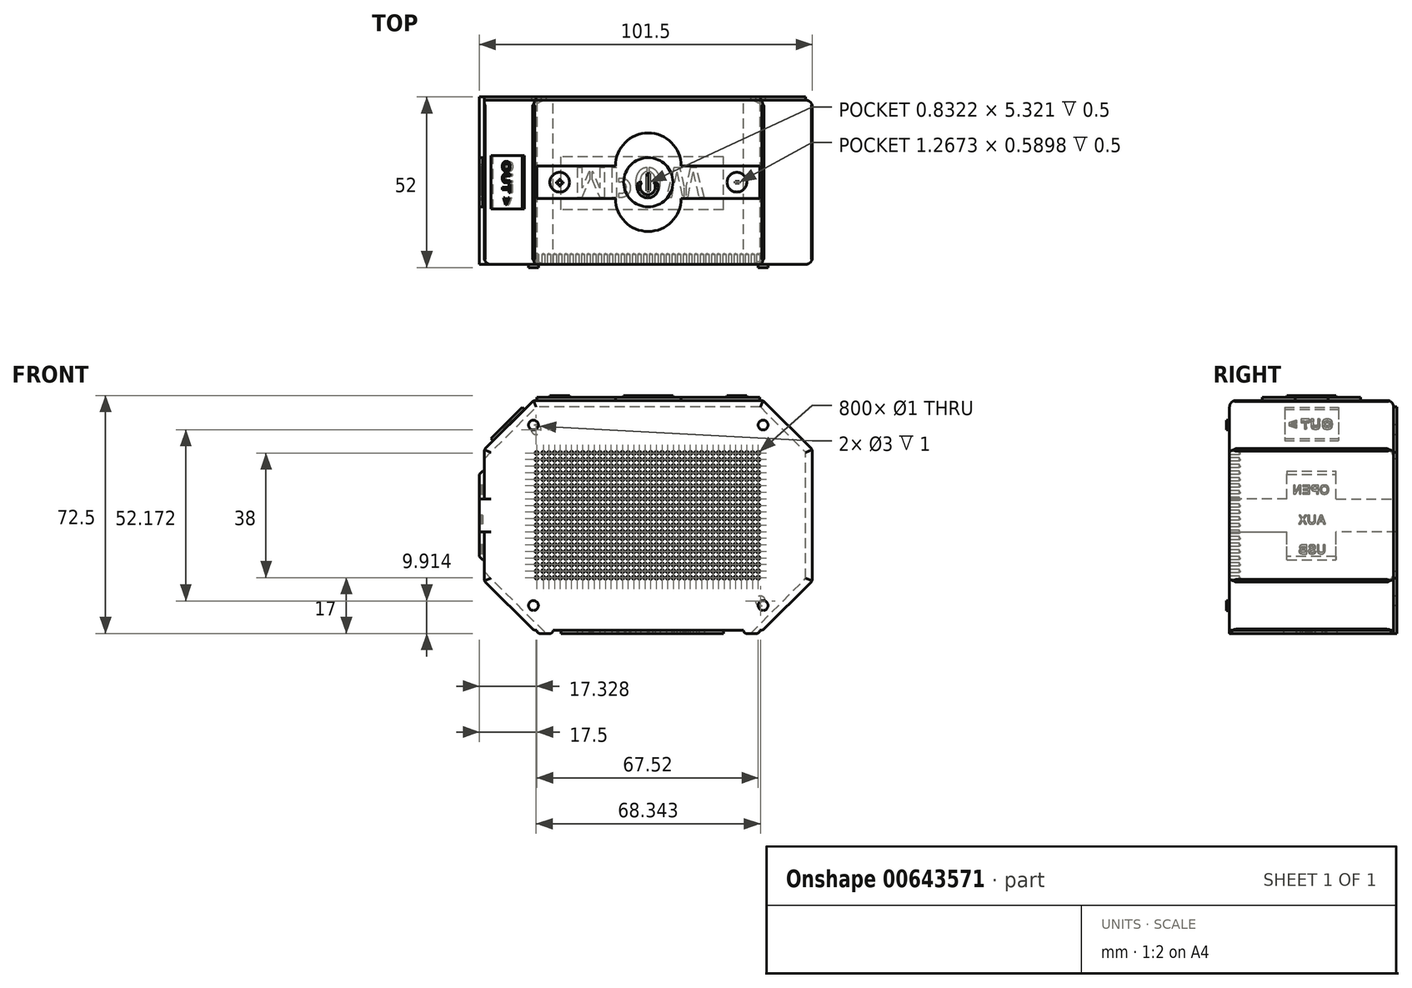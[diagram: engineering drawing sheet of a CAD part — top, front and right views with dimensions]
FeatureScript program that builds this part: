
annotation { "Feature Type Name" : "Feature", "Feature Type Description" : "" }
export const myFeature = defineFeature(function(context is Context, id is Id, definition is map)
    precondition{}
    {
        {
            var Q0;
            Q0=qCreatedBy(makeId("Front.planeOp"),FACE);
            var sketch = newSketch(context, id + "F0", { "sketchPlane" : qUnion([Q0])});
            skLineSegment(sketch, "E0.bottom", {"start": v(35, -35) * mm, "end": v(-35, -35) * mm});
            skLineSegment(sketch, "E0.top", {"start": v(35, 35) * mm, "end": v(-35, 35) * mm});
            skLineSegment(sketch, "E0.left", {"start": v(50, -20) * mm, "end": v(50, 20) * mm});
            skLineSegment(sketch, "E0.right", {"start": v(-50, -20) * mm, "end": v(-50, 20) * mm});
            skPoint(sketch, "E0.middle", {"position": v(0, 0) * mm});
            skLineSegment(sketch, "E1", {"start": v(-50, 20) * mm, "end": v(-35, 35) * mm});
            skLineSegment(sketch, "E2", {"start": v(-50, -20) * mm, "end": v(-35, -35) * mm});
            skLineSegment(sketch, "E3", {"start": v(35, -35) * mm, "end": v(50, -20) * mm});
            skLineSegment(sketch, "E4", {"start": v(35, 35) * mm, "end": v(50, 20) * mm});
            skPoint(sketch, "E5.orphan", {"position": v(-50, 35) * mm});
            skPoint(sketch, "E6.orphan", {"position": v(50, 35) * mm});
            skPoint(sketch, "E7.orphan", {"position": v(-50, -35) * mm});
            skPoint(sketch, "E8.orphan", {"position": v(50, -35) * mm});
            skSolve(sketch);
        }
        {
            var Q0;
            Q0 = qSketchRegion(id + "F0", true);
            extrude(context, id + "F1", {"entities" : qUnion([Q0]), "oppositeDirection" : true, "depth" : 50 * mm, "offsetDistance" : 25 * mm});
        }
        {
            var Q0;
            Q0=makeQuery(id+"F1.opExtrude","SWEPT_EDGE",EDGE,{"disambiguationData":[OSD([sQuery(id+"F0.wireOp",EDGE,"E0.top"),sQuery(id+"F0.wireOp",EDGE,"E4")])]});
            var Q1;
            Q1=makeQuery(id+"F1.opExtrude","SWEPT_EDGE",EDGE,{"disambiguationData":[OSD([sQuery(id+"F0.wireOp",EDGE,"E0.left"),sQuery(id+"F0.wireOp",EDGE,"E4")])]});
            var Q2;
            Q2=makeQuery(id+"F1.opExtrude","SWEPT_EDGE",EDGE,{"disambiguationData":[OSD([sQuery(id+"F0.wireOp",EDGE,"E0.left"),sQuery(id+"F0.wireOp",EDGE,"E3")])]});
            var Q3;
            Q3=makeQuery(id+"F1.opExtrude","SWEPT_EDGE",EDGE,{"disambiguationData":[OSD([sQuery(id+"F0.wireOp",EDGE,"E0.bottom"),sQuery(id+"F0.wireOp",EDGE,"E3")])]});
            var Q4;
            Q4=makeQuery(id+"F1.opExtrude","SWEPT_EDGE",EDGE,{"disambiguationData":[OSD([sQuery(id+"F0.wireOp",EDGE,"E0.bottom"),sQuery(id+"F0.wireOp",EDGE,"E2")])]});
            var Q5;
            Q5=makeQuery(id+"F1.opExtrude","SWEPT_EDGE",EDGE,{"disambiguationData":[OSD([sQuery(id+"F0.wireOp",EDGE,"E0.right"),sQuery(id+"F0.wireOp",EDGE,"E2")])]});
            var Q6;
            Q6=makeQuery(id+"F1.opExtrude","SWEPT_EDGE",EDGE,{"disambiguationData":[OSD([sQuery(id+"F0.wireOp",EDGE,"E0.right"),sQuery(id+"F0.wireOp",EDGE,"E1")])]});
            var Q7;
            Q7=makeQuery(id+"F1.opExtrude","SWEPT_EDGE",EDGE,{"disambiguationData":[OSD([sQuery(id+"F0.wireOp",EDGE,"E0.top"),sQuery(id+"F0.wireOp",EDGE,"E1")])]});
            chamfer(context, id + "F2", {"entities" : qUnion([Q0, Q1, Q2, Q3, Q4, Q5, Q6, Q7]), "width" : 1 * mm, "tangentPropagation" : true});
        }
        {
            var Q0;
            Q0=makeQuery(id+"F0.imprint","IMPRINT",FACE,{"disambiguationData":[TD([[makeQuery(id+"F0.imprint","IMPRINT",EDGE,{"derivedFrom":sQuery(id+"F0.wireOp",EDGE,"E0.bottom")}),-1.0]])]});
            var sketch = newSketch(context, id + "F3", { "sketchPlane" : qUnion([Q0])});
            skLineSegment(sketch, "E9.bottom", {"start": v(35, -20) * mm, "end": v(-35, -20) * mm});
            skLineSegment(sketch, "E9.top", {"start": v(35, 20) * mm, "end": v(-35, 20) * mm});
            skLineSegment(sketch, "E9.left", {"start": v(35, -20) * mm, "end": v(35, 20) * mm});
            skLineSegment(sketch, "E9.right", {"start": v(-35, -20) * mm, "end": v(-35, 20) * mm});
            skLineSegment(sketch, "E10", {"start": v(0, 20) * mm, "end": v(0, 0) * mm, "construction": true});
            skLineSegment(sketch, "E11", {"start": v(0, 0) * mm, "end": v(0, -20) * mm, "construction": true});
            skPoint(sketch, "E12", {"position": v(-35, 20) * mm});
            skPoint(sketch, "E13.1.0.0", {"position": v(-32, 19) * mm});
            skPoint(sketch, "E13.2.0.0", {"position": v(-30.28, 19) * mm});
            skLineSegment(sketch, "E13.direction1", {"start": v(-34, 19) * mm, "end": v(-32, 19) * mm});
            skPoint(sketch, "E14.0.3.0", {"position": v(-28.55, 19) * mm});
            skPoint(sketch, "E14.0.4.0", {"position": v(-26.83, 19) * mm});
            skPoint(sketch, "E15.0.5.0", {"position": v(-25.1, 19) * mm});
            skPoint(sketch, "E15.0.6.0", {"position": v(-23.38, 19) * mm});
            skPoint(sketch, "E15.0.7.0", {"position": v(-21.65, 19) * mm});
            skPoint(sketch, "E15.0.8.0", {"position": v(-19.93, 19) * mm});
            skPoint(sketch, "E15.0.9.0", {"position": v(-18.2, 19) * mm});
            skPoint(sketch, "E16.0.10.0", {"position": v(-16.48, 19) * mm});
            skPoint(sketch, "E16.0.11.0", {"position": v(-14.76, 19) * mm});
            skPoint(sketch, "E16.0.12.0", {"position": v(-13.03, 19) * mm});
            skPoint(sketch, "E16.0.13.0", {"position": v(-11.3, 19) * mm});
            skPoint(sketch, "E16.0.14.0", {"position": v(-9.59, 19) * mm});
            skPoint(sketch, "E16.0.15.0", {"position": v(-7.86, 19) * mm});
            skPoint(sketch, "E16.0.16.0", {"position": v(-6.14, 19) * mm});
            skPoint(sketch, "E16.0.17.0", {"position": v(-4.41, 19) * mm});
            skPoint(sketch, "E16.0.18.0", {"position": v(-2.69, 19) * mm});
            skPoint(sketch, "E16.0.19.0", {"position": v(-0.96, 19) * mm});
            skPoint(sketch, "E17.0.20.0", {"position": v(0.76, 19) * mm});
            skPoint(sketch, "E17.0.21.0", {"position": v(2.48, 19) * mm});
            skPoint(sketch, "E17.0.22.0", {"position": v(4.2, 19) * mm});
            skPoint(sketch, "E17.0.23.0", {"position": v(5.93, 19) * mm});
            skPoint(sketch, "E17.0.24.0", {"position": v(7.66, 19) * mm});
            skPoint(sketch, "E17.0.25.0", {"position": v(9.38, 19) * mm});
            skPoint(sketch, "E17.0.26.0", {"position": v(11.1, 19) * mm});
            skPoint(sketch, "E17.0.27.0", {"position": v(12.83, 19) * mm});
            skPoint(sketch, "E17.0.28.0", {"position": v(14.55, 19) * mm});
            skPoint(sketch, "E17.0.29.0", {"position": v(16.28, 19) * mm});
            skPoint(sketch, "E17.0.30.0", {"position": v(18, 19) * mm});
            skPoint(sketch, "E17.0.31.0", {"position": v(19.73, 19) * mm});
            skPoint(sketch, "E17.0.32.0", {"position": v(21.45, 19) * mm});
            skPoint(sketch, "E17.0.33.0", {"position": v(23.17, 19) * mm});
            skPoint(sketch, "E17.0.34.0", {"position": v(24.9, 19) * mm});
            skPoint(sketch, "E17.0.35.0", {"position": v(26.62, 19) * mm});
            skPoint(sketch, "E17.0.36.0", {"position": v(28.35, 19) * mm});
            skPoint(sketch, "E17.0.37.0", {"position": v(30.07, 19) * mm});
            skPoint(sketch, "E17.0.38.0", {"position": v(31.8, 19) * mm});
            skPoint(sketch, "E17.0.39.0", {"position": v(33.52, 19) * mm});
            skPoint(sketch, "E18.1.0.0", {"position": v(18, 17) * mm});
            skPoint(sketch, "E18.1.0.1", {"position": v(30.07, 17) * mm});
            skPoint(sketch, "E18.1.0.2", {"position": v(9.38, 17) * mm});
            skPoint(sketch, "E18.1.0.3", {"position": v(12.83, 17) * mm});
            skPoint(sketch, "E18.1.0.4", {"position": v(33.52, 17) * mm});
            skPoint(sketch, "E18.1.0.5", {"position": v(-25.1, 17) * mm});
            skPoint(sketch, "E18.1.0.6", {"position": v(28.35, 17) * mm});
            skPoint(sketch, "E18.1.0.7", {"position": v(-21.65, 17) * mm});
            skPoint(sketch, "E18.1.0.8", {"position": v(-23.38, 17) * mm});
            skPoint(sketch, "E18.1.0.9", {"position": v(23.17, 17) * mm});
            skPoint(sketch, "E18.1.0.10", {"position": v(-7.86, 17) * mm});
            skPoint(sketch, "E18.1.0.11", {"position": v(-32, 17) * mm});
            skPoint(sketch, "E18.1.0.12", {"position": v(-35, 18) * mm});
            skPoint(sketch, "E18.1.0.13", {"position": v(-28.55, 17) * mm});
            skPoint(sketch, "E18.1.0.14", {"position": v(-11.3, 17) * mm});
            skPoint(sketch, "E18.1.0.15", {"position": v(-0.96, 17) * mm});
            skPoint(sketch, "E18.1.0.16", {"position": v(19.73, 17) * mm});
            skPoint(sketch, "E18.1.0.17", {"position": v(7.66, 17) * mm});
            skPoint(sketch, "E18.1.0.18", {"position": v(-14.76, 17) * mm});
            skPoint(sketch, "E18.1.0.19", {"position": v(16.28, 17) * mm});
            skPoint(sketch, "E18.1.0.20", {"position": v(5.93, 17) * mm});
            skPoint(sketch, "E18.1.0.21", {"position": v(-2.69, 17) * mm});
            skPoint(sketch, "E18.1.0.22", {"position": v(0.76, 17) * mm});
            skPoint(sketch, "E18.1.0.23", {"position": v(14.55, 17) * mm});
            skPoint(sketch, "E18.1.0.24", {"position": v(-30.28, 17) * mm});
            skPoint(sketch, "E18.1.0.25", {"position": v(24.9, 17) * mm});
            skPoint(sketch, "E18.1.0.26", {"position": v(11.1, 17) * mm});
            skPoint(sketch, "E18.1.0.27", {"position": v(-6.14, 17) * mm});
            skPoint(sketch, "E18.1.0.28", {"position": v(-18.2, 17) * mm});
            skPoint(sketch, "E18.1.0.29", {"position": v(-13.03, 17) * mm});
            skPoint(sketch, "E18.1.0.30", {"position": v(21.45, 17) * mm});
            skPoint(sketch, "E18.1.0.31", {"position": v(26.62, 17) * mm});
            skPoint(sketch, "E18.1.0.32", {"position": v(-26.83, 17) * mm});
            skPoint(sketch, "E18.1.0.33", {"position": v(-4.41, 17) * mm});
            skPoint(sketch, "E18.1.0.34", {"position": v(-19.93, 17) * mm});
            skPoint(sketch, "E18.1.0.35", {"position": v(31.8, 17) * mm});
            skPoint(sketch, "E18.1.0.36", {"position": v(-16.48, 17) * mm});
            skPoint(sketch, "E18.1.0.37", {"position": v(4.2, 17) * mm});
            skPoint(sketch, "E18.1.0.38", {"position": v(-9.59, 17) * mm});
            skPoint(sketch, "E18.1.0.39", {"position": v(2.48, 17) * mm});
            skLineSegment(sketch, "E18.1.0.40", {"start": v(-34, 17) * mm, "end": v(-32, 17) * mm});
            skPoint(sketch, "E18.2.0.0", {"position": v(18, 15) * mm});
            skPoint(sketch, "E18.2.0.1", {"position": v(30.07, 15) * mm});
            skPoint(sketch, "E18.2.0.2", {"position": v(9.38, 15) * mm});
            skPoint(sketch, "E18.2.0.3", {"position": v(12.83, 15) * mm});
            skPoint(sketch, "E18.2.0.4", {"position": v(33.52, 15) * mm});
            skPoint(sketch, "E18.2.0.5", {"position": v(-25.1, 15) * mm});
            skPoint(sketch, "E18.2.0.6", {"position": v(28.35, 15) * mm});
            skPoint(sketch, "E18.2.0.7", {"position": v(-21.65, 15) * mm});
            skPoint(sketch, "E18.2.0.8", {"position": v(-23.38, 15) * mm});
            skPoint(sketch, "E18.2.0.9", {"position": v(23.17, 15) * mm});
            skPoint(sketch, "E18.2.0.10", {"position": v(-7.86, 15) * mm});
            skPoint(sketch, "E18.2.0.11", {"position": v(-32, 15) * mm});
            skPoint(sketch, "E18.2.0.12", {"position": v(-35, 16) * mm});
            skPoint(sketch, "E18.2.0.13", {"position": v(-28.55, 15) * mm});
            skPoint(sketch, "E18.2.0.14", {"position": v(-11.3, 15) * mm});
            skPoint(sketch, "E18.2.0.15", {"position": v(-0.96, 15) * mm});
            skPoint(sketch, "E18.2.0.16", {"position": v(19.73, 15) * mm});
            skPoint(sketch, "E18.2.0.17", {"position": v(7.66, 15) * mm});
            skPoint(sketch, "E18.2.0.18", {"position": v(-14.76, 15) * mm});
            skPoint(sketch, "E18.2.0.19", {"position": v(16.28, 15) * mm});
            skPoint(sketch, "E18.2.0.20", {"position": v(5.93, 15) * mm});
            skPoint(sketch, "E18.2.0.21", {"position": v(-2.69, 15) * mm});
            skPoint(sketch, "E18.2.0.22", {"position": v(0.76, 15) * mm});
            skPoint(sketch, "E18.2.0.23", {"position": v(14.55, 15) * mm});
            skPoint(sketch, "E18.2.0.24", {"position": v(-30.28, 15) * mm});
            skPoint(sketch, "E18.2.0.25", {"position": v(24.9, 15) * mm});
            skPoint(sketch, "E18.2.0.26", {"position": v(11.1, 15) * mm});
            skPoint(sketch, "E18.2.0.27", {"position": v(-6.14, 15) * mm});
            skPoint(sketch, "E18.2.0.28", {"position": v(-18.2, 15) * mm});
            skPoint(sketch, "E18.2.0.29", {"position": v(-13.03, 15) * mm});
            skPoint(sketch, "E18.2.0.30", {"position": v(21.45, 15) * mm});
            skPoint(sketch, "E18.2.0.31", {"position": v(26.62, 15) * mm});
            skPoint(sketch, "E18.2.0.32", {"position": v(-26.83, 15) * mm});
            skPoint(sketch, "E18.2.0.33", {"position": v(-4.41, 15) * mm});
            skPoint(sketch, "E18.2.0.34", {"position": v(-19.93, 15) * mm});
            skPoint(sketch, "E18.2.0.35", {"position": v(31.8, 15) * mm});
            skPoint(sketch, "E18.2.0.36", {"position": v(-16.48, 15) * mm});
            skPoint(sketch, "E18.2.0.37", {"position": v(4.2, 15) * mm});
            skPoint(sketch, "E18.2.0.38", {"position": v(-9.59, 15) * mm});
            skPoint(sketch, "E18.2.0.39", {"position": v(2.48, 15) * mm});
            skLineSegment(sketch, "E18.2.0.40", {"start": v(-34, 15) * mm, "end": v(-32, 15) * mm});
            skPoint(sketch, "E18.3.0.0", {"position": v(18, 13) * mm});
            skPoint(sketch, "E18.3.0.1", {"position": v(30.07, 13) * mm});
            skPoint(sketch, "E18.3.0.2", {"position": v(9.38, 13) * mm});
            skPoint(sketch, "E18.3.0.3", {"position": v(12.83, 13) * mm});
            skPoint(sketch, "E18.3.0.4", {"position": v(33.52, 13) * mm});
            skPoint(sketch, "E18.3.0.5", {"position": v(-25.1, 13) * mm});
            skPoint(sketch, "E18.3.0.6", {"position": v(28.35, 13) * mm});
            skPoint(sketch, "E18.3.0.7", {"position": v(-21.65, 13) * mm});
            skPoint(sketch, "E18.3.0.8", {"position": v(-23.38, 13) * mm});
            skPoint(sketch, "E18.3.0.9", {"position": v(23.17, 13) * mm});
            skPoint(sketch, "E18.3.0.10", {"position": v(-7.86, 13) * mm});
            skPoint(sketch, "E18.3.0.11", {"position": v(-32, 13) * mm});
            skPoint(sketch, "E18.3.0.12", {"position": v(-35, 14) * mm});
            skPoint(sketch, "E18.3.0.13", {"position": v(-28.55, 13) * mm});
            skPoint(sketch, "E18.3.0.14", {"position": v(-11.3, 13) * mm});
            skPoint(sketch, "E18.3.0.15", {"position": v(-0.96, 13) * mm});
            skPoint(sketch, "E18.3.0.16", {"position": v(19.73, 13) * mm});
            skPoint(sketch, "E18.3.0.17", {"position": v(7.66, 13) * mm});
            skPoint(sketch, "E18.3.0.18", {"position": v(-14.76, 13) * mm});
            skPoint(sketch, "E18.3.0.19", {"position": v(16.28, 13) * mm});
            skPoint(sketch, "E18.3.0.20", {"position": v(5.93, 13) * mm});
            skPoint(sketch, "E18.3.0.21", {"position": v(-2.69, 13) * mm});
            skPoint(sketch, "E18.3.0.22", {"position": v(0.76, 13) * mm});
            skPoint(sketch, "E18.3.0.23", {"position": v(14.55, 13) * mm});
            skPoint(sketch, "E18.3.0.24", {"position": v(-30.28, 13) * mm});
            skPoint(sketch, "E18.3.0.25", {"position": v(24.9, 13) * mm});
            skPoint(sketch, "E18.3.0.26", {"position": v(11.1, 13) * mm});
            skPoint(sketch, "E18.3.0.27", {"position": v(-6.14, 13) * mm});
            skPoint(sketch, "E18.3.0.28", {"position": v(-18.2, 13) * mm});
            skPoint(sketch, "E18.3.0.29", {"position": v(-13.03, 13) * mm});
            skPoint(sketch, "E18.3.0.30", {"position": v(21.45, 13) * mm});
            skPoint(sketch, "E18.3.0.31", {"position": v(26.62, 13) * mm});
            skPoint(sketch, "E18.3.0.32", {"position": v(-26.83, 13) * mm});
            skPoint(sketch, "E18.3.0.33", {"position": v(-4.41, 13) * mm});
            skPoint(sketch, "E18.3.0.34", {"position": v(-19.93, 13) * mm});
            skPoint(sketch, "E18.3.0.35", {"position": v(31.8, 13) * mm});
            skPoint(sketch, "E18.3.0.36", {"position": v(-16.48, 13) * mm});
            skPoint(sketch, "E18.3.0.37", {"position": v(4.2, 13) * mm});
            skPoint(sketch, "E18.3.0.38", {"position": v(-9.59, 13) * mm});
            skPoint(sketch, "E18.3.0.39", {"position": v(2.48, 13) * mm});
            skLineSegment(sketch, "E18.3.0.40", {"start": v(-34, 13) * mm, "end": v(-32, 13) * mm});
            skPoint(sketch, "E18.4.0.0", {"position": v(18, 11) * mm});
            skPoint(sketch, "E18.4.0.1", {"position": v(30.07, 11) * mm});
            skPoint(sketch, "E18.4.0.2", {"position": v(9.38, 11) * mm});
            skPoint(sketch, "E18.4.0.3", {"position": v(12.83, 11) * mm});
            skPoint(sketch, "E18.4.0.4", {"position": v(33.52, 11) * mm});
            skPoint(sketch, "E18.4.0.5", {"position": v(-25.1, 11) * mm});
            skPoint(sketch, "E18.4.0.6", {"position": v(28.35, 11) * mm});
            skPoint(sketch, "E18.4.0.7", {"position": v(-21.65, 11) * mm});
            skPoint(sketch, "E18.4.0.8", {"position": v(-23.38, 11) * mm});
            skPoint(sketch, "E18.4.0.9", {"position": v(23.17, 11) * mm});
            skPoint(sketch, "E18.4.0.10", {"position": v(-7.86, 11) * mm});
            skPoint(sketch, "E18.4.0.11", {"position": v(-32, 11) * mm});
            skPoint(sketch, "E18.4.0.12", {"position": v(-35, 12) * mm});
            skPoint(sketch, "E18.4.0.13", {"position": v(-28.55, 11) * mm});
            skPoint(sketch, "E18.4.0.14", {"position": v(-11.3, 11) * mm});
            skPoint(sketch, "E18.4.0.15", {"position": v(-0.96, 11) * mm});
            skPoint(sketch, "E18.4.0.16", {"position": v(19.73, 11) * mm});
            skPoint(sketch, "E18.4.0.17", {"position": v(7.66, 11) * mm});
            skPoint(sketch, "E18.4.0.18", {"position": v(-14.76, 11) * mm});
            skPoint(sketch, "E18.4.0.19", {"position": v(16.28, 11) * mm});
            skPoint(sketch, "E18.4.0.20", {"position": v(5.93, 11) * mm});
            skPoint(sketch, "E18.4.0.21", {"position": v(-2.69, 11) * mm});
            skPoint(sketch, "E18.4.0.22", {"position": v(0.76, 11) * mm});
            skPoint(sketch, "E18.4.0.23", {"position": v(14.55, 11) * mm});
            skPoint(sketch, "E18.4.0.24", {"position": v(-30.28, 11) * mm});
            skPoint(sketch, "E18.4.0.25", {"position": v(24.9, 11) * mm});
            skPoint(sketch, "E18.4.0.26", {"position": v(11.1, 11) * mm});
            skPoint(sketch, "E18.4.0.27", {"position": v(-6.14, 11) * mm});
            skPoint(sketch, "E18.4.0.28", {"position": v(-18.2, 11) * mm});
            skPoint(sketch, "E18.4.0.29", {"position": v(-13.03, 11) * mm});
            skPoint(sketch, "E18.4.0.30", {"position": v(21.45, 11) * mm});
            skPoint(sketch, "E18.4.0.31", {"position": v(26.62, 11) * mm});
            skPoint(sketch, "E18.4.0.32", {"position": v(-26.83, 11) * mm});
            skPoint(sketch, "E18.4.0.33", {"position": v(-4.41, 11) * mm});
            skPoint(sketch, "E18.4.0.34", {"position": v(-19.93, 11) * mm});
            skPoint(sketch, "E18.4.0.35", {"position": v(31.8, 11) * mm});
            skPoint(sketch, "E18.4.0.36", {"position": v(-16.48, 11) * mm});
            skPoint(sketch, "E18.4.0.37", {"position": v(4.2, 11) * mm});
            skPoint(sketch, "E18.4.0.38", {"position": v(-9.59, 11) * mm});
            skPoint(sketch, "E18.4.0.39", {"position": v(2.48, 11) * mm});
            skLineSegment(sketch, "E18.4.0.40", {"start": v(-34, 11) * mm, "end": v(-32, 11) * mm});
            skPoint(sketch, "E18.5.0.0", {"position": v(18, 9) * mm});
            skPoint(sketch, "E18.5.0.1", {"position": v(30.07, 9) * mm});
            skPoint(sketch, "E18.5.0.2", {"position": v(9.38, 9) * mm});
            skPoint(sketch, "E18.5.0.3", {"position": v(12.83, 9) * mm});
            skPoint(sketch, "E18.5.0.4", {"position": v(33.52, 9) * mm});
            skPoint(sketch, "E18.5.0.5", {"position": v(-25.1, 9) * mm});
            skPoint(sketch, "E18.5.0.6", {"position": v(28.35, 9) * mm});
            skPoint(sketch, "E18.5.0.7", {"position": v(-21.65, 9) * mm});
            skPoint(sketch, "E18.5.0.8", {"position": v(-23.38, 9) * mm});
            skPoint(sketch, "E18.5.0.9", {"position": v(23.17, 9) * mm});
            skPoint(sketch, "E18.5.0.10", {"position": v(-7.86, 9) * mm});
            skPoint(sketch, "E18.5.0.11", {"position": v(-32, 9) * mm});
            skPoint(sketch, "E18.5.0.12", {"position": v(-35, 10) * mm});
            skPoint(sketch, "E18.5.0.13", {"position": v(-28.55, 9) * mm});
            skPoint(sketch, "E18.5.0.14", {"position": v(-11.3, 9) * mm});
            skPoint(sketch, "E18.5.0.15", {"position": v(-0.96, 9) * mm});
            skPoint(sketch, "E18.5.0.16", {"position": v(19.73, 9) * mm});
            skPoint(sketch, "E18.5.0.17", {"position": v(7.66, 9) * mm});
            skPoint(sketch, "E18.5.0.18", {"position": v(-14.76, 9) * mm});
            skPoint(sketch, "E18.5.0.19", {"position": v(16.28, 9) * mm});
            skPoint(sketch, "E18.5.0.20", {"position": v(5.93, 9) * mm});
            skPoint(sketch, "E18.5.0.21", {"position": v(-2.69, 9) * mm});
            skPoint(sketch, "E18.5.0.22", {"position": v(0.76, 9) * mm});
            skPoint(sketch, "E18.5.0.23", {"position": v(14.55, 9) * mm});
            skPoint(sketch, "E18.5.0.24", {"position": v(-30.28, 9) * mm});
            skPoint(sketch, "E18.5.0.25", {"position": v(24.9, 9) * mm});
            skPoint(sketch, "E18.5.0.26", {"position": v(11.1, 9) * mm});
            skPoint(sketch, "E18.5.0.27", {"position": v(-6.14, 9) * mm});
            skPoint(sketch, "E18.5.0.28", {"position": v(-18.2, 9) * mm});
            skPoint(sketch, "E18.5.0.29", {"position": v(-13.03, 9) * mm});
            skPoint(sketch, "E18.5.0.30", {"position": v(21.45, 9) * mm});
            skPoint(sketch, "E18.5.0.31", {"position": v(26.62, 9) * mm});
            skPoint(sketch, "E18.5.0.32", {"position": v(-26.83, 9) * mm});
            skPoint(sketch, "E18.5.0.33", {"position": v(-4.41, 9) * mm});
            skPoint(sketch, "E18.5.0.34", {"position": v(-19.93, 9) * mm});
            skPoint(sketch, "E18.5.0.35", {"position": v(31.8, 9) * mm});
            skPoint(sketch, "E18.5.0.36", {"position": v(-16.48, 9) * mm});
            skPoint(sketch, "E18.5.0.37", {"position": v(4.2, 9) * mm});
            skPoint(sketch, "E18.5.0.38", {"position": v(-9.59, 9) * mm});
            skPoint(sketch, "E18.5.0.39", {"position": v(2.48, 9) * mm});
            skLineSegment(sketch, "E18.5.0.40", {"start": v(-34, 9) * mm, "end": v(-32, 9) * mm});
            skPoint(sketch, "E18.6.0.0", {"position": v(18, 7) * mm});
            skPoint(sketch, "E18.6.0.1", {"position": v(30.07, 7) * mm});
            skPoint(sketch, "E18.6.0.2", {"position": v(9.38, 7) * mm});
            skPoint(sketch, "E18.6.0.3", {"position": v(12.83, 7) * mm});
            skPoint(sketch, "E18.6.0.4", {"position": v(33.52, 7) * mm});
            skPoint(sketch, "E18.6.0.5", {"position": v(-25.1, 7) * mm});
            skPoint(sketch, "E18.6.0.6", {"position": v(28.35, 7) * mm});
            skPoint(sketch, "E18.6.0.7", {"position": v(-21.65, 7) * mm});
            skPoint(sketch, "E18.6.0.8", {"position": v(-23.38, 7) * mm});
            skPoint(sketch, "E18.6.0.9", {"position": v(23.17, 7) * mm});
            skPoint(sketch, "E18.6.0.10", {"position": v(-7.86, 7) * mm});
            skPoint(sketch, "E18.6.0.11", {"position": v(-32, 7) * mm});
            skPoint(sketch, "E18.6.0.12", {"position": v(-35, 8) * mm});
            skPoint(sketch, "E18.6.0.13", {"position": v(-28.55, 7) * mm});
            skPoint(sketch, "E18.6.0.14", {"position": v(-11.3, 7) * mm});
            skPoint(sketch, "E18.6.0.15", {"position": v(-0.96, 7) * mm});
            skPoint(sketch, "E18.6.0.16", {"position": v(19.73, 7) * mm});
            skPoint(sketch, "E18.6.0.17", {"position": v(7.66, 7) * mm});
            skPoint(sketch, "E18.6.0.18", {"position": v(-14.76, 7) * mm});
            skPoint(sketch, "E18.6.0.19", {"position": v(16.28, 7) * mm});
            skPoint(sketch, "E18.6.0.20", {"position": v(5.93, 7) * mm});
            skPoint(sketch, "E18.6.0.21", {"position": v(-2.69, 7) * mm});
            skPoint(sketch, "E18.6.0.22", {"position": v(0.76, 7) * mm});
            skPoint(sketch, "E18.6.0.23", {"position": v(14.55, 7) * mm});
            skPoint(sketch, "E18.6.0.24", {"position": v(-30.28, 7) * mm});
            skPoint(sketch, "E18.6.0.25", {"position": v(24.9, 7) * mm});
            skPoint(sketch, "E18.6.0.26", {"position": v(11.1, 7) * mm});
            skPoint(sketch, "E18.6.0.27", {"position": v(-6.14, 7) * mm});
            skPoint(sketch, "E18.6.0.28", {"position": v(-18.2, 7) * mm});
            skPoint(sketch, "E18.6.0.29", {"position": v(-13.03, 7) * mm});
            skPoint(sketch, "E18.6.0.30", {"position": v(21.45, 7) * mm});
            skPoint(sketch, "E18.6.0.31", {"position": v(26.62, 7) * mm});
            skPoint(sketch, "E18.6.0.32", {"position": v(-26.83, 7) * mm});
            skPoint(sketch, "E18.6.0.33", {"position": v(-4.41, 7) * mm});
            skPoint(sketch, "E18.6.0.34", {"position": v(-19.93, 7) * mm});
            skPoint(sketch, "E18.6.0.35", {"position": v(31.8, 7) * mm});
            skPoint(sketch, "E18.6.0.36", {"position": v(-16.48, 7) * mm});
            skPoint(sketch, "E18.6.0.37", {"position": v(4.2, 7) * mm});
            skPoint(sketch, "E18.6.0.38", {"position": v(-9.59, 7) * mm});
            skPoint(sketch, "E18.6.0.39", {"position": v(2.48, 7) * mm});
            skLineSegment(sketch, "E18.6.0.40", {"start": v(-34, 7) * mm, "end": v(-32, 7) * mm});
            skPoint(sketch, "E18.7.0.0", {"position": v(18, 5) * mm});
            skPoint(sketch, "E18.7.0.1", {"position": v(30.07, 5) * mm});
            skPoint(sketch, "E18.7.0.2", {"position": v(9.38, 5) * mm});
            skPoint(sketch, "E18.7.0.3", {"position": v(12.83, 5) * mm});
            skPoint(sketch, "E18.7.0.4", {"position": v(33.52, 5) * mm});
            skPoint(sketch, "E18.7.0.5", {"position": v(-25.1, 5) * mm});
            skPoint(sketch, "E18.7.0.6", {"position": v(28.35, 5) * mm});
            skPoint(sketch, "E18.7.0.7", {"position": v(-21.65, 5) * mm});
            skPoint(sketch, "E18.7.0.8", {"position": v(-23.38, 5) * mm});
            skPoint(sketch, "E18.7.0.9", {"position": v(23.17, 5) * mm});
            skPoint(sketch, "E18.7.0.10", {"position": v(-7.86, 5) * mm});
            skPoint(sketch, "E18.7.0.11", {"position": v(-32, 5) * mm});
            skPoint(sketch, "E18.7.0.12", {"position": v(-35, 6) * mm});
            skPoint(sketch, "E18.7.0.13", {"position": v(-28.55, 5) * mm});
            skPoint(sketch, "E18.7.0.14", {"position": v(-11.3, 5) * mm});
            skPoint(sketch, "E18.7.0.15", {"position": v(-0.96, 5) * mm});
            skPoint(sketch, "E18.7.0.16", {"position": v(19.73, 5) * mm});
            skPoint(sketch, "E18.7.0.17", {"position": v(7.66, 5) * mm});
            skPoint(sketch, "E18.7.0.18", {"position": v(-14.76, 5) * mm});
            skPoint(sketch, "E18.7.0.19", {"position": v(16.28, 5) * mm});
            skPoint(sketch, "E18.7.0.20", {"position": v(5.93, 5) * mm});
            skPoint(sketch, "E18.7.0.21", {"position": v(-2.69, 5) * mm});
            skPoint(sketch, "E18.7.0.22", {"position": v(0.76, 5) * mm});
            skPoint(sketch, "E18.7.0.23", {"position": v(14.55, 5) * mm});
            skPoint(sketch, "E18.7.0.24", {"position": v(-30.28, 5) * mm});
            skPoint(sketch, "E18.7.0.25", {"position": v(24.9, 5) * mm});
            skPoint(sketch, "E18.7.0.26", {"position": v(11.1, 5) * mm});
            skPoint(sketch, "E18.7.0.27", {"position": v(-6.14, 5) * mm});
            skPoint(sketch, "E18.7.0.28", {"position": v(-18.2, 5) * mm});
            skPoint(sketch, "E18.7.0.29", {"position": v(-13.03, 5) * mm});
            skPoint(sketch, "E18.7.0.30", {"position": v(21.45, 5) * mm});
            skPoint(sketch, "E18.7.0.31", {"position": v(26.62, 5) * mm});
            skPoint(sketch, "E18.7.0.32", {"position": v(-26.83, 5) * mm});
            skPoint(sketch, "E18.7.0.33", {"position": v(-4.41, 5) * mm});
            skPoint(sketch, "E18.7.0.34", {"position": v(-19.93, 5) * mm});
            skPoint(sketch, "E18.7.0.35", {"position": v(31.8, 5) * mm});
            skPoint(sketch, "E18.7.0.36", {"position": v(-16.48, 5) * mm});
            skPoint(sketch, "E18.7.0.37", {"position": v(4.2, 5) * mm});
            skPoint(sketch, "E18.7.0.38", {"position": v(-9.59, 5) * mm});
            skPoint(sketch, "E18.7.0.39", {"position": v(2.48, 5) * mm});
            skLineSegment(sketch, "E18.7.0.40", {"start": v(-34, 5) * mm, "end": v(-32, 5) * mm});
            skPoint(sketch, "E18.8.0.0", {"position": v(18, 3) * mm});
            skPoint(sketch, "E18.8.0.1", {"position": v(30.07, 3) * mm});
            skPoint(sketch, "E18.8.0.2", {"position": v(9.38, 3) * mm});
            skPoint(sketch, "E18.8.0.3", {"position": v(12.83, 3) * mm});
            skPoint(sketch, "E18.8.0.4", {"position": v(33.52, 3) * mm});
            skPoint(sketch, "E18.8.0.5", {"position": v(-25.1, 3) * mm});
            skPoint(sketch, "E18.8.0.6", {"position": v(28.35, 3) * mm});
            skPoint(sketch, "E18.8.0.7", {"position": v(-21.65, 3) * mm});
            skPoint(sketch, "E18.8.0.8", {"position": v(-23.38, 3) * mm});
            skPoint(sketch, "E18.8.0.9", {"position": v(23.17, 3) * mm});
            skPoint(sketch, "E18.8.0.10", {"position": v(-7.86, 3) * mm});
            skPoint(sketch, "E18.8.0.11", {"position": v(-32, 3) * mm});
            skPoint(sketch, "E18.8.0.12", {"position": v(-35, 4) * mm});
            skPoint(sketch, "E18.8.0.13", {"position": v(-28.55, 3) * mm});
            skPoint(sketch, "E18.8.0.14", {"position": v(-11.3, 3) * mm});
            skPoint(sketch, "E18.8.0.15", {"position": v(-0.96, 3) * mm});
            skPoint(sketch, "E18.8.0.16", {"position": v(19.73, 3) * mm});
            skPoint(sketch, "E18.8.0.17", {"position": v(7.66, 3) * mm});
            skPoint(sketch, "E18.8.0.18", {"position": v(-14.76, 3) * mm});
            skPoint(sketch, "E18.8.0.19", {"position": v(16.28, 3) * mm});
            skPoint(sketch, "E18.8.0.20", {"position": v(5.93, 3) * mm});
            skPoint(sketch, "E18.8.0.21", {"position": v(-2.69, 3) * mm});
            skPoint(sketch, "E18.8.0.22", {"position": v(0.76, 3) * mm});
            skPoint(sketch, "E18.8.0.23", {"position": v(14.55, 3) * mm});
            skPoint(sketch, "E18.8.0.24", {"position": v(-30.28, 3) * mm});
            skPoint(sketch, "E18.8.0.25", {"position": v(24.9, 3) * mm});
            skPoint(sketch, "E18.8.0.26", {"position": v(11.1, 3) * mm});
            skPoint(sketch, "E18.8.0.27", {"position": v(-6.14, 3) * mm});
            skPoint(sketch, "E18.8.0.28", {"position": v(-18.2, 3) * mm});
            skPoint(sketch, "E18.8.0.29", {"position": v(-13.03, 3) * mm});
            skPoint(sketch, "E18.8.0.30", {"position": v(21.45, 3) * mm});
            skPoint(sketch, "E18.8.0.31", {"position": v(26.62, 3) * mm});
            skPoint(sketch, "E18.8.0.32", {"position": v(-26.83, 3) * mm});
            skPoint(sketch, "E18.8.0.33", {"position": v(-4.41, 3) * mm});
            skPoint(sketch, "E18.8.0.34", {"position": v(-19.93, 3) * mm});
            skPoint(sketch, "E18.8.0.35", {"position": v(31.8, 3) * mm});
            skPoint(sketch, "E18.8.0.36", {"position": v(-16.48, 3) * mm});
            skPoint(sketch, "E18.8.0.37", {"position": v(4.2, 3) * mm});
            skPoint(sketch, "E18.8.0.38", {"position": v(-9.59, 3) * mm});
            skPoint(sketch, "E18.8.0.39", {"position": v(2.48, 3) * mm});
            skLineSegment(sketch, "E18.8.0.40", {"start": v(-34, 3) * mm, "end": v(-32, 3) * mm});
            skPoint(sketch, "E18.9.0.0", {"position": v(18, 1) * mm});
            skPoint(sketch, "E18.9.0.1", {"position": v(30.07, 1) * mm});
            skPoint(sketch, "E18.9.0.2", {"position": v(9.38, 1) * mm});
            skPoint(sketch, "E18.9.0.3", {"position": v(12.83, 1) * mm});
            skPoint(sketch, "E18.9.0.4", {"position": v(33.52, 1) * mm});
            skPoint(sketch, "E18.9.0.5", {"position": v(-25.1, 1) * mm});
            skPoint(sketch, "E18.9.0.6", {"position": v(28.35, 1) * mm});
            skPoint(sketch, "E18.9.0.7", {"position": v(-21.65, 1) * mm});
            skPoint(sketch, "E18.9.0.8", {"position": v(-23.38, 1) * mm});
            skPoint(sketch, "E18.9.0.9", {"position": v(23.17, 1) * mm});
            skPoint(sketch, "E18.9.0.10", {"position": v(-7.86, 1) * mm});
            skPoint(sketch, "E18.9.0.11", {"position": v(-32, 1) * mm});
            skPoint(sketch, "E18.9.0.12", {"position": v(-35, 2) * mm});
            skPoint(sketch, "E18.9.0.13", {"position": v(-28.55, 1) * mm});
            skPoint(sketch, "E18.9.0.14", {"position": v(-11.3, 1) * mm});
            skPoint(sketch, "E18.9.0.15", {"position": v(-0.96, 1) * mm});
            skPoint(sketch, "E18.9.0.16", {"position": v(19.73, 1) * mm});
            skPoint(sketch, "E18.9.0.17", {"position": v(7.66, 1) * mm});
            skPoint(sketch, "E18.9.0.18", {"position": v(-14.76, 1) * mm});
            skPoint(sketch, "E18.9.0.19", {"position": v(16.28, 1) * mm});
            skPoint(sketch, "E18.9.0.20", {"position": v(5.93, 1) * mm});
            skPoint(sketch, "E18.9.0.21", {"position": v(-2.69, 1) * mm});
            skPoint(sketch, "E18.9.0.22", {"position": v(0.76, 1) * mm});
            skPoint(sketch, "E18.9.0.23", {"position": v(14.55, 1) * mm});
            skPoint(sketch, "E18.9.0.24", {"position": v(-30.28, 1) * mm});
            skPoint(sketch, "E18.9.0.25", {"position": v(24.9, 1) * mm});
            skPoint(sketch, "E18.9.0.26", {"position": v(11.1, 1) * mm});
            skPoint(sketch, "E18.9.0.27", {"position": v(-6.14, 1) * mm});
            skPoint(sketch, "E18.9.0.28", {"position": v(-18.2, 1) * mm});
            skPoint(sketch, "E18.9.0.29", {"position": v(-13.03, 1) * mm});
            skPoint(sketch, "E18.9.0.30", {"position": v(21.45, 1) * mm});
            skPoint(sketch, "E18.9.0.31", {"position": v(26.62, 1) * mm});
            skPoint(sketch, "E18.9.0.32", {"position": v(-26.83, 1) * mm});
            skPoint(sketch, "E18.9.0.33", {"position": v(-4.41, 1) * mm});
            skPoint(sketch, "E18.9.0.34", {"position": v(-19.93, 1) * mm});
            skPoint(sketch, "E18.9.0.35", {"position": v(31.8, 1) * mm});
            skPoint(sketch, "E18.9.0.36", {"position": v(-16.48, 1) * mm});
            skPoint(sketch, "E18.9.0.37", {"position": v(4.2, 1) * mm});
            skPoint(sketch, "E18.9.0.38", {"position": v(-9.59, 1) * mm});
            skPoint(sketch, "E18.9.0.39", {"position": v(2.48, 1) * mm});
            skLineSegment(sketch, "E18.9.0.40", {"start": v(-34, 1) * mm, "end": v(-32, 1) * mm});
            skPoint(sketch, "E18.10.0.0", {"position": v(18, -1) * mm});
            skPoint(sketch, "E18.10.0.1", {"position": v(30.07, -1) * mm});
            skPoint(sketch, "E18.10.0.2", {"position": v(9.38, -1) * mm});
            skPoint(sketch, "E18.10.0.3", {"position": v(12.83, -1) * mm});
            skPoint(sketch, "E18.10.0.4", {"position": v(33.52, -1) * mm});
            skPoint(sketch, "E18.10.0.5", {"position": v(-25.1, -1) * mm});
            skPoint(sketch, "E18.10.0.6", {"position": v(28.35, -1) * mm});
            skPoint(sketch, "E18.10.0.7", {"position": v(-21.65, -1) * mm});
            skPoint(sketch, "E18.10.0.8", {"position": v(-23.38, -1) * mm});
            skPoint(sketch, "E18.10.0.9", {"position": v(23.17, -1) * mm});
            skPoint(sketch, "E18.10.0.10", {"position": v(-7.86, -1) * mm});
            skPoint(sketch, "E18.10.0.11", {"position": v(-32, -1) * mm});
            skPoint(sketch, "E18.10.0.12", {"position": v(-35, 0) * mm});
            skPoint(sketch, "E18.10.0.13", {"position": v(-28.55, -1) * mm});
            skPoint(sketch, "E18.10.0.14", {"position": v(-11.3, -1) * mm});
            skPoint(sketch, "E18.10.0.15", {"position": v(-0.96, -1) * mm});
            skPoint(sketch, "E18.10.0.16", {"position": v(19.73, -1) * mm});
            skPoint(sketch, "E18.10.0.17", {"position": v(7.66, -1) * mm});
            skPoint(sketch, "E18.10.0.18", {"position": v(-14.76, -1) * mm});
            skPoint(sketch, "E18.10.0.19", {"position": v(16.28, -1) * mm});
            skPoint(sketch, "E18.10.0.20", {"position": v(5.93, -1) * mm});
            skPoint(sketch, "E18.10.0.21", {"position": v(-2.69, -1) * mm});
            skPoint(sketch, "E18.10.0.22", {"position": v(0.76, -1) * mm});
            skPoint(sketch, "E18.10.0.23", {"position": v(14.55, -1) * mm});
            skPoint(sketch, "E18.10.0.24", {"position": v(-30.28, -1) * mm});
            skPoint(sketch, "E18.10.0.25", {"position": v(24.9, -1) * mm});
            skPoint(sketch, "E18.10.0.26", {"position": v(11.1, -1) * mm});
            skPoint(sketch, "E18.10.0.27", {"position": v(-6.14, -1) * mm});
            skPoint(sketch, "E18.10.0.28", {"position": v(-18.2, -1) * mm});
            skPoint(sketch, "E18.10.0.29", {"position": v(-13.03, -1) * mm});
            skPoint(sketch, "E18.10.0.30", {"position": v(21.45, -1) * mm});
            skPoint(sketch, "E18.10.0.31", {"position": v(26.62, -1) * mm});
            skPoint(sketch, "E18.10.0.32", {"position": v(-26.83, -1) * mm});
            skPoint(sketch, "E18.10.0.33", {"position": v(-4.41, -1) * mm});
            skPoint(sketch, "E18.10.0.34", {"position": v(-19.93, -1) * mm});
            skPoint(sketch, "E18.10.0.35", {"position": v(31.8, -1) * mm});
            skPoint(sketch, "E18.10.0.36", {"position": v(-16.48, -1) * mm});
            skPoint(sketch, "E18.10.0.37", {"position": v(4.2, -1) * mm});
            skPoint(sketch, "E18.10.0.38", {"position": v(-9.59, -1) * mm});
            skPoint(sketch, "E18.10.0.39", {"position": v(2.48, -1) * mm});
            skLineSegment(sketch, "E18.10.0.40", {"start": v(-34, -1) * mm, "end": v(-32, -1) * mm});
            skPoint(sketch, "E18.11.0.0", {"position": v(18, -3) * mm});
            skPoint(sketch, "E18.11.0.1", {"position": v(30.07, -3) * mm});
            skPoint(sketch, "E18.11.0.2", {"position": v(9.38, -3) * mm});
            skPoint(sketch, "E18.11.0.3", {"position": v(12.83, -3) * mm});
            skPoint(sketch, "E18.11.0.4", {"position": v(33.52, -3) * mm});
            skPoint(sketch, "E18.11.0.5", {"position": v(-25.1, -3) * mm});
            skPoint(sketch, "E18.11.0.6", {"position": v(28.35, -3) * mm});
            skPoint(sketch, "E18.11.0.7", {"position": v(-21.65, -3) * mm});
            skPoint(sketch, "E18.11.0.8", {"position": v(-23.38, -3) * mm});
            skPoint(sketch, "E18.11.0.9", {"position": v(23.17, -3) * mm});
            skPoint(sketch, "E18.11.0.10", {"position": v(-7.86, -3) * mm});
            skPoint(sketch, "E18.11.0.11", {"position": v(-32, -3) * mm});
            skPoint(sketch, "E18.11.0.12", {"position": v(-35, -2) * mm});
            skPoint(sketch, "E18.11.0.13", {"position": v(-28.55, -3) * mm});
            skPoint(sketch, "E18.11.0.14", {"position": v(-11.3, -3) * mm});
            skPoint(sketch, "E18.11.0.15", {"position": v(-0.96, -3) * mm});
            skPoint(sketch, "E18.11.0.16", {"position": v(19.73, -3) * mm});
            skPoint(sketch, "E18.11.0.17", {"position": v(7.66, -3) * mm});
            skPoint(sketch, "E18.11.0.18", {"position": v(-14.76, -3) * mm});
            skPoint(sketch, "E18.11.0.19", {"position": v(16.28, -3) * mm});
            skPoint(sketch, "E18.11.0.20", {"position": v(5.93, -3) * mm});
            skPoint(sketch, "E18.11.0.21", {"position": v(-2.69, -3) * mm});
            skPoint(sketch, "E18.11.0.22", {"position": v(0.76, -3) * mm});
            skPoint(sketch, "E18.11.0.23", {"position": v(14.55, -3) * mm});
            skPoint(sketch, "E18.11.0.24", {"position": v(-30.28, -3) * mm});
            skPoint(sketch, "E18.11.0.25", {"position": v(24.9, -3) * mm});
            skPoint(sketch, "E18.11.0.26", {"position": v(11.1, -3) * mm});
            skPoint(sketch, "E18.11.0.27", {"position": v(-6.14, -3) * mm});
            skPoint(sketch, "E18.11.0.28", {"position": v(-18.2, -3) * mm});
            skPoint(sketch, "E18.11.0.29", {"position": v(-13.03, -3) * mm});
            skPoint(sketch, "E18.11.0.30", {"position": v(21.45, -3) * mm});
            skPoint(sketch, "E18.11.0.31", {"position": v(26.62, -3) * mm});
            skPoint(sketch, "E18.11.0.32", {"position": v(-26.83, -3) * mm});
            skPoint(sketch, "E18.11.0.33", {"position": v(-4.41, -3) * mm});
            skPoint(sketch, "E18.11.0.34", {"position": v(-19.93, -3) * mm});
            skPoint(sketch, "E18.11.0.35", {"position": v(31.8, -3) * mm});
            skPoint(sketch, "E18.11.0.36", {"position": v(-16.48, -3) * mm});
            skPoint(sketch, "E18.11.0.37", {"position": v(4.2, -3) * mm});
            skPoint(sketch, "E18.11.0.38", {"position": v(-9.59, -3) * mm});
            skPoint(sketch, "E18.11.0.39", {"position": v(2.48, -3) * mm});
            skLineSegment(sketch, "E18.11.0.40", {"start": v(-34, -3) * mm, "end": v(-32, -3) * mm});
            skPoint(sketch, "E18.12.0.0", {"position": v(18, -5) * mm});
            skPoint(sketch, "E18.12.0.1", {"position": v(30.07, -5) * mm});
            skPoint(sketch, "E18.12.0.2", {"position": v(9.38, -5) * mm});
            skPoint(sketch, "E18.12.0.3", {"position": v(12.83, -5) * mm});
            skPoint(sketch, "E18.12.0.4", {"position": v(33.52, -5) * mm});
            skPoint(sketch, "E18.12.0.5", {"position": v(-25.1, -5) * mm});
            skPoint(sketch, "E18.12.0.6", {"position": v(28.35, -5) * mm});
            skPoint(sketch, "E18.12.0.7", {"position": v(-21.65, -5) * mm});
            skPoint(sketch, "E18.12.0.8", {"position": v(-23.38, -5) * mm});
            skPoint(sketch, "E18.12.0.9", {"position": v(23.17, -5) * mm});
            skPoint(sketch, "E18.12.0.10", {"position": v(-7.86, -5) * mm});
            skPoint(sketch, "E18.12.0.11", {"position": v(-32, -5) * mm});
            skPoint(sketch, "E18.12.0.12", {"position": v(-35, -4) * mm});
            skPoint(sketch, "E18.12.0.13", {"position": v(-28.55, -5) * mm});
            skPoint(sketch, "E18.12.0.14", {"position": v(-11.3, -5) * mm});
            skPoint(sketch, "E18.12.0.15", {"position": v(-0.96, -5) * mm});
            skPoint(sketch, "E18.12.0.16", {"position": v(19.73, -5) * mm});
            skPoint(sketch, "E18.12.0.17", {"position": v(7.66, -5) * mm});
            skPoint(sketch, "E18.12.0.18", {"position": v(-14.76, -5) * mm});
            skPoint(sketch, "E18.12.0.19", {"position": v(16.28, -5) * mm});
            skPoint(sketch, "E18.12.0.20", {"position": v(5.93, -5) * mm});
            skPoint(sketch, "E18.12.0.21", {"position": v(-2.69, -5) * mm});
            skPoint(sketch, "E18.12.0.22", {"position": v(0.76, -5) * mm});
            skPoint(sketch, "E18.12.0.23", {"position": v(14.55, -5) * mm});
            skPoint(sketch, "E18.12.0.24", {"position": v(-30.28, -5) * mm});
            skPoint(sketch, "E18.12.0.25", {"position": v(24.9, -5) * mm});
            skPoint(sketch, "E18.12.0.26", {"position": v(11.1, -5) * mm});
            skPoint(sketch, "E18.12.0.27", {"position": v(-6.14, -5) * mm});
            skPoint(sketch, "E18.12.0.28", {"position": v(-18.2, -5) * mm});
            skPoint(sketch, "E18.12.0.29", {"position": v(-13.03, -5) * mm});
            skPoint(sketch, "E18.12.0.30", {"position": v(21.45, -5) * mm});
            skPoint(sketch, "E18.12.0.31", {"position": v(26.62, -5) * mm});
            skPoint(sketch, "E18.12.0.32", {"position": v(-26.83, -5) * mm});
            skPoint(sketch, "E18.12.0.33", {"position": v(-4.41, -5) * mm});
            skPoint(sketch, "E18.12.0.34", {"position": v(-19.93, -5) * mm});
            skPoint(sketch, "E18.12.0.35", {"position": v(31.8, -5) * mm});
            skPoint(sketch, "E18.12.0.36", {"position": v(-16.48, -5) * mm});
            skPoint(sketch, "E18.12.0.37", {"position": v(4.2, -5) * mm});
            skPoint(sketch, "E18.12.0.38", {"position": v(-9.59, -5) * mm});
            skPoint(sketch, "E18.12.0.39", {"position": v(2.48, -5) * mm});
            skLineSegment(sketch, "E18.12.0.40", {"start": v(-34, -5) * mm, "end": v(-32, -5) * mm});
            skPoint(sketch, "E18.13.0.0", {"position": v(18, -7) * mm});
            skPoint(sketch, "E18.13.0.1", {"position": v(30.07, -7) * mm});
            skPoint(sketch, "E18.13.0.2", {"position": v(9.38, -7) * mm});
            skPoint(sketch, "E18.13.0.3", {"position": v(12.83, -7) * mm});
            skPoint(sketch, "E18.13.0.4", {"position": v(33.52, -7) * mm});
            skPoint(sketch, "E18.13.0.5", {"position": v(-25.1, -7) * mm});
            skPoint(sketch, "E18.13.0.6", {"position": v(28.35, -7) * mm});
            skPoint(sketch, "E18.13.0.7", {"position": v(-21.65, -7) * mm});
            skPoint(sketch, "E18.13.0.8", {"position": v(-23.38, -7) * mm});
            skPoint(sketch, "E18.13.0.9", {"position": v(23.17, -7) * mm});
            skPoint(sketch, "E18.13.0.10", {"position": v(-7.86, -7) * mm});
            skPoint(sketch, "E18.13.0.11", {"position": v(-32, -7) * mm});
            skPoint(sketch, "E18.13.0.12", {"position": v(-35, -6) * mm});
            skPoint(sketch, "E18.13.0.13", {"position": v(-28.55, -7) * mm});
            skPoint(sketch, "E18.13.0.14", {"position": v(-11.3, -7) * mm});
            skPoint(sketch, "E18.13.0.15", {"position": v(-0.96, -7) * mm});
            skPoint(sketch, "E18.13.0.16", {"position": v(19.73, -7) * mm});
            skPoint(sketch, "E18.13.0.17", {"position": v(7.66, -7) * mm});
            skPoint(sketch, "E18.13.0.18", {"position": v(-14.76, -7) * mm});
            skPoint(sketch, "E18.13.0.19", {"position": v(16.28, -7) * mm});
            skPoint(sketch, "E18.13.0.20", {"position": v(5.93, -7) * mm});
            skPoint(sketch, "E18.13.0.21", {"position": v(-2.69, -7) * mm});
            skPoint(sketch, "E18.13.0.22", {"position": v(0.76, -7) * mm});
            skPoint(sketch, "E18.13.0.23", {"position": v(14.55, -7) * mm});
            skPoint(sketch, "E18.13.0.24", {"position": v(-30.28, -7) * mm});
            skPoint(sketch, "E18.13.0.25", {"position": v(24.9, -7) * mm});
            skPoint(sketch, "E18.13.0.26", {"position": v(11.1, -7) * mm});
            skPoint(sketch, "E18.13.0.27", {"position": v(-6.14, -7) * mm});
            skPoint(sketch, "E18.13.0.28", {"position": v(-18.2, -7) * mm});
            skPoint(sketch, "E18.13.0.29", {"position": v(-13.03, -7) * mm});
            skPoint(sketch, "E18.13.0.30", {"position": v(21.45, -7) * mm});
            skPoint(sketch, "E18.13.0.31", {"position": v(26.62, -7) * mm});
            skPoint(sketch, "E18.13.0.32", {"position": v(-26.83, -7) * mm});
            skPoint(sketch, "E18.13.0.33", {"position": v(-4.41, -7) * mm});
            skPoint(sketch, "E18.13.0.34", {"position": v(-19.93, -7) * mm});
            skPoint(sketch, "E18.13.0.35", {"position": v(31.8, -7) * mm});
            skPoint(sketch, "E18.13.0.36", {"position": v(-16.48, -7) * mm});
            skPoint(sketch, "E18.13.0.37", {"position": v(4.2, -7) * mm});
            skPoint(sketch, "E18.13.0.38", {"position": v(-9.59, -7) * mm});
            skPoint(sketch, "E18.13.0.39", {"position": v(2.48, -7) * mm});
            skLineSegment(sketch, "E18.13.0.40", {"start": v(-34, -7) * mm, "end": v(-32, -7) * mm});
            skPoint(sketch, "E18.14.0.0", {"position": v(18, -9) * mm});
            skPoint(sketch, "E18.14.0.1", {"position": v(30.07, -9) * mm});
            skPoint(sketch, "E18.14.0.2", {"position": v(9.38, -9) * mm});
            skPoint(sketch, "E18.14.0.3", {"position": v(12.83, -9) * mm});
            skPoint(sketch, "E18.14.0.4", {"position": v(33.52, -9) * mm});
            skPoint(sketch, "E18.14.0.5", {"position": v(-25.1, -9) * mm});
            skPoint(sketch, "E18.14.0.6", {"position": v(28.35, -9) * mm});
            skPoint(sketch, "E18.14.0.7", {"position": v(-21.65, -9) * mm});
            skPoint(sketch, "E18.14.0.8", {"position": v(-23.38, -9) * mm});
            skPoint(sketch, "E18.14.0.9", {"position": v(23.17, -9) * mm});
            skPoint(sketch, "E18.14.0.10", {"position": v(-7.86, -9) * mm});
            skPoint(sketch, "E18.14.0.11", {"position": v(-32, -9) * mm});
            skPoint(sketch, "E18.14.0.12", {"position": v(-35, -8) * mm});
            skPoint(sketch, "E18.14.0.13", {"position": v(-28.55, -9) * mm});
            skPoint(sketch, "E18.14.0.14", {"position": v(-11.3, -9) * mm});
            skPoint(sketch, "E18.14.0.15", {"position": v(-0.96, -9) * mm});
            skPoint(sketch, "E18.14.0.16", {"position": v(19.73, -9) * mm});
            skPoint(sketch, "E18.14.0.17", {"position": v(7.66, -9) * mm});
            skPoint(sketch, "E18.14.0.18", {"position": v(-14.76, -9) * mm});
            skPoint(sketch, "E18.14.0.19", {"position": v(16.28, -9) * mm});
            skPoint(sketch, "E18.14.0.20", {"position": v(5.93, -9) * mm});
            skPoint(sketch, "E18.14.0.21", {"position": v(-2.69, -9) * mm});
            skPoint(sketch, "E18.14.0.22", {"position": v(0.76, -9) * mm});
            skPoint(sketch, "E18.14.0.23", {"position": v(14.55, -9) * mm});
            skPoint(sketch, "E18.14.0.24", {"position": v(-30.28, -9) * mm});
            skPoint(sketch, "E18.14.0.25", {"position": v(24.9, -9) * mm});
            skPoint(sketch, "E18.14.0.26", {"position": v(11.1, -9) * mm});
            skPoint(sketch, "E18.14.0.27", {"position": v(-6.14, -9) * mm});
            skPoint(sketch, "E18.14.0.28", {"position": v(-18.2, -9) * mm});
            skPoint(sketch, "E18.14.0.29", {"position": v(-13.03, -9) * mm});
            skPoint(sketch, "E18.14.0.30", {"position": v(21.45, -9) * mm});
            skPoint(sketch, "E18.14.0.31", {"position": v(26.62, -9) * mm});
            skPoint(sketch, "E18.14.0.32", {"position": v(-26.83, -9) * mm});
            skPoint(sketch, "E18.14.0.33", {"position": v(-4.41, -9) * mm});
            skPoint(sketch, "E18.14.0.34", {"position": v(-19.93, -9) * mm});
            skPoint(sketch, "E18.14.0.35", {"position": v(31.8, -9) * mm});
            skPoint(sketch, "E18.14.0.36", {"position": v(-16.48, -9) * mm});
            skPoint(sketch, "E18.14.0.37", {"position": v(4.2, -9) * mm});
            skPoint(sketch, "E18.14.0.38", {"position": v(-9.59, -9) * mm});
            skPoint(sketch, "E18.14.0.39", {"position": v(2.48, -9) * mm});
            skLineSegment(sketch, "E18.14.0.40", {"start": v(-34, -9) * mm, "end": v(-32, -9) * mm});
            skPoint(sketch, "E18.15.0.0", {"position": v(18, -11) * mm});
            skPoint(sketch, "E18.15.0.1", {"position": v(30.07, -11) * mm});
            skPoint(sketch, "E18.15.0.2", {"position": v(9.38, -11) * mm});
            skPoint(sketch, "E18.15.0.3", {"position": v(12.83, -11) * mm});
            skPoint(sketch, "E18.15.0.4", {"position": v(33.52, -11) * mm});
            skPoint(sketch, "E18.15.0.5", {"position": v(-25.1, -11) * mm});
            skPoint(sketch, "E18.15.0.6", {"position": v(28.35, -11) * mm});
            skPoint(sketch, "E18.15.0.7", {"position": v(-21.65, -11) * mm});
            skPoint(sketch, "E18.15.0.8", {"position": v(-23.38, -11) * mm});
            skPoint(sketch, "E18.15.0.9", {"position": v(23.17, -11) * mm});
            skPoint(sketch, "E18.15.0.10", {"position": v(-7.86, -11) * mm});
            skPoint(sketch, "E18.15.0.11", {"position": v(-32, -11) * mm});
            skPoint(sketch, "E18.15.0.12", {"position": v(-35, -10) * mm});
            skPoint(sketch, "E18.15.0.13", {"position": v(-28.55, -11) * mm});
            skPoint(sketch, "E18.15.0.14", {"position": v(-11.3, -11) * mm});
            skPoint(sketch, "E18.15.0.15", {"position": v(-0.96, -11) * mm});
            skPoint(sketch, "E18.15.0.16", {"position": v(19.73, -11) * mm});
            skPoint(sketch, "E18.15.0.17", {"position": v(7.66, -11) * mm});
            skPoint(sketch, "E18.15.0.18", {"position": v(-14.76, -11) * mm});
            skPoint(sketch, "E18.15.0.19", {"position": v(16.28, -11) * mm});
            skPoint(sketch, "E18.15.0.20", {"position": v(5.93, -11) * mm});
            skPoint(sketch, "E18.15.0.21", {"position": v(-2.69, -11) * mm});
            skPoint(sketch, "E18.15.0.22", {"position": v(0.76, -11) * mm});
            skPoint(sketch, "E18.15.0.23", {"position": v(14.55, -11) * mm});
            skPoint(sketch, "E18.15.0.24", {"position": v(-30.28, -11) * mm});
            skPoint(sketch, "E18.15.0.25", {"position": v(24.9, -11) * mm});
            skPoint(sketch, "E18.15.0.26", {"position": v(11.1, -11) * mm});
            skPoint(sketch, "E18.15.0.27", {"position": v(-6.14, -11) * mm});
            skPoint(sketch, "E18.15.0.28", {"position": v(-18.2, -11) * mm});
            skPoint(sketch, "E18.15.0.29", {"position": v(-13.03, -11) * mm});
            skPoint(sketch, "E18.15.0.30", {"position": v(21.45, -11) * mm});
            skPoint(sketch, "E18.15.0.31", {"position": v(26.62, -11) * mm});
            skPoint(sketch, "E18.15.0.32", {"position": v(-26.83, -11) * mm});
            skPoint(sketch, "E18.15.0.33", {"position": v(-4.41, -11) * mm});
            skPoint(sketch, "E18.15.0.34", {"position": v(-19.93, -11) * mm});
            skPoint(sketch, "E18.15.0.35", {"position": v(31.8, -11) * mm});
            skPoint(sketch, "E18.15.0.36", {"position": v(-16.48, -11) * mm});
            skPoint(sketch, "E18.15.0.37", {"position": v(4.2, -11) * mm});
            skPoint(sketch, "E18.15.0.38", {"position": v(-9.59, -11) * mm});
            skPoint(sketch, "E18.15.0.39", {"position": v(2.48, -11) * mm});
            skLineSegment(sketch, "E18.15.0.40", {"start": v(-34, -11) * mm, "end": v(-32, -11) * mm});
            skPoint(sketch, "E18.16.0.0", {"position": v(18, -13) * mm});
            skPoint(sketch, "E18.16.0.1", {"position": v(30.07, -13) * mm});
            skPoint(sketch, "E18.16.0.2", {"position": v(9.38, -13) * mm});
            skPoint(sketch, "E18.16.0.3", {"position": v(12.83, -13) * mm});
            skPoint(sketch, "E18.16.0.4", {"position": v(33.52, -13) * mm});
            skPoint(sketch, "E18.16.0.5", {"position": v(-25.1, -13) * mm});
            skPoint(sketch, "E18.16.0.6", {"position": v(28.35, -13) * mm});
            skPoint(sketch, "E18.16.0.7", {"position": v(-21.65, -13) * mm});
            skPoint(sketch, "E18.16.0.8", {"position": v(-23.38, -13) * mm});
            skPoint(sketch, "E18.16.0.9", {"position": v(23.17, -13) * mm});
            skPoint(sketch, "E18.16.0.10", {"position": v(-7.86, -13) * mm});
            skPoint(sketch, "E18.16.0.11", {"position": v(-32, -13) * mm});
            skPoint(sketch, "E18.16.0.12", {"position": v(-35, -12) * mm});
            skPoint(sketch, "E18.16.0.13", {"position": v(-28.55, -13) * mm});
            skPoint(sketch, "E18.16.0.14", {"position": v(-11.3, -13) * mm});
            skPoint(sketch, "E18.16.0.15", {"position": v(-0.96, -13) * mm});
            skPoint(sketch, "E18.16.0.16", {"position": v(19.73, -13) * mm});
            skPoint(sketch, "E18.16.0.17", {"position": v(7.66, -13) * mm});
            skPoint(sketch, "E18.16.0.18", {"position": v(-14.76, -13) * mm});
            skPoint(sketch, "E18.16.0.19", {"position": v(16.28, -13) * mm});
            skPoint(sketch, "E18.16.0.20", {"position": v(5.93, -13) * mm});
            skPoint(sketch, "E18.16.0.21", {"position": v(-2.69, -13) * mm});
            skPoint(sketch, "E18.16.0.22", {"position": v(0.76, -13) * mm});
            skPoint(sketch, "E18.16.0.23", {"position": v(14.55, -13) * mm});
            skPoint(sketch, "E18.16.0.24", {"position": v(-30.28, -13) * mm});
            skPoint(sketch, "E18.16.0.25", {"position": v(24.9, -13) * mm});
            skPoint(sketch, "E18.16.0.26", {"position": v(11.1, -13) * mm});
            skPoint(sketch, "E18.16.0.27", {"position": v(-6.14, -13) * mm});
            skPoint(sketch, "E18.16.0.28", {"position": v(-18.2, -13) * mm});
            skPoint(sketch, "E18.16.0.29", {"position": v(-13.03, -13) * mm});
            skPoint(sketch, "E18.16.0.30", {"position": v(21.45, -13) * mm});
            skPoint(sketch, "E18.16.0.31", {"position": v(26.62, -13) * mm});
            skPoint(sketch, "E18.16.0.32", {"position": v(-26.83, -13) * mm});
            skPoint(sketch, "E18.16.0.33", {"position": v(-4.41, -13) * mm});
            skPoint(sketch, "E18.16.0.34", {"position": v(-19.93, -13) * mm});
            skPoint(sketch, "E18.16.0.35", {"position": v(31.8, -13) * mm});
            skPoint(sketch, "E18.16.0.36", {"position": v(-16.48, -13) * mm});
            skPoint(sketch, "E18.16.0.37", {"position": v(4.2, -13) * mm});
            skPoint(sketch, "E18.16.0.38", {"position": v(-9.59, -13) * mm});
            skPoint(sketch, "E18.16.0.39", {"position": v(2.48, -13) * mm});
            skLineSegment(sketch, "E18.16.0.40", {"start": v(-34, -13) * mm, "end": v(-32, -13) * mm});
            skPoint(sketch, "E18.17.0.0", {"position": v(18, -15) * mm});
            skPoint(sketch, "E18.17.0.1", {"position": v(30.07, -15) * mm});
            skPoint(sketch, "E18.17.0.2", {"position": v(9.38, -15) * mm});
            skPoint(sketch, "E18.17.0.3", {"position": v(12.83, -15) * mm});
            skPoint(sketch, "E18.17.0.4", {"position": v(33.52, -15) * mm});
            skPoint(sketch, "E18.17.0.5", {"position": v(-25.1, -15) * mm});
            skPoint(sketch, "E18.17.0.6", {"position": v(28.35, -15) * mm});
            skPoint(sketch, "E18.17.0.7", {"position": v(-21.65, -15) * mm});
            skPoint(sketch, "E18.17.0.8", {"position": v(-23.38, -15) * mm});
            skPoint(sketch, "E18.17.0.9", {"position": v(23.17, -15) * mm});
            skPoint(sketch, "E18.17.0.10", {"position": v(-7.86, -15) * mm});
            skPoint(sketch, "E18.17.0.11", {"position": v(-32, -15) * mm});
            skPoint(sketch, "E18.17.0.12", {"position": v(-35, -14) * mm});
            skPoint(sketch, "E18.17.0.13", {"position": v(-28.55, -15) * mm});
            skPoint(sketch, "E18.17.0.14", {"position": v(-11.3, -15) * mm});
            skPoint(sketch, "E18.17.0.15", {"position": v(-0.96, -15) * mm});
            skPoint(sketch, "E18.17.0.16", {"position": v(19.73, -15) * mm});
            skPoint(sketch, "E18.17.0.17", {"position": v(7.66, -15) * mm});
            skPoint(sketch, "E18.17.0.18", {"position": v(-14.76, -15) * mm});
            skPoint(sketch, "E18.17.0.19", {"position": v(16.28, -15) * mm});
            skPoint(sketch, "E18.17.0.20", {"position": v(5.93, -15) * mm});
            skPoint(sketch, "E18.17.0.21", {"position": v(-2.69, -15) * mm});
            skPoint(sketch, "E18.17.0.22", {"position": v(0.76, -15) * mm});
            skPoint(sketch, "E18.17.0.23", {"position": v(14.55, -15) * mm});
            skPoint(sketch, "E18.17.0.24", {"position": v(-30.28, -15) * mm});
            skPoint(sketch, "E18.17.0.25", {"position": v(24.9, -15) * mm});
            skPoint(sketch, "E18.17.0.26", {"position": v(11.1, -15) * mm});
            skPoint(sketch, "E18.17.0.27", {"position": v(-6.14, -15) * mm});
            skPoint(sketch, "E18.17.0.28", {"position": v(-18.2, -15) * mm});
            skPoint(sketch, "E18.17.0.29", {"position": v(-13.03, -15) * mm});
            skPoint(sketch, "E18.17.0.30", {"position": v(21.45, -15) * mm});
            skPoint(sketch, "E18.17.0.31", {"position": v(26.62, -15) * mm});
            skPoint(sketch, "E18.17.0.32", {"position": v(-26.83, -15) * mm});
            skPoint(sketch, "E18.17.0.33", {"position": v(-4.41, -15) * mm});
            skPoint(sketch, "E18.17.0.34", {"position": v(-19.93, -15) * mm});
            skPoint(sketch, "E18.17.0.35", {"position": v(31.8, -15) * mm});
            skPoint(sketch, "E18.17.0.36", {"position": v(-16.48, -15) * mm});
            skPoint(sketch, "E18.17.0.37", {"position": v(4.2, -15) * mm});
            skPoint(sketch, "E18.17.0.38", {"position": v(-9.59, -15) * mm});
            skPoint(sketch, "E18.17.0.39", {"position": v(2.48, -15) * mm});
            skLineSegment(sketch, "E18.17.0.40", {"start": v(-34, -15) * mm, "end": v(-32, -15) * mm});
            skPoint(sketch, "E18.18.0.0", {"position": v(18, -17) * mm});
            skPoint(sketch, "E18.18.0.1", {"position": v(30.07, -17) * mm});
            skPoint(sketch, "E18.18.0.2", {"position": v(9.38, -17) * mm});
            skPoint(sketch, "E18.18.0.3", {"position": v(12.83, -17) * mm});
            skPoint(sketch, "E18.18.0.4", {"position": v(33.52, -17) * mm});
            skPoint(sketch, "E18.18.0.5", {"position": v(-25.1, -17) * mm});
            skPoint(sketch, "E18.18.0.6", {"position": v(28.35, -17) * mm});
            skPoint(sketch, "E18.18.0.7", {"position": v(-21.65, -17) * mm});
            skPoint(sketch, "E18.18.0.8", {"position": v(-23.38, -17) * mm});
            skPoint(sketch, "E18.18.0.9", {"position": v(23.17, -17) * mm});
            skPoint(sketch, "E18.18.0.10", {"position": v(-7.86, -17) * mm});
            skPoint(sketch, "E18.18.0.11", {"position": v(-32, -17) * mm});
            skPoint(sketch, "E18.18.0.12", {"position": v(-35, -16) * mm});
            skPoint(sketch, "E18.18.0.13", {"position": v(-28.55, -17) * mm});
            skPoint(sketch, "E18.18.0.14", {"position": v(-11.3, -17) * mm});
            skPoint(sketch, "E18.18.0.15", {"position": v(-0.96, -17) * mm});
            skPoint(sketch, "E18.18.0.16", {"position": v(19.73, -17) * mm});
            skPoint(sketch, "E18.18.0.17", {"position": v(7.66, -17) * mm});
            skPoint(sketch, "E18.18.0.18", {"position": v(-14.76, -17) * mm});
            skPoint(sketch, "E18.18.0.19", {"position": v(16.28, -17) * mm});
            skPoint(sketch, "E18.18.0.20", {"position": v(5.93, -17) * mm});
            skPoint(sketch, "E18.18.0.21", {"position": v(-2.69, -17) * mm});
            skPoint(sketch, "E18.18.0.22", {"position": v(0.76, -17) * mm});
            skPoint(sketch, "E18.18.0.23", {"position": v(14.55, -17) * mm});
            skPoint(sketch, "E18.18.0.24", {"position": v(-30.28, -17) * mm});
            skPoint(sketch, "E18.18.0.25", {"position": v(24.9, -17) * mm});
            skPoint(sketch, "E18.18.0.26", {"position": v(11.1, -17) * mm});
            skPoint(sketch, "E18.18.0.27", {"position": v(-6.14, -17) * mm});
            skPoint(sketch, "E18.18.0.28", {"position": v(-18.2, -17) * mm});
            skPoint(sketch, "E18.18.0.29", {"position": v(-13.03, -17) * mm});
            skPoint(sketch, "E18.18.0.30", {"position": v(21.45, -17) * mm});
            skPoint(sketch, "E18.18.0.31", {"position": v(26.62, -17) * mm});
            skPoint(sketch, "E18.18.0.32", {"position": v(-26.83, -17) * mm});
            skPoint(sketch, "E18.18.0.33", {"position": v(-4.41, -17) * mm});
            skPoint(sketch, "E18.18.0.34", {"position": v(-19.93, -17) * mm});
            skPoint(sketch, "E18.18.0.35", {"position": v(31.8, -17) * mm});
            skPoint(sketch, "E18.18.0.36", {"position": v(-16.48, -17) * mm});
            skPoint(sketch, "E18.18.0.37", {"position": v(4.2, -17) * mm});
            skPoint(sketch, "E18.18.0.38", {"position": v(-9.59, -17) * mm});
            skPoint(sketch, "E18.18.0.39", {"position": v(2.48, -17) * mm});
            skLineSegment(sketch, "E18.18.0.40", {"start": v(-34, -17) * mm, "end": v(-32, -17) * mm});
            skPoint(sketch, "E18.19.0.0", {"position": v(18, -19) * mm});
            skPoint(sketch, "E18.19.0.1", {"position": v(30.07, -19) * mm});
            skPoint(sketch, "E18.19.0.2", {"position": v(9.38, -19) * mm});
            skPoint(sketch, "E18.19.0.3", {"position": v(12.83, -19) * mm});
            skPoint(sketch, "E18.19.0.4", {"position": v(33.52, -19) * mm});
            skPoint(sketch, "E18.19.0.5", {"position": v(-25.1, -19) * mm});
            skPoint(sketch, "E18.19.0.6", {"position": v(28.35, -19) * mm});
            skPoint(sketch, "E18.19.0.7", {"position": v(-21.65, -19) * mm});
            skPoint(sketch, "E18.19.0.8", {"position": v(-23.38, -19) * mm});
            skPoint(sketch, "E18.19.0.9", {"position": v(23.17, -19) * mm});
            skPoint(sketch, "E18.19.0.10", {"position": v(-7.86, -19) * mm});
            skPoint(sketch, "E18.19.0.11", {"position": v(-32, -19) * mm});
            skPoint(sketch, "E18.19.0.12", {"position": v(-35, -18) * mm});
            skPoint(sketch, "E18.19.0.13", {"position": v(-28.55, -19) * mm});
            skPoint(sketch, "E18.19.0.14", {"position": v(-11.3, -19) * mm});
            skPoint(sketch, "E18.19.0.15", {"position": v(-0.96, -19) * mm});
            skPoint(sketch, "E18.19.0.16", {"position": v(19.73, -19) * mm});
            skPoint(sketch, "E18.19.0.17", {"position": v(7.66, -19) * mm});
            skPoint(sketch, "E18.19.0.18", {"position": v(-14.76, -19) * mm});
            skPoint(sketch, "E18.19.0.19", {"position": v(16.28, -19) * mm});
            skPoint(sketch, "E18.19.0.20", {"position": v(5.93, -19) * mm});
            skPoint(sketch, "E18.19.0.21", {"position": v(-2.69, -19) * mm});
            skPoint(sketch, "E18.19.0.22", {"position": v(0.76, -19) * mm});
            skPoint(sketch, "E18.19.0.23", {"position": v(14.55, -19) * mm});
            skPoint(sketch, "E18.19.0.24", {"position": v(-30.28, -19) * mm});
            skPoint(sketch, "E18.19.0.25", {"position": v(24.9, -19) * mm});
            skPoint(sketch, "E18.19.0.26", {"position": v(11.1, -19) * mm});
            skPoint(sketch, "E18.19.0.27", {"position": v(-6.14, -19) * mm});
            skPoint(sketch, "E18.19.0.28", {"position": v(-18.2, -19) * mm});
            skPoint(sketch, "E18.19.0.29", {"position": v(-13.03, -19) * mm});
            skPoint(sketch, "E18.19.0.30", {"position": v(21.45, -19) * mm});
            skPoint(sketch, "E18.19.0.31", {"position": v(26.62, -19) * mm});
            skPoint(sketch, "E18.19.0.32", {"position": v(-26.83, -19) * mm});
            skPoint(sketch, "E18.19.0.33", {"position": v(-4.41, -19) * mm});
            skPoint(sketch, "E18.19.0.34", {"position": v(-19.93, -19) * mm});
            skPoint(sketch, "E18.19.0.35", {"position": v(31.8, -19) * mm});
            skPoint(sketch, "E18.19.0.36", {"position": v(-16.48, -19) * mm});
            skPoint(sketch, "E18.19.0.37", {"position": v(4.2, -19) * mm});
            skPoint(sketch, "E18.19.0.38", {"position": v(-9.59, -19) * mm});
            skPoint(sketch, "E18.19.0.39", {"position": v(2.48, -19) * mm});
            skLineSegment(sketch, "E18.19.0.40", {"start": v(-34, -19) * mm, "end": v(-32, -19) * mm});
            skLineSegment(sketch, "E18.direction1", {"start": v(-32, 19) * mm, "end": v(-32, 17) * mm, "construction": true});
            skSolve(sketch);
        }
        {
            var Q0;
            Q0=sQuery(id+"F3.wireOp",VERTEX,"E18.2.0.38");
            var Q1;
            Q1=sQuery(id+"F3.wireOp",VERTEX,"E18.4.0.24");
            var Q2;
            Q2=sQuery(id+"F3.wireOp",VERTEX,"E18.4.0.32");
            var Q3;
            Q3=sQuery(id+"F3.wireOp",VERTEX,"E18.2.0.32");
            var Q4;
            Q4=sQuery(id+"F3.wireOp",VERTEX,"E18.3.0.8");
            var Q5;
            Q5=sQuery(id+"F3.wireOp",VERTEX,"E18.2.0.7");
            var Q6;
            Q6=sQuery(id+"F3.wireOp",VERTEX,"E15.0.6.0");
            var Q7;
            Q7=sQuery(id+"F3.wireOp",VERTEX,"E18.3.0.40.start");
            var Q8;
            Q8=sQuery(id+"F3.wireOp",VERTEX,"E18.1.0.14");
            var Q9;
            Q9=sQuery(id+"F3.wireOp",VERTEX,"E16.0.10.0");
            var Q10;
            Q10=sQuery(id+"F3.wireOp",VERTEX,"E18.1.0.34");
            var Q11;
            Q11=sQuery(id+"F3.wireOp",VERTEX,"E18.1.0.21");
            var Q12;
            Q12=sQuery(id+"F3.wireOp",VERTEX,"E18.3.0.21");
            var Q13;
            Q13=sQuery(id+"F3.wireOp",VERTEX,"E18.3.0.5");
            var Q14;
            Q14=sQuery(id+"F3.wireOp",VERTEX,"E16.0.13.0");
            var Q15;
            Q15=sQuery(id+"F3.wireOp",VERTEX,"E18.2.0.10");
            var Q16;
            Q16=sQuery(id+"F3.wireOp",VERTEX,"E15.0.9.0");
            var Q17;
            Q17=sQuery(id+"F3.wireOp",VERTEX,"E18.3.0.14");
            var Q18;
            Q18=sQuery(id+"F3.wireOp",VERTEX,"E18.3.0.28");
            var Q19;
            Q19=sQuery(id+"F3.wireOp",VERTEX,"E18.3.0.10");
            var Q20;
            Q20=sQuery(id+"F3.wireOp",VERTEX,"E18.2.0.18");
            var Q21;
            Q21=sQuery(id+"F3.wireOp",VERTEX,"E18.3.0.24");
            var Q22;
            Q22=sQuery(id+"F3.wireOp",VERTEX,"E18.1.0.5");
            var Q23;
            Q23=sQuery(id+"F3.wireOp",VERTEX,"E18.1.0.18");
            var Q24;
            Q24=sQuery(id+"F3.wireOp",VERTEX,"E15.0.7.0");
            var Q25;
            Q25=sQuery(id+"F3.wireOp",VERTEX,"E18.1.0.15");
            var Q26;
            Q26=sQuery(id+"F3.wireOp",VERTEX,"E16.0.18.0");
            var Q27;
            Q27=sQuery(id+"F3.wireOp",VERTEX,"E18.2.0.24");
            var Q28;
            Q28=sQuery(id+"F3.wireOp",VERTEX,"E18.4.0.34");
            var Q29;
            Q29=sQuery(id+"F3.wireOp",VERTEX,"E18.1.0.11");
            var Q30;
            Q30=sQuery(id+"F3.wireOp",VERTEX,"E18.2.0.13");
            var Q31;
            Q31=sQuery(id+"F3.wireOp",VERTEX,"E18.4.0.5");
            var Q32;
            Q32=sQuery(id+"F3.wireOp",VERTEX,"E18.4.0.15");
            var Q33;
            Q33=sQuery(id+"F3.wireOp",VERTEX,"E15.0.8.0");
            var Q34;
            Q34=sQuery(id+"F3.wireOp",VERTEX,"E16.0.15.0");
            var Q35;
            Q35=sQuery(id+"F3.wireOp",VERTEX,"E18.4.0.11");
            var Q36;
            Q36=sQuery(id+"F3.wireOp",VERTEX,"E18.2.0.5");
            var Q37;
            Q37=sQuery(id+"F3.wireOp",VERTEX,"E16.0.16.0");
            var Q38;
            Q38=sQuery(id+"F3.wireOp",VERTEX,"E18.3.0.34");
            var Q39;
            Q39=sQuery(id+"F3.wireOp",VERTEX,"E18.4.0.38");
            var Q40;
            Q40=sQuery(id+"F3.wireOp",VERTEX,"E18.4.0.14");
            var Q41;
            Q41=sQuery(id+"F3.wireOp",VERTEX,"E16.0.19.0");
            var Q42;
            Q42=sQuery(id+"F3.wireOp",VERTEX,"E18.1.0.36");
            var Q43;
            Q43=sQuery(id+"F3.wireOp",VERTEX,"E16.0.12.0");
            var Q44;
            Q44=sQuery(id+"F3.wireOp",VERTEX,"E18.3.0.32");
            var Q45;
            Q45=sQuery(id+"F3.wireOp",VERTEX,"E13.2.0.0");
            var Q46;
            Q46=sQuery(id+"F3.wireOp",VERTEX,"E13.direction1.start");
            var Q47;
            Q47=sQuery(id+"F3.wireOp",VERTEX,"E18.1.0.32");
            var Q48;
            Q48=sQuery(id+"F3.wireOp",VERTEX,"E18.2.0.8");
            var Q49;
            Q49=sQuery(id+"F3.wireOp",VERTEX,"E18.2.0.40.start");
            var Q50;
            Q50=sQuery(id+"F3.wireOp",VERTEX,"E18.2.0.21");
            var Q51;
            Q51=sQuery(id+"F3.wireOp",VERTEX,"E18.3.0.29");
            var Q52;
            Q52=sQuery(id+"F3.wireOp",VERTEX,"E18.4.0.29");
            var Q53;
            Q53=sQuery(id+"F3.wireOp",VERTEX,"E18.3.0.11");
            var Q54;
            Q54=sQuery(id+"F3.wireOp",VERTEX,"E18.1.0.27");
            var Q55;
            Q55=sQuery(id+"F3.wireOp",VERTEX,"E18.3.0.33");
            var Q56;
            Q56=sQuery(id+"F3.wireOp",VERTEX,"E18.4.0.28");
            var Q57;
            Q57=sQuery(id+"F3.wireOp",VERTEX,"E18.3.0.7");
            var Q58;
            Q58=sQuery(id+"F3.wireOp",VERTEX,"E18.1.0.7");
            var Q59;
            Q59=sQuery(id+"F3.wireOp",VERTEX,"E18.2.0.34");
            var Q60;
            Q60=sQuery(id+"F3.wireOp",VERTEX,"E18.4.0.18");
            var Q61;
            Q61=sQuery(id+"F3.wireOp",VERTEX,"E18.1.0.10");
            var Q62;
            Q62=sQuery(id+"F3.wireOp",VERTEX,"E18.1.0.13");
            var Q63;
            Q63=sQuery(id+"F3.wireOp",VERTEX,"E15.0.5.0");
            var Q64;
            Q64=sQuery(id+"F3.wireOp",VERTEX,"E18.4.0.21");
            var Q65;
            Q65=sQuery(id+"F3.wireOp",VERTEX,"E18.4.0.27");
            var Q66;
            Q66=sQuery(id+"F3.wireOp",VERTEX,"E18.2.0.27");
            var Q67;
            Q67=sQuery(id+"F3.wireOp",VERTEX,"E18.4.0.10");
            var Q68;
            Q68=sQuery(id+"F3.wireOp",VERTEX,"E18.4.0.7");
            var Q69;
            Q69=sQuery(id+"F3.wireOp",VERTEX,"E16.0.17.0");
            var Q70;
            Q70=sQuery(id+"F3.wireOp",VERTEX,"E16.0.14.0");
            var Q71;
            Q71=sQuery(id+"F3.wireOp",VERTEX,"E18.3.0.38");
            var Q72;
            Q72=sQuery(id+"F3.wireOp",VERTEX,"E18.2.0.28");
            var Q73;
            Q73=sQuery(id+"F3.wireOp",VERTEX,"E18.3.0.36");
            var Q74;
            Q74=sQuery(id+"F3.wireOp",VERTEX,"E18.3.0.18");
            var Q75;
            Q75=sQuery(id+"F3.wireOp",VERTEX,"E18.1.0.33");
            var Q76;
            Q76=sQuery(id+"F3.wireOp",VERTEX,"E18.4.0.8");
            var Q77;
            Q77=sQuery(id+"F3.wireOp",VERTEX,"E18.3.0.15");
            var Q78;
            Q78=sQuery(id+"F3.wireOp",VERTEX,"E18.3.0.13");
            var Q79;
            Q79=sQuery(id+"F3.wireOp",VERTEX,"E18.1.0.29");
            var Q80;
            Q80=sQuery(id+"F3.wireOp",VERTEX,"E18.2.0.11");
            var Q81;
            Q81=sQuery(id+"F3.wireOp",VERTEX,"E16.0.11.0");
            var Q82;
            Q82=sQuery(id+"F3.wireOp",VERTEX,"E18.4.0.36");
            var Q83;
            Q83=sQuery(id+"F3.wireOp",VERTEX,"E18.2.0.36");
            var Q84;
            Q84=sQuery(id+"F3.wireOp",VERTEX,"E18.1.0.28");
            var Q85;
            Q85=sQuery(id+"F3.wireOp",VERTEX,"E14.0.4.0");
            var Q86;
            Q86=sQuery(id+"F3.wireOp",VERTEX,"E14.0.3.0");
            var Q87;
            Q87=sQuery(id+"F3.wireOp",VERTEX,"E18.3.0.27");
            var Q88;
            Q88=sQuery(id+"F3.wireOp",VERTEX,"E18.4.0.33");
            var Q89;
            Q89=sQuery(id+"F3.wireOp",VERTEX,"E18.2.0.33");
            var Q90;
            Q90=sQuery(id+"F3.wireOp",VERTEX,"E18.1.0.8");
            var Q91;
            Q91=sQuery(id+"F3.wireOp",VERTEX,"E18.1.0.24");
            var Q92;
            Q92=sQuery(id+"F3.wireOp",VERTEX,"E18.2.0.15");
            var Q93;
            Q93=sQuery(id+"F3.wireOp",VERTEX,"E18.1.0.38");
            var Q94;
            Q94=sQuery(id+"F3.wireOp",VERTEX,"E18.2.0.14");
            var Q95;
            Q95=sQuery(id+"F3.wireOp",VERTEX,"E18.4.0.40.start");
            var Q96;
            Q96=sQuery(id+"F3.wireOp",VERTEX,"E18.4.0.13");
            var Q97;
            Q97=sQuery(id+"F3.wireOp",VERTEX,"E18.2.0.29");
            var Q98;
            Q98=sQuery(id+"F3.wireOp",VERTEX,"E18.1.0.40.start");
            var Q99;
            Q99=sQuery(id+"F3.wireOp",VERTEX,"E13.1.0.0");
            var Q100;
            Q100=sQuery(id+"F3.wireOp",VERTEX,"E13.2.0.0");
            var Q101;
            Q101=sQuery(id+"F3.wireOp",VERTEX,"E13.1.0.0");
            var Q102;
            Q102=makeQuery(id+"F1.opExtrude","SWEPT_BODY",BODY,{"disambiguationData":[OSD([sQuery(id+"F0.wireOp",EDGE,"E0.bottom"),sQuery(id+"F0.wireOp",EDGE,"E0.top"),sQuery(id+"F0.wireOp",EDGE,"E0.left"),sQuery(id+"F0.wireOp",EDGE,"E0.right"),sQuery(id+"F0.wireOp",EDGE,"E1"),sQuery(id+"F0.wireOp",EDGE,"E2"),sQuery(id+"F0.wireOp",EDGE,"E3"),sQuery(id+"F0.wireOp",EDGE,"E4")])]});
            hole(context, id + "F4", {"style" : HoleStyle.SIMPLE, "endStyle" : HoleEndStyle.BLIND, "holeDiameter" : 1 * mm, "majorDiameter" : 5 * mm, "holeDepth" : 3 * mm, "isTappedThrough" : true, "tappedDepth" : 12 * mm, "tapClearance" : 3, "locations" : qUnion([Q0, Q1, Q2, Q3, Q4, Q5, Q6, Q7, Q8, Q9, Q10, Q11, Q12, Q13, Q14, Q15, Q16, Q17, Q18, Q19, Q20, Q21, Q22, Q23, Q24, Q25, Q26, Q27, Q28, Q29, Q30, Q31, Q32, Q33, Q34, Q35, Q36, Q37, Q38, Q39, Q40, Q41, Q42, Q43, Q44, Q45, Q46, Q47, Q48, Q49, Q50, Q51, Q52, Q53, Q54, Q55, Q56, Q57, Q58, Q59, Q60, Q61, Q62, Q63, Q64, Q65, Q66, Q67, Q68, Q69, Q70, Q71, Q72, Q73, Q74, Q75, Q76, Q77, Q78, Q79, Q80, Q81, Q82, Q83, Q84, Q85, Q86, Q87, Q88, Q89, Q90, Q91, Q92, Q93, Q94, Q95, Q96, Q97, Q98, Q99, Q100, Q101]), "scope" : qUnion([Q102])});
        }
        {
            var Q0;
            Q0=sQuery(id+"F3.wireOp",VERTEX,"E18.5.0.29");
            var Q1;
            Q1=sQuery(id+"F3.wireOp",VERTEX,"E18.7.0.21");
            var Q2;
            Q2=sQuery(id+"F3.wireOp",VERTEX,"E18.6.0.27");
            var Q3;
            Q3=sQuery(id+"F3.wireOp",VERTEX,"E18.6.0.11");
            var Q4;
            Q4=sQuery(id+"F3.wireOp",VERTEX,"E18.5.0.13");
            var Q5;
            Q5=sQuery(id+"F3.wireOp",VERTEX,"E18.7.0.33");
            var Q6;
            Q6=sQuery(id+"F3.wireOp",VERTEX,"E18.7.0.29");
            var Q7;
            Q7=sQuery(id+"F3.wireOp",VERTEX,"E18.5.0.27");
            var Q8;
            Q8=sQuery(id+"F3.wireOp",VERTEX,"E18.5.0.40.start");
            var Q9;
            Q9=sQuery(id+"F3.wireOp",VERTEX,"E18.7.0.15");
            var Q10;
            Q10=sQuery(id+"F3.wireOp",VERTEX,"E18.5.0.24");
            var Q11;
            Q11=sQuery(id+"F3.wireOp",VERTEX,"E18.6.0.33");
            var Q12;
            Q12=sQuery(id+"F3.wireOp",VERTEX,"E18.6.0.5");
            var Q13;
            Q13=sQuery(id+"F3.wireOp",VERTEX,"E18.7.0.38");
            var Q14;
            Q14=sQuery(id+"F3.wireOp",VERTEX,"E18.7.0.36");
            var Q15;
            Q15=sQuery(id+"F3.wireOp",VERTEX,"E18.6.0.18");
            var Q16;
            Q16=sQuery(id+"F3.wireOp",VERTEX,"E18.5.0.11");
            var Q17;
            Q17=sQuery(id+"F3.wireOp",VERTEX,"E18.7.0.34");
            var Q18;
            Q18=sQuery(id+"F3.wireOp",VERTEX,"E18.5.0.8");
            var Q19;
            Q19=sQuery(id+"F3.wireOp",VERTEX,"E18.6.0.21");
            var Q20;
            Q20=sQuery(id+"F3.wireOp",VERTEX,"E18.5.0.32");
            var Q21;
            Q21=sQuery(id+"F3.wireOp",VERTEX,"E18.6.0.40.start");
            var Q22;
            Q22=sQuery(id+"F3.wireOp",VERTEX,"E18.7.0.32");
            var Q23;
            Q23=sQuery(id+"F3.wireOp",VERTEX,"E18.5.0.21");
            var Q24;
            Q24=sQuery(id+"F3.wireOp",VERTEX,"E18.7.0.5");
            var Q25;
            Q25=sQuery(id+"F3.wireOp",VERTEX,"E18.6.0.29");
            var Q26;
            Q26=sQuery(id+"F3.wireOp",VERTEX,"E18.5.0.28");
            var Q27;
            Q27=sQuery(id+"F3.wireOp",VERTEX,"E18.6.0.13");
            var Q28;
            Q28=sQuery(id+"F3.wireOp",VERTEX,"E18.6.0.7");
            var Q29;
            Q29=sQuery(id+"F3.wireOp",VERTEX,"E18.5.0.33");
            var Q30;
            Q30=sQuery(id+"F3.wireOp",VERTEX,"E18.5.0.18");
            var Q31;
            Q31=sQuery(id+"F3.wireOp",VERTEX,"E18.5.0.34");
            var Q32;
            Q32=sQuery(id+"F3.wireOp",VERTEX,"E18.6.0.28");
            var Q33;
            Q33=sQuery(id+"F3.wireOp",VERTEX,"E18.7.0.13");
            var Q34;
            Q34=sQuery(id+"F3.wireOp",VERTEX,"E18.6.0.10");
            var Q35;
            Q35=sQuery(id+"F3.wireOp",VERTEX,"E18.5.0.15");
            var Q36;
            Q36=sQuery(id+"F3.wireOp",VERTEX,"E18.7.0.28");
            var Q37;
            Q37=sQuery(id+"F3.wireOp",VERTEX,"E18.6.0.8");
            var Q38;
            Q38=sQuery(id+"F3.wireOp",VERTEX,"E18.6.0.24");
            var Q39;
            Q39=sQuery(id+"F3.wireOp",VERTEX,"E18.7.0.40.start");
            var Q40;
            Q40=sQuery(id+"F3.wireOp",VERTEX,"E18.6.0.36");
            var Q41;
            Q41=sQuery(id+"F3.wireOp",VERTEX,"E18.7.0.11");
            var Q42;
            Q42=sQuery(id+"F3.wireOp",VERTEX,"E18.7.0.27");
            var Q43;
            Q43=sQuery(id+"F3.wireOp",VERTEX,"E18.7.0.24");
            var Q44;
            Q44=sQuery(id+"F3.wireOp",VERTEX,"E18.6.0.32");
            var Q45;
            Q45=sQuery(id+"F3.wireOp",VERTEX,"E18.7.0.8");
            var Q46;
            Q46=sQuery(id+"F3.wireOp",VERTEX,"E18.6.0.15");
            var Q47;
            Q47=sQuery(id+"F3.wireOp",VERTEX,"E18.7.0.7");
            var Q48;
            Q48=sQuery(id+"F3.wireOp",VERTEX,"E18.5.0.7");
            var Q49;
            Q49=sQuery(id+"F3.wireOp",VERTEX,"E18.5.0.38");
            var Q50;
            Q50=sQuery(id+"F3.wireOp",VERTEX,"E18.6.0.14");
            var Q51;
            Q51=sQuery(id+"F3.wireOp",VERTEX,"E18.5.0.5");
            var Q52;
            Q52=sQuery(id+"F3.wireOp",VERTEX,"E18.6.0.34");
            var Q53;
            Q53=sQuery(id+"F3.wireOp",VERTEX,"E18.7.0.10");
            var Q54;
            Q54=sQuery(id+"F3.wireOp",VERTEX,"E18.5.0.10");
            var Q55;
            Q55=sQuery(id+"F3.wireOp",VERTEX,"E18.6.0.38");
            var Q56;
            Q56=sQuery(id+"F3.wireOp",VERTEX,"E18.7.0.14");
            var Q57;
            Q57=sQuery(id+"F3.wireOp",VERTEX,"E18.5.0.14");
            var Q58;
            Q58=sQuery(id+"F3.wireOp",VERTEX,"E18.5.0.36");
            var Q59;
            Q59=sQuery(id+"F3.wireOp",VERTEX,"E18.7.0.18");
            var Q60;
            Q60=makeQuery(id+"F1.opExtrude","SWEPT_BODY",BODY,{"disambiguationData":[OSD([sQuery(id+"F0.wireOp",EDGE,"E0.bottom"),sQuery(id+"F0.wireOp",EDGE,"E0.top"),sQuery(id+"F0.wireOp",EDGE,"E0.left"),sQuery(id+"F0.wireOp",EDGE,"E0.right"),sQuery(id+"F0.wireOp",EDGE,"E1"),sQuery(id+"F0.wireOp",EDGE,"E2"),sQuery(id+"F0.wireOp",EDGE,"E3"),sQuery(id+"F0.wireOp",EDGE,"E4")])]});
            hole(context, id + "F5", {"style" : HoleStyle.SIMPLE, "endStyle" : HoleEndStyle.BLIND, "holeDiameter" : 1 * mm, "majorDiameter" : 5 * mm, "holeDepth" : 3 * mm, "isTappedThrough" : true, "tappedDepth" : 12 * mm, "tapClearance" : 3, "locations" : qUnion([Q0, Q1, Q2, Q3, Q4, Q5, Q6, Q7, Q8, Q9, Q10, Q11, Q12, Q13, Q14, Q15, Q16, Q17, Q18, Q19, Q20, Q21, Q22, Q23, Q24, Q25, Q26, Q27, Q28, Q29, Q30, Q31, Q32, Q33, Q34, Q35, Q36, Q37, Q38, Q39, Q40, Q41, Q42, Q43, Q44, Q45, Q46, Q47, Q48, Q49, Q50, Q51, Q52, Q53, Q54, Q55, Q56, Q57, Q58, Q59]), "scope" : qUnion([Q60])});
        }
        {
            var Q0;
            Q0=sQuery(id+"F3.wireOp",VERTEX,"E18.8.0.13");
            var Q1;
            Q1=sQuery(id+"F3.wireOp",VERTEX,"E18.9.0.34");
            var Q2;
            Q2=sQuery(id+"F3.wireOp",VERTEX,"E18.8.0.15");
            var Q3;
            Q3=sQuery(id+"F3.wireOp",VERTEX,"E18.8.0.40.start");
            var Q4;
            Q4=sQuery(id+"F3.wireOp",VERTEX,"E18.10.0.8");
            var Q5;
            Q5=sQuery(id+"F3.wireOp",VERTEX,"E18.10.0.27");
            var Q6;
            Q6=sQuery(id+"F3.wireOp",VERTEX,"E18.8.0.11");
            var Q7;
            Q7=sQuery(id+"F3.wireOp",VERTEX,"E18.8.0.38");
            var Q8;
            Q8=sQuery(id+"F3.wireOp",VERTEX,"E18.11.0.28");
            var Q9;
            Q9=sQuery(id+"F3.wireOp",VERTEX,"E18.11.0.14");
            var Q10;
            Q10=sQuery(id+"F3.wireOp",VERTEX,"E18.8.0.28");
            var Q11;
            Q11=sQuery(id+"F3.wireOp",VERTEX,"E18.10.0.7");
            var Q12;
            Q12=sQuery(id+"F3.wireOp",VERTEX,"E18.8.0.7");
            var Q13;
            Q13=sQuery(id+"F3.wireOp",VERTEX,"E18.11.0.21");
            var Q14;
            Q14=sQuery(id+"F3.wireOp",VERTEX,"E18.11.0.36");
            var Q15;
            Q15=sQuery(id+"F3.wireOp",VERTEX,"E18.11.0.33");
            var Q16;
            Q16=sQuery(id+"F3.wireOp",VERTEX,"E18.11.0.40.start");
            var Q17;
            Q17=sQuery(id+"F3.wireOp",VERTEX,"E18.10.0.24");
            var Q18;
            Q18=sQuery(id+"F3.wireOp",VERTEX,"E18.8.0.29");
            var Q19;
            Q19=sQuery(id+"F3.wireOp",VERTEX,"E18.9.0.18");
            var Q20;
            Q20=sQuery(id+"F3.wireOp",VERTEX,"E18.10.0.10");
            var Q21;
            Q21=sQuery(id+"F3.wireOp",VERTEX,"E18.8.0.27");
            var Q22;
            Q22=sQuery(id+"F3.wireOp",VERTEX,"E18.10.0.28");
            var Q23;
            Q23=sQuery(id+"F3.wireOp",VERTEX,"E18.10.0.11");
            var Q24;
            Q24=sQuery(id+"F3.wireOp",VERTEX,"E18.10.0.32");
            var Q25;
            Q25=sQuery(id+"F3.wireOp",VERTEX,"E18.9.0.33");
            var Q26;
            Q26=sQuery(id+"F3.wireOp",VERTEX,"E18.9.0.36");
            var Q27;
            Q27=sQuery(id+"F3.wireOp",VERTEX,"E18.9.0.15");
            var Q28;
            Q28=sQuery(id+"F3.wireOp",VERTEX,"E18.10.0.40.start");
            var Q29;
            Q29=sQuery(id+"F3.wireOp",VERTEX,"E18.10.0.34");
            var Q30;
            Q30=sQuery(id+"F3.wireOp",VERTEX,"E18.9.0.40.start");
            var Q31;
            Q31=sQuery(id+"F3.wireOp",VERTEX,"E18.8.0.24");
            var Q32;
            Q32=sQuery(id+"F3.wireOp",VERTEX,"E18.8.0.10");
            var Q33;
            Q33=sQuery(id+"F3.wireOp",VERTEX,"E18.10.0.33");
            var Q34;
            Q34=sQuery(id+"F3.wireOp",VERTEX,"E18.8.0.5");
            var Q35;
            Q35=sQuery(id+"F3.wireOp",VERTEX,"E18.11.0.13");
            var Q36;
            Q36=sQuery(id+"F3.wireOp",VERTEX,"E18.9.0.14");
            var Q37;
            Q37=sQuery(id+"F3.wireOp",VERTEX,"E18.10.0.38");
            var Q38;
            Q38=sQuery(id+"F3.wireOp",VERTEX,"E18.11.0.32");
            var Q39;
            Q39=sQuery(id+"F3.wireOp",VERTEX,"E18.8.0.8");
            var Q40;
            Q40=sQuery(id+"F3.wireOp",VERTEX,"E18.8.0.36");
            var Q41;
            Q41=sQuery(id+"F3.wireOp",VERTEX,"E18.8.0.32");
            var Q42;
            Q42=sQuery(id+"F3.wireOp",VERTEX,"E18.8.0.14");
            var Q43;
            Q43=sQuery(id+"F3.wireOp",VERTEX,"E18.9.0.21");
            var Q44;
            Q44=sQuery(id+"F3.wireOp",VERTEX,"E18.10.0.29");
            var Q45;
            Q45=sQuery(id+"F3.wireOp",VERTEX,"E18.9.0.5");
            var Q46;
            Q46=sQuery(id+"F3.wireOp",VERTEX,"E18.11.0.18");
            var Q47;
            Q47=sQuery(id+"F3.wireOp",VERTEX,"E18.11.0.34");
            var Q48;
            Q48=sQuery(id+"F3.wireOp",VERTEX,"E18.9.0.32");
            var Q49;
            Q49=sQuery(id+"F3.wireOp",VERTEX,"E18.11.0.29");
            var Q50;
            Q50=sQuery(id+"F3.wireOp",VERTEX,"E18.9.0.13");
            var Q51;
            Q51=sQuery(id+"F3.wireOp",VERTEX,"E18.9.0.29");
            var Q52;
            Q52=sQuery(id+"F3.wireOp",VERTEX,"E18.10.0.5");
            var Q53;
            Q53=sQuery(id+"F3.wireOp",VERTEX,"E18.10.0.21");
            var Q54;
            Q54=sQuery(id+"F3.wireOp",VERTEX,"E18.8.0.21");
            var Q55;
            Q55=sQuery(id+"F3.wireOp",VERTEX,"E18.10.0.36");
            var Q56;
            Q56=sQuery(id+"F3.wireOp",VERTEX,"E18.9.0.28");
            var Q57;
            Q57=sQuery(id+"F3.wireOp",VERTEX,"E18.11.0.11");
            var Q58;
            Q58=sQuery(id+"F3.wireOp",VERTEX,"E18.11.0.27");
            var Q59;
            Q59=sQuery(id+"F3.wireOp",VERTEX,"E18.9.0.11");
            var Q60;
            Q60=sQuery(id+"F3.wireOp",VERTEX,"E18.9.0.27");
            var Q61;
            Q61=sQuery(id+"F3.wireOp",VERTEX,"E18.11.0.10");
            var Q62;
            Q62=sQuery(id+"F3.wireOp",VERTEX,"E18.10.0.18");
            var Q63;
            Q63=sQuery(id+"F3.wireOp",VERTEX,"E18.8.0.18");
            var Q64;
            Q64=sQuery(id+"F3.wireOp",VERTEX,"E18.8.0.33");
            var Q65;
            Q65=sQuery(id+"F3.wireOp",VERTEX,"E18.11.0.24");
            var Q66;
            Q66=sQuery(id+"F3.wireOp",VERTEX,"E18.11.0.8");
            var Q67;
            Q67=sQuery(id+"F3.wireOp",VERTEX,"E18.9.0.8");
            var Q68;
            Q68=sQuery(id+"F3.wireOp",VERTEX,"E18.9.0.24");
            var Q69;
            Q69=sQuery(id+"F3.wireOp",VERTEX,"E18.10.0.15");
            var Q70;
            Q70=sQuery(id+"F3.wireOp",VERTEX,"E18.9.0.7");
            var Q71;
            Q71=sQuery(id+"F3.wireOp",VERTEX,"E18.11.0.38");
            var Q72;
            Q72=sQuery(id+"F3.wireOp",VERTEX,"E18.9.0.38");
            var Q73;
            Q73=sQuery(id+"F3.wireOp",VERTEX,"E18.10.0.14");
            var Q74;
            Q74=sQuery(id+"F3.wireOp",VERTEX,"E18.10.0.13");
            var Q75;
            Q75=sQuery(id+"F3.wireOp",VERTEX,"E18.11.0.5");
            var Q76;
            Q76=sQuery(id+"F3.wireOp",VERTEX,"E18.8.0.34");
            var Q77;
            Q77=sQuery(id+"F3.wireOp",VERTEX,"E18.11.0.15");
            var Q78;
            Q78=sQuery(id+"F3.wireOp",VERTEX,"E18.11.0.7");
            var Q79;
            Q79=sQuery(id+"F3.wireOp",VERTEX,"E18.9.0.10");
            var Q80;
            Q80=makeQuery(id+"F1.opExtrude","SWEPT_BODY",BODY,{"disambiguationData":[OSD([sQuery(id+"F0.wireOp",EDGE,"E0.bottom"),sQuery(id+"F0.wireOp",EDGE,"E0.top"),sQuery(id+"F0.wireOp",EDGE,"E0.left"),sQuery(id+"F0.wireOp",EDGE,"E0.right"),sQuery(id+"F0.wireOp",EDGE,"E1"),sQuery(id+"F0.wireOp",EDGE,"E2"),sQuery(id+"F0.wireOp",EDGE,"E3"),sQuery(id+"F0.wireOp",EDGE,"E4")])]});
            hole(context, id + "F6", {"style" : HoleStyle.SIMPLE, "endStyle" : HoleEndStyle.BLIND, "holeDiameter" : 1 * mm, "majorDiameter" : 5 * mm, "holeDepth" : 3 * mm, "isTappedThrough" : true, "tappedDepth" : 12 * mm, "tapClearance" : 3, "locations" : qUnion([Q0, Q1, Q2, Q3, Q4, Q5, Q6, Q7, Q8, Q9, Q10, Q11, Q12, Q13, Q14, Q15, Q16, Q17, Q18, Q19, Q20, Q21, Q22, Q23, Q24, Q25, Q26, Q27, Q28, Q29, Q30, Q31, Q32, Q33, Q34, Q35, Q36, Q37, Q38, Q39, Q40, Q41, Q42, Q43, Q44, Q45, Q46, Q47, Q48, Q49, Q50, Q51, Q52, Q53, Q54, Q55, Q56, Q57, Q58, Q59, Q60, Q61, Q62, Q63, Q64, Q65, Q66, Q67, Q68, Q69, Q70, Q71, Q72, Q73, Q74, Q75, Q76, Q77, Q78, Q79]), "scope" : qUnion([Q80])});
        }
        {
            var Q0;
            Q0=sQuery(id+"F3.wireOp",VERTEX,"E18.13.0.34");
            var Q1;
            Q1=sQuery(id+"F3.wireOp",VERTEX,"E18.13.0.5");
            var Q2;
            Q2=sQuery(id+"F3.wireOp",VERTEX,"E18.14.0.13");
            var Q3;
            Q3=sQuery(id+"F3.wireOp",VERTEX,"E18.13.0.33");
            var Q4;
            Q4=sQuery(id+"F3.wireOp",VERTEX,"E18.14.0.38");
            var Q5;
            Q5=sQuery(id+"F3.wireOp",VERTEX,"E18.12.0.34");
            var Q6;
            Q6=sQuery(id+"F3.wireOp",VERTEX,"E18.14.0.33");
            var Q7;
            Q7=sQuery(id+"F3.wireOp",VERTEX,"E18.13.0.38");
            var Q8;
            Q8=sQuery(id+"F3.wireOp",VERTEX,"E18.13.0.11");
            var Q9;
            Q9=sQuery(id+"F3.wireOp",VERTEX,"E18.15.0.29");
            var Q10;
            Q10=sQuery(id+"F3.wireOp",VERTEX,"E18.12.0.27");
            var Q11;
            Q11=sQuery(id+"F3.wireOp",VERTEX,"E18.13.0.27");
            var Q12;
            Q12=sQuery(id+"F3.wireOp",VERTEX,"E18.15.0.33");
            var Q13;
            Q13=sQuery(id+"F3.wireOp",VERTEX,"E18.12.0.38");
            var Q14;
            Q14=sQuery(id+"F3.wireOp",VERTEX,"E18.15.0.15");
            var Q15;
            Q15=sQuery(id+"F3.wireOp",VERTEX,"E18.14.0.24");
            var Q16;
            Q16=sQuery(id+"F3.wireOp",VERTEX,"E18.15.0.36");
            var Q17;
            Q17=sQuery(id+"F3.wireOp",VERTEX,"E18.14.0.11");
            var Q18;
            Q18=sQuery(id+"F3.wireOp",VERTEX,"E18.14.0.29");
            var Q19;
            Q19=sQuery(id+"F3.wireOp",VERTEX,"E18.12.0.32");
            var Q20;
            Q20=sQuery(id+"F3.wireOp",VERTEX,"E18.14.0.32");
            var Q21;
            Q21=sQuery(id+"F3.wireOp",VERTEX,"E18.14.0.10");
            var Q22;
            Q22=sQuery(id+"F3.wireOp",VERTEX,"E18.15.0.27");
            var Q23;
            Q23=sQuery(id+"F3.wireOp",VERTEX,"E18.13.0.18");
            var Q24;
            Q24=sQuery(id+"F3.wireOp",VERTEX,"E18.13.0.21");
            var Q25;
            Q25=sQuery(id+"F3.wireOp",VERTEX,"E18.14.0.34");
            var Q26;
            Q26=sQuery(id+"F3.wireOp",VERTEX,"E18.12.0.5");
            var Q27;
            Q27=sQuery(id+"F3.wireOp",VERTEX,"E18.15.0.28");
            var Q28;
            Q28=sQuery(id+"F3.wireOp",VERTEX,"E18.14.0.5");
            var Q29;
            Q29=sQuery(id+"F3.wireOp",VERTEX,"E18.14.0.21");
            var Q30;
            Q30=sQuery(id+"F3.wireOp",VERTEX,"E18.13.0.32");
            var Q31;
            Q31=sQuery(id+"F3.wireOp",VERTEX,"E18.14.0.28");
            var Q32;
            Q32=sQuery(id+"F3.wireOp",VERTEX,"E18.15.0.5");
            var Q33;
            Q33=sQuery(id+"F3.wireOp",VERTEX,"E18.12.0.15");
            var Q34;
            Q34=sQuery(id+"F3.wireOp",VERTEX,"E18.15.0.7");
            var Q35;
            Q35=sQuery(id+"F3.wireOp",VERTEX,"E18.15.0.24");
            var Q36;
            Q36=sQuery(id+"F3.wireOp",VERTEX,"E18.13.0.8");
            var Q37;
            Q37=sQuery(id+"F3.wireOp",VERTEX,"E18.12.0.11");
            var Q38;
            Q38=sQuery(id+"F3.wireOp",VERTEX,"E18.12.0.28");
            var Q39;
            Q39=sQuery(id+"F3.wireOp",VERTEX,"E18.14.0.14");
            var Q40;
            Q40=sQuery(id+"F3.wireOp",VERTEX,"E18.15.0.38");
            var Q41;
            Q41=sQuery(id+"F3.wireOp",VERTEX,"E18.12.0.18");
            var Q42;
            Q42=sQuery(id+"F3.wireOp",VERTEX,"E18.13.0.29");
            var Q43;
            Q43=sQuery(id+"F3.wireOp",VERTEX,"E18.13.0.14");
            var Q44;
            Q44=sQuery(id+"F3.wireOp",VERTEX,"E18.14.0.8");
            var Q45;
            Q45=sQuery(id+"F3.wireOp",VERTEX,"E18.15.0.32");
            var Q46;
            Q46=sQuery(id+"F3.wireOp",VERTEX,"E18.13.0.36");
            var Q47;
            Q47=sQuery(id+"F3.wireOp",VERTEX,"E18.15.0.34");
            var Q48;
            Q48=sQuery(id+"F3.wireOp",VERTEX,"E18.15.0.18");
            var Q49;
            Q49=sQuery(id+"F3.wireOp",VERTEX,"E18.12.0.10");
            var Q50;
            Q50=sQuery(id+"F3.wireOp",VERTEX,"E18.12.0.24");
            var Q51;
            Q51=sQuery(id+"F3.wireOp",VERTEX,"E18.12.0.8");
            var Q52;
            Q52=sQuery(id+"F3.wireOp",VERTEX,"E18.14.0.27");
            var Q53;
            Q53=sQuery(id+"F3.wireOp",VERTEX,"E18.15.0.40.start");
            var Q54;
            Q54=sQuery(id+"F3.wireOp",VERTEX,"E18.14.0.36");
            var Q55;
            Q55=sQuery(id+"F3.wireOp",VERTEX,"E18.12.0.36");
            var Q56;
            Q56=sQuery(id+"F3.wireOp",VERTEX,"E18.13.0.28");
            var Q57;
            Q57=sQuery(id+"F3.wireOp",VERTEX,"E18.15.0.11");
            var Q58;
            Q58=sQuery(id+"F3.wireOp",VERTEX,"E18.14.0.18");
            var Q59;
            Q59=sQuery(id+"F3.wireOp",VERTEX,"E18.15.0.10");
            var Q60;
            Q60=sQuery(id+"F3.wireOp",VERTEX,"E18.13.0.10");
            var Q61;
            Q61=sQuery(id+"F3.wireOp",VERTEX,"E18.14.0.40.start");
            var Q62;
            Q62=sQuery(id+"F3.wireOp",VERTEX,"E18.12.0.33");
            var Q63;
            Q63=sQuery(id+"F3.wireOp",VERTEX,"E18.15.0.8");
            var Q64;
            Q64=sQuery(id+"F3.wireOp",VERTEX,"E18.13.0.24");
            var Q65;
            Q65=sQuery(id+"F3.wireOp",VERTEX,"E18.13.0.40.start");
            var Q66;
            Q66=sQuery(id+"F3.wireOp",VERTEX,"E18.13.0.7");
            var Q67;
            Q67=sQuery(id+"F3.wireOp",VERTEX,"E18.14.0.15");
            var Q68;
            Q68=sQuery(id+"F3.wireOp",VERTEX,"E18.12.0.14");
            var Q69;
            Q69=sQuery(id+"F3.wireOp",VERTEX,"E18.12.0.40.start");
            var Q70;
            Q70=sQuery(id+"F3.wireOp",VERTEX,"E18.12.0.13");
            var Q71;
            Q71=sQuery(id+"F3.wireOp",VERTEX,"E18.12.0.29");
            var Q72;
            Q72=sQuery(id+"F3.wireOp",VERTEX,"E18.15.0.21");
            var Q73;
            Q73=sQuery(id+"F3.wireOp",VERTEX,"E18.12.0.21");
            var Q74;
            Q74=sQuery(id+"F3.wireOp",VERTEX,"E18.15.0.13");
            var Q75;
            Q75=sQuery(id+"F3.wireOp",VERTEX,"E18.13.0.13");
            var Q76;
            Q76=sQuery(id+"F3.wireOp",VERTEX,"E18.13.0.15");
            var Q77;
            Q77=sQuery(id+"F3.wireOp",VERTEX,"E18.14.0.7");
            var Q78;
            Q78=sQuery(id+"F3.wireOp",VERTEX,"E18.12.0.7");
            var Q79;
            Q79=sQuery(id+"F3.wireOp",VERTEX,"E18.15.0.14");
            var Q80;
            Q80=makeQuery(id+"F1.opExtrude","SWEPT_BODY",BODY,{"disambiguationData":[OSD([sQuery(id+"F0.wireOp",EDGE,"E0.bottom"),sQuery(id+"F0.wireOp",EDGE,"E0.top"),sQuery(id+"F0.wireOp",EDGE,"E0.left"),sQuery(id+"F0.wireOp",EDGE,"E0.right"),sQuery(id+"F0.wireOp",EDGE,"E1"),sQuery(id+"F0.wireOp",EDGE,"E2"),sQuery(id+"F0.wireOp",EDGE,"E3"),sQuery(id+"F0.wireOp",EDGE,"E4")])]});
            hole(context, id + "F7", {"style" : HoleStyle.SIMPLE, "endStyle" : HoleEndStyle.BLIND, "holeDiameter" : 1 * mm, "majorDiameter" : 5 * mm, "holeDepth" : 3 * mm, "isTappedThrough" : true, "tappedDepth" : 12 * mm, "tapClearance" : 3, "locations" : qUnion([Q0, Q1, Q2, Q3, Q4, Q5, Q6, Q7, Q8, Q9, Q10, Q11, Q12, Q13, Q14, Q15, Q16, Q17, Q18, Q19, Q20, Q21, Q22, Q23, Q24, Q25, Q26, Q27, Q28, Q29, Q30, Q31, Q32, Q33, Q34, Q35, Q36, Q37, Q38, Q39, Q40, Q41, Q42, Q43, Q44, Q45, Q46, Q47, Q48, Q49, Q50, Q51, Q52, Q53, Q54, Q55, Q56, Q57, Q58, Q59, Q60, Q61, Q62, Q63, Q64, Q65, Q66, Q67, Q68, Q69, Q70, Q71, Q72, Q73, Q74, Q75, Q76, Q77, Q78, Q79]), "scope" : qUnion([Q80])});
        }
        {
            var Q0;
            Q0=sQuery(id+"F3.wireOp",VERTEX,"E18.16.0.38");
            var Q1;
            Q1=sQuery(id+"F3.wireOp",VERTEX,"E18.19.0.13");
            var Q2;
            Q2=sQuery(id+"F3.wireOp",VERTEX,"E18.19.0.8");
            var Q3;
            Q3=sQuery(id+"F3.wireOp",VERTEX,"E18.17.0.18");
            var Q4;
            Q4=sQuery(id+"F3.wireOp",VERTEX,"E18.19.0.32");
            var Q5;
            Q5=sQuery(id+"F3.wireOp",VERTEX,"E18.17.0.14");
            var Q6;
            Q6=sQuery(id+"F3.wireOp",VERTEX,"E18.16.0.40.start");
            var Q7;
            Q7=sQuery(id+"F3.wireOp",VERTEX,"E18.16.0.24");
            var Q8;
            Q8=sQuery(id+"F3.wireOp",VERTEX,"E18.18.0.24");
            var Q9;
            Q9=sQuery(id+"F3.wireOp",VERTEX,"E18.16.0.8");
            var Q10;
            Q10=sQuery(id+"F3.wireOp",VERTEX,"E18.18.0.40.start");
            var Q11;
            Q11=sQuery(id+"F3.wireOp",VERTEX,"E18.16.0.33");
            var Q12;
            Q12=sQuery(id+"F3.wireOp",VERTEX,"E18.18.0.33");
            var Q13;
            Q13=sQuery(id+"F3.wireOp",VERTEX,"E18.19.0.21");
            var Q14;
            Q14=sQuery(id+"F3.wireOp",VERTEX,"E18.18.0.14");
            var Q15;
            Q15=sQuery(id+"F3.wireOp",VERTEX,"E18.18.0.11");
            var Q16;
            Q16=sQuery(id+"F3.wireOp",VERTEX,"E18.17.0.5");
            var Q17;
            Q17=sQuery(id+"F3.wireOp",VERTEX,"E18.18.0.28");
            var Q18;
            Q18=sQuery(id+"F3.wireOp",VERTEX,"E18.18.0.32");
            var Q19;
            Q19=sQuery(id+"F3.wireOp",VERTEX,"E18.17.0.7");
            var Q20;
            Q20=sQuery(id+"F3.wireOp",VERTEX,"E18.19.0.33");
            var Q21;
            Q21=sQuery(id+"F3.wireOp",VERTEX,"E18.18.0.7");
            var Q22;
            Q22=sQuery(id+"F3.wireOp",VERTEX,"E18.19.0.28");
            var Q23;
            Q23=sQuery(id+"F3.wireOp",VERTEX,"E18.19.0.29");
            var Q24;
            Q24=sQuery(id+"F3.wireOp",VERTEX,"E18.16.0.14");
            var Q25;
            Q25=sQuery(id+"F3.wireOp",VERTEX,"E18.17.0.8");
            var Q26;
            Q26=sQuery(id+"F3.wireOp",VERTEX,"E18.16.0.11");
            var Q27;
            Q27=sQuery(id+"F3.wireOp",VERTEX,"E18.16.0.28");
            var Q28;
            Q28=sQuery(id+"F3.wireOp",VERTEX,"E18.16.0.13");
            var Q29;
            Q29=sQuery(id+"F3.wireOp",VERTEX,"E18.17.0.36");
            var Q30;
            Q30=sQuery(id+"F3.wireOp",VERTEX,"E18.19.0.15");
            var Q31;
            Q31=sQuery(id+"F3.wireOp",VERTEX,"E18.16.0.36");
            var Q32;
            Q32=sQuery(id+"F3.wireOp",VERTEX,"E18.18.0.27");
            var Q33;
            Q33=sQuery(id+"F3.wireOp",VERTEX,"E18.18.0.29");
            var Q34;
            Q34=sQuery(id+"F3.wireOp",VERTEX,"E18.17.0.28");
            var Q35;
            Q35=sQuery(id+"F3.wireOp",VERTEX,"E18.18.0.13");
            var Q36;
            Q36=sQuery(id+"F3.wireOp",VERTEX,"E18.17.0.32");
            var Q37;
            Q37=sQuery(id+"F3.wireOp",VERTEX,"E18.18.0.10");
            var Q38;
            Q38=sQuery(id+"F3.wireOp",VERTEX,"E18.19.0.34");
            var Q39;
            Q39=sQuery(id+"F3.wireOp",VERTEX,"E18.19.0.40.start");
            var Q40;
            Q40=sQuery(id+"F3.wireOp",VERTEX,"E18.16.0.29");
            var Q41;
            Q41=sQuery(id+"F3.wireOp",VERTEX,"E18.19.0.5");
            var Q42;
            Q42=sQuery(id+"F3.wireOp",VERTEX,"E18.17.0.21");
            var Q43;
            Q43=sQuery(id+"F3.wireOp",VERTEX,"E18.19.0.38");
            var Q44;
            Q44=sQuery(id+"F3.wireOp",VERTEX,"E18.16.0.15");
            var Q45;
            Q45=sQuery(id+"F3.wireOp",VERTEX,"E18.16.0.32");
            var Q46;
            Q46=sQuery(id+"F3.wireOp",VERTEX,"E18.17.0.24");
            var Q47;
            Q47=sQuery(id+"F3.wireOp",VERTEX,"E18.19.0.10");
            var Q48;
            Q48=sQuery(id+"F3.wireOp",VERTEX,"E18.17.0.10");
            var Q49;
            Q49=sQuery(id+"F3.wireOp",VERTEX,"E18.18.0.18");
            var Q50;
            Q50=sQuery(id+"F3.wireOp",VERTEX,"E18.17.0.11");
            var Q51;
            Q51=sQuery(id+"F3.wireOp",VERTEX,"E18.16.0.7");
            var Q52;
            Q52=sQuery(id+"F3.wireOp",VERTEX,"E18.17.0.40.start");
            var Q53;
            Q53=sQuery(id+"F3.wireOp",VERTEX,"E18.16.0.21");
            var Q54;
            Q54=sQuery(id+"F3.wireOp",VERTEX,"E18.18.0.5");
            var Q55;
            Q55=sQuery(id+"F3.wireOp",VERTEX,"E18.18.0.21");
            var Q56;
            Q56=sQuery(id+"F3.wireOp",VERTEX,"E18.17.0.13");
            var Q57;
            Q57=sQuery(id+"F3.wireOp",VERTEX,"E18.17.0.29");
            var Q58;
            Q58=sQuery(id+"F3.wireOp",VERTEX,"E18.19.0.36");
            var Q59;
            Q59=sQuery(id+"F3.wireOp",VERTEX,"E18.16.0.10");
            var Q60;
            Q60=sQuery(id+"F3.wireOp",VERTEX,"E18.17.0.34");
            var Q61;
            Q61=sQuery(id+"F3.wireOp",VERTEX,"E18.19.0.18");
            var Q62;
            Q62=sQuery(id+"F3.wireOp",VERTEX,"E18.17.0.33");
            var Q63;
            Q63=sQuery(id+"F3.wireOp",VERTEX,"E18.18.0.8");
            var Q64;
            Q64=sQuery(id+"F3.wireOp",VERTEX,"E18.16.0.5");
            var Q65;
            Q65=sQuery(id+"F3.wireOp",VERTEX,"E18.16.0.27");
            var Q66;
            Q66=sQuery(id+"F3.wireOp",VERTEX,"E18.18.0.36");
            var Q67;
            Q67=sQuery(id+"F3.wireOp",VERTEX,"E18.19.0.11");
            var Q68;
            Q68=sQuery(id+"F3.wireOp",VERTEX,"E18.17.0.27");
            var Q69;
            Q69=sQuery(id+"F3.wireOp",VERTEX,"E18.19.0.27");
            var Q70;
            Q70=sQuery(id+"F3.wireOp",VERTEX,"E18.18.0.34");
            var Q71;
            Q71=sQuery(id+"F3.wireOp",VERTEX,"E18.16.0.34");
            var Q72;
            Q72=sQuery(id+"F3.wireOp",VERTEX,"E18.19.0.24");
            var Q73;
            Q73=sQuery(id+"F3.wireOp",VERTEX,"E18.18.0.15");
            var Q74;
            Q74=sQuery(id+"F3.wireOp",VERTEX,"E18.19.0.7");
            var Q75;
            Q75=sQuery(id+"F3.wireOp",VERTEX,"E18.17.0.38");
            var Q76;
            Q76=sQuery(id+"F3.wireOp",VERTEX,"E18.16.0.18");
            var Q77;
            Q77=sQuery(id+"F3.wireOp",VERTEX,"E18.18.0.38");
            var Q78;
            Q78=sQuery(id+"F3.wireOp",VERTEX,"E18.19.0.14");
            var Q79;
            Q79=sQuery(id+"F3.wireOp",VERTEX,"E18.17.0.15");
            var Q80;
            Q80=makeQuery(id+"F1.opExtrude","SWEPT_BODY",BODY,{"disambiguationData":[OSD([sQuery(id+"F0.wireOp",EDGE,"E0.bottom"),sQuery(id+"F0.wireOp",EDGE,"E0.top"),sQuery(id+"F0.wireOp",EDGE,"E0.left"),sQuery(id+"F0.wireOp",EDGE,"E0.right"),sQuery(id+"F0.wireOp",EDGE,"E1"),sQuery(id+"F0.wireOp",EDGE,"E2"),sQuery(id+"F0.wireOp",EDGE,"E3"),sQuery(id+"F0.wireOp",EDGE,"E4")])]});
            hole(context, id + "F8", {"style" : HoleStyle.SIMPLE, "endStyle" : HoleEndStyle.BLIND, "holeDiameter" : 1 * mm, "majorDiameter" : 5 * mm, "holeDepth" : 3 * mm, "isTappedThrough" : true, "tappedDepth" : 12 * mm, "tapClearance" : 3, "locations" : qUnion([Q0, Q1, Q2, Q3, Q4, Q5, Q6, Q7, Q8, Q9, Q10, Q11, Q12, Q13, Q14, Q15, Q16, Q17, Q18, Q19, Q20, Q21, Q22, Q23, Q24, Q25, Q26, Q27, Q28, Q29, Q30, Q31, Q32, Q33, Q34, Q35, Q36, Q37, Q38, Q39, Q40, Q41, Q42, Q43, Q44, Q45, Q46, Q47, Q48, Q49, Q50, Q51, Q52, Q53, Q54, Q55, Q56, Q57, Q58, Q59, Q60, Q61, Q62, Q63, Q64, Q65, Q66, Q67, Q68, Q69, Q70, Q71, Q72, Q73, Q74, Q75, Q76, Q77, Q78, Q79]), "scope" : qUnion([Q80])});
        }
        {
            var Q0;
            Q0=sQuery(id+"F3.wireOp",VERTEX,"E18.3.0.30");
            var Q1;
            Q1=sQuery(id+"F3.wireOp",VERTEX,"E18.4.0.6");
            var Q2;
            Q2=sQuery(id+"F3.wireOp",VERTEX,"E18.4.0.22");
            var Q3;
            Q3=sQuery(id+"F3.wireOp",VERTEX,"E18.2.0.6");
            var Q4;
            Q4=sQuery(id+"F3.wireOp",VERTEX,"E18.2.0.22");
            var Q5;
            Q5=sQuery(id+"F3.wireOp",VERTEX,"E17.0.22.0");
            var Q6;
            Q6=sQuery(id+"F3.wireOp",VERTEX,"E17.0.38.0");
            var Q7;
            Q7=sQuery(id+"F3.wireOp",VERTEX,"E18.1.0.30");
            var Q8;
            Q8=sQuery(id+"F3.wireOp",VERTEX,"E18.4.0.37");
            var Q9;
            Q9=sQuery(id+"F3.wireOp",VERTEX,"E18.2.0.37");
            var Q10;
            Q10=sQuery(id+"F3.wireOp",VERTEX,"E17.0.21.0");
            var Q11;
            Q11=sQuery(id+"F3.wireOp",VERTEX,"E17.0.37.0");
            var Q12;
            Q12=sQuery(id+"F3.wireOp",VERTEX,"E18.4.0.4");
            var Q13;
            Q13=sQuery(id+"F3.wireOp",VERTEX,"E18.4.0.20");
            var Q14;
            Q14=sQuery(id+"F3.wireOp",VERTEX,"E18.2.0.4");
            var Q15;
            Q15=sQuery(id+"F3.wireOp",VERTEX,"E18.2.0.20");
            var Q16;
            Q16=sQuery(id+"F3.wireOp",VERTEX,"E17.0.20.0");
            var Q17;
            Q17=sQuery(id+"F3.wireOp",VERTEX,"E17.0.36.0");
            var Q18;
            Q18=sQuery(id+"F3.wireOp",VERTEX,"E18.2.0.3");
            var Q19;
            Q19=sQuery(id+"F3.wireOp",VERTEX,"E18.2.0.19");
            var Q20;
            Q20=sQuery(id+"F3.wireOp",VERTEX,"E18.2.0.35");
            var Q21;
            Q21=sQuery(id+"F3.wireOp",VERTEX,"E17.0.35.0");
            var Q22;
            Q22=sQuery(id+"F3.wireOp",VERTEX,"E18.4.0.3");
            var Q23;
            Q23=sQuery(id+"F3.wireOp",VERTEX,"E18.4.0.19");
            var Q24;
            Q24=sQuery(id+"F3.wireOp",VERTEX,"E18.4.0.35");
            var Q25;
            Q25=sQuery(id+"F3.wireOp",VERTEX,"E17.0.34.0");
            var Q26;
            Q26=sQuery(id+"F3.wireOp",VERTEX,"E18.1.0.26");
            var Q27;
            Q27=sQuery(id+"F3.wireOp",VERTEX,"E18.3.0.26");
            var Q28;
            Q28=sQuery(id+"F3.wireOp",VERTEX,"E18.4.0.2");
            var Q29;
            Q29=sQuery(id+"F3.wireOp",VERTEX,"E18.2.0.2");
            var Q30;
            Q30=sQuery(id+"F3.wireOp",VERTEX,"E18.3.0.25");
            var Q31;
            Q31=sQuery(id+"F3.wireOp",VERTEX,"E18.4.0.1");
            var Q32;
            Q32=sQuery(id+"F3.wireOp",VERTEX,"E18.4.0.17");
            var Q33;
            Q33=sQuery(id+"F3.wireOp",VERTEX,"E18.2.0.1");
            var Q34;
            Q34=sQuery(id+"F3.wireOp",VERTEX,"E18.2.0.17");
            var Q35;
            Q35=sQuery(id+"F3.wireOp",VERTEX,"E18.3.0.9");
            var Q36;
            Q36=sQuery(id+"F3.wireOp",VERTEX,"E17.0.33.0");
            var Q37;
            Q37=sQuery(id+"F3.wireOp",VERTEX,"E18.1.0.9");
            var Q38;
            Q38=sQuery(id+"F3.wireOp",VERTEX,"E18.1.0.25");
            var Q39;
            Q39=sQuery(id+"F3.wireOp",VERTEX,"E18.4.0.16");
            var Q40;
            Q40=sQuery(id+"F3.wireOp",VERTEX,"E18.4.0.0");
            var Q41;
            Q41=sQuery(id+"F3.wireOp",VERTEX,"E18.2.0.0");
            var Q42;
            Q42=sQuery(id+"F3.wireOp",VERTEX,"E18.2.0.16");
            var Q43;
            Q43=sQuery(id+"F3.wireOp",VERTEX,"E17.0.32.0");
            var Q44;
            Q44=sQuery(id+"F3.wireOp",VERTEX,"E18.4.0.31");
            var Q45;
            Q45=sQuery(id+"F3.wireOp",VERTEX,"E18.2.0.31");
            var Q46;
            Q46=sQuery(id+"F3.wireOp",VERTEX,"E18.3.0.23");
            var Q47;
            Q47=sQuery(id+"F3.wireOp",VERTEX,"E18.3.0.39");
            var Q48;
            Q48=sQuery(id+"F3.wireOp",VERTEX,"E18.1.0.23");
            var Q49;
            Q49=sQuery(id+"F3.wireOp",VERTEX,"E18.1.0.39");
            var Q50;
            Q50=sQuery(id+"F3.wireOp",VERTEX,"E17.0.31.0");
            var Q51;
            Q51=sQuery(id+"F3.wireOp",VERTEX,"E18.4.0.30");
            var Q52;
            Q52=sQuery(id+"F3.wireOp",VERTEX,"E18.2.0.30");
            var Q53;
            Q53=sQuery(id+"F3.wireOp",VERTEX,"E18.3.0.6");
            var Q54;
            Q54=sQuery(id+"F3.wireOp",VERTEX,"E18.3.0.22");
            var Q55;
            Q55=sQuery(id+"F3.wireOp",VERTEX,"E18.1.0.6");
            var Q56;
            Q56=sQuery(id+"F3.wireOp",VERTEX,"E18.1.0.22");
            var Q57;
            Q57=sQuery(id+"F3.wireOp",VERTEX,"E17.0.30.0");
            var Q58;
            Q58=sQuery(id+"F3.wireOp",VERTEX,"E18.3.0.37");
            var Q59;
            Q59=sQuery(id+"F3.wireOp",VERTEX,"E18.1.0.37");
            var Q60;
            Q60=sQuery(id+"F3.wireOp",VERTEX,"E17.0.29.0");
            var Q61;
            Q61=sQuery(id+"F3.wireOp",VERTEX,"E18.3.0.4");
            var Q62;
            Q62=sQuery(id+"F3.wireOp",VERTEX,"E18.3.0.20");
            var Q63;
            Q63=sQuery(id+"F3.wireOp",VERTEX,"E18.1.0.4");
            var Q64;
            Q64=sQuery(id+"F3.wireOp",VERTEX,"E18.1.0.20");
            var Q65;
            Q65=sQuery(id+"F3.wireOp",VERTEX,"E17.0.28.0");
            var Q66;
            Q66=sQuery(id+"F3.wireOp",VERTEX,"E18.3.0.3");
            var Q67;
            Q67=sQuery(id+"F3.wireOp",VERTEX,"E18.3.0.19");
            var Q68;
            Q68=sQuery(id+"F3.wireOp",VERTEX,"E18.3.0.35");
            var Q69;
            Q69=sQuery(id+"F3.wireOp",VERTEX,"E18.1.0.3");
            var Q70;
            Q70=sQuery(id+"F3.wireOp",VERTEX,"E18.1.0.19");
            var Q71;
            Q71=sQuery(id+"F3.wireOp",VERTEX,"E18.1.0.35");
            var Q72;
            Q72=sQuery(id+"F3.wireOp",VERTEX,"E17.0.27.0");
            var Q73;
            Q73=sQuery(id+"F3.wireOp",VERTEX,"E18.4.0.26");
            var Q74;
            Q74=sQuery(id+"F3.wireOp",VERTEX,"E18.2.0.26");
            var Q75;
            Q75=sQuery(id+"F3.wireOp",VERTEX,"E18.3.0.2");
            var Q76;
            Q76=sQuery(id+"F3.wireOp",VERTEX,"E18.1.0.2");
            var Q77;
            Q77=sQuery(id+"F3.wireOp",VERTEX,"E17.0.26.0");
            var Q78;
            Q78=sQuery(id+"F3.wireOp",VERTEX,"E18.4.0.9");
            var Q79;
            Q79=sQuery(id+"F3.wireOp",VERTEX,"E18.4.0.25");
            var Q80;
            Q80=sQuery(id+"F3.wireOp",VERTEX,"E18.2.0.25");
            var Q81;
            Q81=sQuery(id+"F3.wireOp",VERTEX,"E18.3.0.1");
            var Q82;
            Q82=sQuery(id+"F3.wireOp",VERTEX,"E18.3.0.17");
            var Q83;
            Q83=sQuery(id+"F3.wireOp",VERTEX,"E18.1.0.1");
            var Q84;
            Q84=sQuery(id+"F3.wireOp",VERTEX,"E18.1.0.17");
            var Q85;
            Q85=sQuery(id+"F3.wireOp",VERTEX,"E18.2.0.9");
            var Q86;
            Q86=sQuery(id+"F3.wireOp",VERTEX,"E17.0.25.0");
            var Q87;
            Q87=sQuery(id+"F3.wireOp",VERTEX,"E18.3.0.0");
            var Q88;
            Q88=sQuery(id+"F3.wireOp",VERTEX,"E18.3.0.16");
            var Q89;
            Q89=sQuery(id+"F3.wireOp",VERTEX,"E18.1.0.0");
            var Q90;
            Q90=sQuery(id+"F3.wireOp",VERTEX,"E18.1.0.16");
            var Q91;
            Q91=sQuery(id+"F3.wireOp",VERTEX,"E17.0.24.0");
            var Q92;
            Q92=sQuery(id+"F3.wireOp",VERTEX,"E18.4.0.23");
            var Q93;
            Q93=sQuery(id+"F3.wireOp",VERTEX,"E18.4.0.39");
            var Q94;
            Q94=sQuery(id+"F3.wireOp",VERTEX,"E18.2.0.23");
            var Q95;
            Q95=sQuery(id+"F3.wireOp",VERTEX,"E18.2.0.39");
            var Q96;
            Q96=sQuery(id+"F3.wireOp",VERTEX,"E18.3.0.31");
            var Q97;
            Q97=sQuery(id+"F3.wireOp",VERTEX,"E17.0.39.0");
            var Q98;
            Q98=sQuery(id+"F3.wireOp",VERTEX,"E18.1.0.31");
            var Q99;
            Q99=sQuery(id+"F3.wireOp",VERTEX,"E17.0.23.0");
            var Q100;
            Q100=makeQuery(id+"F1.opExtrude","SWEPT_BODY",BODY,{"disambiguationData":[OSD([sQuery(id+"F0.wireOp",EDGE,"E0.bottom"),sQuery(id+"F0.wireOp",EDGE,"E0.top"),sQuery(id+"F0.wireOp",EDGE,"E0.left"),sQuery(id+"F0.wireOp",EDGE,"E0.right"),sQuery(id+"F0.wireOp",EDGE,"E1"),sQuery(id+"F0.wireOp",EDGE,"E2"),sQuery(id+"F0.wireOp",EDGE,"E3"),sQuery(id+"F0.wireOp",EDGE,"E4")])]});
            hole(context, id + "F9", {"style" : HoleStyle.SIMPLE, "endStyle" : HoleEndStyle.BLIND, "holeDiameter" : 1 * mm, "majorDiameter" : 5 * mm, "holeDepth" : 3 * mm, "isTappedThrough" : true, "tappedDepth" : 12 * mm, "tapClearance" : 3, "locations" : qUnion([Q0, Q1, Q2, Q3, Q4, Q5, Q6, Q7, Q8, Q9, Q10, Q11, Q12, Q13, Q14, Q15, Q16, Q17, Q18, Q19, Q20, Q21, Q22, Q23, Q24, Q25, Q26, Q27, Q28, Q29, Q30, Q31, Q32, Q33, Q34, Q35, Q36, Q37, Q38, Q39, Q40, Q41, Q42, Q43, Q44, Q45, Q46, Q47, Q48, Q49, Q50, Q51, Q52, Q53, Q54, Q55, Q56, Q57, Q58, Q59, Q60, Q61, Q62, Q63, Q64, Q65, Q66, Q67, Q68, Q69, Q70, Q71, Q72, Q73, Q74, Q75, Q76, Q77, Q78, Q79, Q80, Q81, Q82, Q83, Q84, Q85, Q86, Q87, Q88, Q89, Q90, Q91, Q92, Q93, Q94, Q95, Q96, Q97, Q98, Q99]), "scope" : qUnion([Q100])});
        }
        {
            var Q0;
            Q0=sQuery(id+"F3.wireOp",VERTEX,"E18.7.0.30");
            var Q1;
            Q1=sQuery(id+"F3.wireOp",VERTEX,"E18.8.0.6");
            var Q2;
            Q2=sQuery(id+"F3.wireOp",VERTEX,"E18.5.0.30");
            var Q3;
            Q3=sQuery(id+"F3.wireOp",VERTEX,"E18.6.0.6");
            var Q4;
            Q4=sQuery(id+"F3.wireOp",VERTEX,"E18.6.0.22");
            var Q5;
            Q5=sQuery(id+"F3.wireOp",VERTEX,"E18.9.0.30");
            var Q6;
            Q6=sQuery(id+"F3.wireOp",VERTEX,"E18.8.0.22");
            var Q7;
            Q7=sQuery(id+"F3.wireOp",VERTEX,"E18.8.0.37");
            var Q8;
            Q8=sQuery(id+"F3.wireOp",VERTEX,"E18.6.0.37");
            var Q9;
            Q9=sQuery(id+"F3.wireOp",VERTEX,"E18.8.0.20");
            var Q10;
            Q10=sQuery(id+"F3.wireOp",VERTEX,"E18.8.0.4");
            var Q11;
            Q11=sQuery(id+"F3.wireOp",VERTEX,"E18.6.0.4");
            var Q12;
            Q12=sQuery(id+"F3.wireOp",VERTEX,"E18.6.0.20");
            var Q13;
            Q13=sQuery(id+"F3.wireOp",VERTEX,"E18.8.0.19");
            var Q14;
            Q14=sQuery(id+"F3.wireOp",VERTEX,"E18.8.0.35");
            var Q15;
            Q15=sQuery(id+"F3.wireOp",VERTEX,"E18.6.0.35");
            var Q16;
            Q16=sQuery(id+"F3.wireOp",VERTEX,"E18.8.0.3");
            var Q17;
            Q17=sQuery(id+"F3.wireOp",VERTEX,"E18.6.0.3");
            var Q18;
            Q18=sQuery(id+"F3.wireOp",VERTEX,"E18.6.0.19");
            var Q19;
            Q19=sQuery(id+"F3.wireOp",VERTEX,"E18.9.0.26");
            var Q20;
            Q20=sQuery(id+"F3.wireOp",VERTEX,"E18.7.0.26");
            var Q21;
            Q21=sQuery(id+"F3.wireOp",VERTEX,"E18.8.0.2");
            var Q22;
            Q22=sQuery(id+"F3.wireOp",VERTEX,"E18.5.0.26");
            var Q23;
            Q23=sQuery(id+"F3.wireOp",VERTEX,"E18.6.0.2");
            var Q24;
            Q24=sQuery(id+"F3.wireOp",VERTEX,"E18.9.0.9");
            var Q25;
            Q25=sQuery(id+"F3.wireOp",VERTEX,"E18.9.0.25");
            var Q26;
            Q26=sQuery(id+"F3.wireOp",VERTEX,"E18.8.0.17");
            var Q27;
            Q27=sQuery(id+"F3.wireOp",VERTEX,"E18.7.0.9");
            var Q28;
            Q28=sQuery(id+"F3.wireOp",VERTEX,"E18.7.0.25");
            var Q29;
            Q29=sQuery(id+"F3.wireOp",VERTEX,"E18.8.0.1");
            var Q30;
            Q30=sQuery(id+"F3.wireOp",VERTEX,"E18.5.0.9");
            var Q31;
            Q31=sQuery(id+"F3.wireOp",VERTEX,"E18.5.0.25");
            var Q32;
            Q32=sQuery(id+"F3.wireOp",VERTEX,"E18.6.0.1");
            var Q33;
            Q33=sQuery(id+"F3.wireOp",VERTEX,"E18.6.0.17");
            var Q34;
            Q34=sQuery(id+"F3.wireOp",VERTEX,"E18.8.0.0");
            var Q35;
            Q35=sQuery(id+"F3.wireOp",VERTEX,"E18.8.0.16");
            var Q36;
            Q36=sQuery(id+"F3.wireOp",VERTEX,"E18.6.0.0");
            var Q37;
            Q37=sQuery(id+"F3.wireOp",VERTEX,"E18.6.0.16");
            var Q38;
            Q38=sQuery(id+"F3.wireOp",VERTEX,"E18.9.0.39");
            var Q39;
            Q39=sQuery(id+"F3.wireOp",VERTEX,"E18.9.0.23");
            var Q40;
            Q40=sQuery(id+"F3.wireOp",VERTEX,"E18.7.0.23");
            var Q41;
            Q41=sQuery(id+"F3.wireOp",VERTEX,"E18.7.0.39");
            var Q42;
            Q42=sQuery(id+"F3.wireOp",VERTEX,"E18.8.0.31");
            var Q43;
            Q43=sQuery(id+"F3.wireOp",VERTEX,"E18.5.0.39");
            var Q44;
            Q44=sQuery(id+"F3.wireOp",VERTEX,"E18.6.0.31");
            var Q45;
            Q45=sQuery(id+"F3.wireOp",VERTEX,"E18.5.0.23");
            var Q46;
            Q46=sQuery(id+"F3.wireOp",VERTEX,"E18.9.0.6");
            var Q47;
            Q47=sQuery(id+"F3.wireOp",VERTEX,"E18.9.0.22");
            var Q48;
            Q48=sQuery(id+"F3.wireOp",VERTEX,"E18.7.0.22");
            var Q49;
            Q49=sQuery(id+"F3.wireOp",VERTEX,"E18.8.0.30");
            var Q50;
            Q50=sQuery(id+"F3.wireOp",VERTEX,"E18.6.0.30");
            var Q51;
            Q51=sQuery(id+"F3.wireOp",VERTEX,"E18.7.0.6");
            var Q52;
            Q52=sQuery(id+"F3.wireOp",VERTEX,"E18.5.0.6");
            var Q53;
            Q53=sQuery(id+"F3.wireOp",VERTEX,"E18.5.0.22");
            var Q54;
            Q54=sQuery(id+"F3.wireOp",VERTEX,"E18.9.0.37");
            var Q55;
            Q55=sQuery(id+"F3.wireOp",VERTEX,"E18.7.0.37");
            var Q56;
            Q56=sQuery(id+"F3.wireOp",VERTEX,"E18.5.0.37");
            var Q57;
            Q57=sQuery(id+"F3.wireOp",VERTEX,"E18.9.0.4");
            var Q58;
            Q58=sQuery(id+"F3.wireOp",VERTEX,"E18.9.0.20");
            var Q59;
            Q59=sQuery(id+"F3.wireOp",VERTEX,"E18.7.0.20");
            var Q60;
            Q60=sQuery(id+"F3.wireOp",VERTEX,"E18.7.0.4");
            var Q61;
            Q61=sQuery(id+"F3.wireOp",VERTEX,"E18.5.0.4");
            var Q62;
            Q62=sQuery(id+"F3.wireOp",VERTEX,"E18.5.0.20");
            var Q63;
            Q63=sQuery(id+"F3.wireOp",VERTEX,"E18.9.0.35");
            var Q64;
            Q64=sQuery(id+"F3.wireOp",VERTEX,"E18.9.0.3");
            var Q65;
            Q65=sQuery(id+"F3.wireOp",VERTEX,"E18.9.0.19");
            var Q66;
            Q66=sQuery(id+"F3.wireOp",VERTEX,"E18.7.0.19");
            var Q67;
            Q67=sQuery(id+"F3.wireOp",VERTEX,"E18.7.0.35");
            var Q68;
            Q68=sQuery(id+"F3.wireOp",VERTEX,"E18.5.0.35");
            var Q69;
            Q69=sQuery(id+"F3.wireOp",VERTEX,"E18.7.0.3");
            var Q70;
            Q70=sQuery(id+"F3.wireOp",VERTEX,"E18.5.0.3");
            var Q71;
            Q71=sQuery(id+"F3.wireOp",VERTEX,"E18.5.0.19");
            var Q72;
            Q72=sQuery(id+"F3.wireOp",VERTEX,"E18.9.0.2");
            var Q73;
            Q73=sQuery(id+"F3.wireOp",VERTEX,"E18.8.0.26");
            var Q74;
            Q74=sQuery(id+"F3.wireOp",VERTEX,"E18.6.0.26");
            var Q75;
            Q75=sQuery(id+"F3.wireOp",VERTEX,"E18.7.0.2");
            var Q76;
            Q76=sQuery(id+"F3.wireOp",VERTEX,"E18.5.0.2");
            var Q77;
            Q77=sQuery(id+"F3.wireOp",VERTEX,"E18.9.0.17");
            var Q78;
            Q78=sQuery(id+"F3.wireOp",VERTEX,"E18.9.0.1");
            var Q79;
            Q79=sQuery(id+"F3.wireOp",VERTEX,"E18.7.0.17");
            var Q80;
            Q80=sQuery(id+"F3.wireOp",VERTEX,"E18.8.0.9");
            var Q81;
            Q81=sQuery(id+"F3.wireOp",VERTEX,"E18.8.0.25");
            var Q82;
            Q82=sQuery(id+"F3.wireOp",VERTEX,"E18.6.0.9");
            var Q83;
            Q83=sQuery(id+"F3.wireOp",VERTEX,"E18.6.0.25");
            var Q84;
            Q84=sQuery(id+"F3.wireOp",VERTEX,"E18.7.0.1");
            var Q85;
            Q85=sQuery(id+"F3.wireOp",VERTEX,"E18.5.0.1");
            var Q86;
            Q86=sQuery(id+"F3.wireOp",VERTEX,"E18.5.0.17");
            var Q87;
            Q87=sQuery(id+"F3.wireOp",VERTEX,"E18.9.0.16");
            var Q88;
            Q88=sQuery(id+"F3.wireOp",VERTEX,"E18.9.0.0");
            var Q89;
            Q89=sQuery(id+"F3.wireOp",VERTEX,"E18.7.0.16");
            var Q90;
            Q90=sQuery(id+"F3.wireOp",VERTEX,"E18.7.0.0");
            var Q91;
            Q91=sQuery(id+"F3.wireOp",VERTEX,"E18.5.0.0");
            var Q92;
            Q92=sQuery(id+"F3.wireOp",VERTEX,"E18.5.0.16");
            var Q93;
            Q93=sQuery(id+"F3.wireOp",VERTEX,"E18.9.0.31");
            var Q94;
            Q94=sQuery(id+"F3.wireOp",VERTEX,"E18.8.0.39");
            var Q95;
            Q95=sQuery(id+"F3.wireOp",VERTEX,"E18.7.0.31");
            var Q96;
            Q96=sQuery(id+"F3.wireOp",VERTEX,"E18.8.0.23");
            var Q97;
            Q97=sQuery(id+"F3.wireOp",VERTEX,"E18.5.0.31");
            var Q98;
            Q98=sQuery(id+"F3.wireOp",VERTEX,"E18.6.0.23");
            var Q99;
            Q99=sQuery(id+"F3.wireOp",VERTEX,"E18.6.0.39");
            var Q100;
            Q100=makeQuery(id+"F1.opExtrude","SWEPT_BODY",BODY,{"disambiguationData":[OSD([sQuery(id+"F0.wireOp",EDGE,"E0.bottom"),sQuery(id+"F0.wireOp",EDGE,"E0.top"),sQuery(id+"F0.wireOp",EDGE,"E0.left"),sQuery(id+"F0.wireOp",EDGE,"E0.right"),sQuery(id+"F0.wireOp",EDGE,"E1"),sQuery(id+"F0.wireOp",EDGE,"E2"),sQuery(id+"F0.wireOp",EDGE,"E3"),sQuery(id+"F0.wireOp",EDGE,"E4")])]});
            hole(context, id + "F10", {"style" : HoleStyle.SIMPLE, "endStyle" : HoleEndStyle.BLIND, "holeDiameter" : 1 * mm, "majorDiameter" : 5 * mm, "holeDepth" : 3 * mm, "isTappedThrough" : true, "tappedDepth" : 12 * mm, "tapClearance" : 3, "locations" : qUnion([Q0, Q1, Q2, Q3, Q4, Q5, Q6, Q7, Q8, Q9, Q10, Q11, Q12, Q13, Q14, Q15, Q16, Q17, Q18, Q19, Q20, Q21, Q22, Q23, Q24, Q25, Q26, Q27, Q28, Q29, Q30, Q31, Q32, Q33, Q34, Q35, Q36, Q37, Q38, Q39, Q40, Q41, Q42, Q43, Q44, Q45, Q46, Q47, Q48, Q49, Q50, Q51, Q52, Q53, Q54, Q55, Q56, Q57, Q58, Q59, Q60, Q61, Q62, Q63, Q64, Q65, Q66, Q67, Q68, Q69, Q70, Q71, Q72, Q73, Q74, Q75, Q76, Q77, Q78, Q79, Q80, Q81, Q82, Q83, Q84, Q85, Q86, Q87, Q88, Q89, Q90, Q91, Q92, Q93, Q94, Q95, Q96, Q97, Q98, Q99]), "scope" : qUnion([Q100])});
        }
        {
            var Q0;
            Q0=sQuery(id+"F3.wireOp",VERTEX,"E18.14.0.6");
            var Q1;
            Q1=sQuery(id+"F3.wireOp",VERTEX,"E18.14.0.22");
            var Q2;
            Q2=sQuery(id+"F3.wireOp",VERTEX,"E18.12.0.22");
            var Q3;
            Q3=sQuery(id+"F3.wireOp",VERTEX,"E18.13.0.30");
            var Q4;
            Q4=sQuery(id+"F3.wireOp",VERTEX,"E18.11.0.30");
            var Q5;
            Q5=sQuery(id+"F3.wireOp",VERTEX,"E18.12.0.6");
            var Q6;
            Q6=sQuery(id+"F3.wireOp",VERTEX,"E18.10.0.6");
            var Q7;
            Q7=sQuery(id+"F3.wireOp",VERTEX,"E18.10.0.22");
            var Q8;
            Q8=sQuery(id+"F3.wireOp",VERTEX,"E18.14.0.37");
            var Q9;
            Q9=sQuery(id+"F3.wireOp",VERTEX,"E18.12.0.37");
            var Q10;
            Q10=sQuery(id+"F3.wireOp",VERTEX,"E18.10.0.37");
            var Q11;
            Q11=sQuery(id+"F3.wireOp",VERTEX,"E18.14.0.4");
            var Q12;
            Q12=sQuery(id+"F3.wireOp",VERTEX,"E18.14.0.20");
            var Q13;
            Q13=sQuery(id+"F3.wireOp",VERTEX,"E18.12.0.20");
            var Q14;
            Q14=sQuery(id+"F3.wireOp",VERTEX,"E18.12.0.4");
            var Q15;
            Q15=sQuery(id+"F3.wireOp",VERTEX,"E18.10.0.4");
            var Q16;
            Q16=sQuery(id+"F3.wireOp",VERTEX,"E18.10.0.20");
            var Q17;
            Q17=sQuery(id+"F3.wireOp",VERTEX,"E18.14.0.3");
            var Q18;
            Q18=sQuery(id+"F3.wireOp",VERTEX,"E18.14.0.19");
            var Q19;
            Q19=sQuery(id+"F3.wireOp",VERTEX,"E18.14.0.35");
            var Q20;
            Q20=sQuery(id+"F3.wireOp",VERTEX,"E18.12.0.19");
            var Q21;
            Q21=sQuery(id+"F3.wireOp",VERTEX,"E18.12.0.35");
            var Q22;
            Q22=sQuery(id+"F3.wireOp",VERTEX,"E18.10.0.35");
            var Q23;
            Q23=sQuery(id+"F3.wireOp",VERTEX,"E18.12.0.3");
            var Q24;
            Q24=sQuery(id+"F3.wireOp",VERTEX,"E18.10.0.3");
            var Q25;
            Q25=sQuery(id+"F3.wireOp",VERTEX,"E18.10.0.19");
            var Q26;
            Q26=sQuery(id+"F3.wireOp",VERTEX,"E18.14.0.2");
            var Q27;
            Q27=sQuery(id+"F3.wireOp",VERTEX,"E18.13.0.26");
            var Q28;
            Q28=sQuery(id+"F3.wireOp",VERTEX,"E18.11.0.26");
            var Q29;
            Q29=sQuery(id+"F3.wireOp",VERTEX,"E18.12.0.2");
            var Q30;
            Q30=sQuery(id+"F3.wireOp",VERTEX,"E18.10.0.2");
            var Q31;
            Q31=sQuery(id+"F3.wireOp",VERTEX,"E18.14.0.1");
            var Q32;
            Q32=sQuery(id+"F3.wireOp",VERTEX,"E18.14.0.17");
            var Q33;
            Q33=sQuery(id+"F3.wireOp",VERTEX,"E18.12.0.17");
            var Q34;
            Q34=sQuery(id+"F3.wireOp",VERTEX,"E18.13.0.9");
            var Q35;
            Q35=sQuery(id+"F3.wireOp",VERTEX,"E18.13.0.25");
            var Q36;
            Q36=sQuery(id+"F3.wireOp",VERTEX,"E18.11.0.9");
            var Q37;
            Q37=sQuery(id+"F3.wireOp",VERTEX,"E18.11.0.25");
            var Q38;
            Q38=sQuery(id+"F3.wireOp",VERTEX,"E18.12.0.1");
            var Q39;
            Q39=sQuery(id+"F3.wireOp",VERTEX,"E18.10.0.1");
            var Q40;
            Q40=sQuery(id+"F3.wireOp",VERTEX,"E18.10.0.17");
            var Q41;
            Q41=sQuery(id+"F3.wireOp",VERTEX,"E18.14.0.0");
            var Q42;
            Q42=sQuery(id+"F3.wireOp",VERTEX,"E18.14.0.16");
            var Q43;
            Q43=sQuery(id+"F3.wireOp",VERTEX,"E18.12.0.0");
            var Q44;
            Q44=sQuery(id+"F3.wireOp",VERTEX,"E18.12.0.16");
            var Q45;
            Q45=sQuery(id+"F3.wireOp",VERTEX,"E18.10.0.0");
            var Q46;
            Q46=sQuery(id+"F3.wireOp",VERTEX,"E18.10.0.16");
            var Q47;
            Q47=sQuery(id+"F3.wireOp",VERTEX,"E18.14.0.31");
            var Q48;
            Q48=sQuery(id+"F3.wireOp",VERTEX,"E18.13.0.23");
            var Q49;
            Q49=sQuery(id+"F3.wireOp",VERTEX,"E18.13.0.39");
            var Q50;
            Q50=sQuery(id+"F3.wireOp",VERTEX,"E18.11.0.23");
            var Q51;
            Q51=sQuery(id+"F3.wireOp",VERTEX,"E18.11.0.39");
            var Q52;
            Q52=sQuery(id+"F3.wireOp",VERTEX,"E18.12.0.31");
            var Q53;
            Q53=sQuery(id+"F3.wireOp",VERTEX,"E18.10.0.31");
            var Q54;
            Q54=sQuery(id+"F3.wireOp",VERTEX,"E18.14.0.30");
            var Q55;
            Q55=sQuery(id+"F3.wireOp",VERTEX,"E18.13.0.6");
            var Q56;
            Q56=sQuery(id+"F3.wireOp",VERTEX,"E18.13.0.22");
            var Q57;
            Q57=sQuery(id+"F3.wireOp",VERTEX,"E18.11.0.22");
            var Q58;
            Q58=sQuery(id+"F3.wireOp",VERTEX,"E18.12.0.30");
            var Q59;
            Q59=sQuery(id+"F3.wireOp",VERTEX,"E18.10.0.30");
            var Q60;
            Q60=sQuery(id+"F3.wireOp",VERTEX,"E18.11.0.6");
            var Q61;
            Q61=sQuery(id+"F3.wireOp",VERTEX,"E18.13.0.37");
            var Q62;
            Q62=sQuery(id+"F3.wireOp",VERTEX,"E18.11.0.37");
            var Q63;
            Q63=sQuery(id+"F3.wireOp",VERTEX,"E18.11.0.20");
            var Q64;
            Q64=sQuery(id+"F3.wireOp",VERTEX,"E18.11.0.4");
            var Q65;
            Q65=sQuery(id+"F3.wireOp",VERTEX,"E18.13.0.4");
            var Q66;
            Q66=sQuery(id+"F3.wireOp",VERTEX,"E18.13.0.20");
            var Q67;
            Q67=sQuery(id+"F3.wireOp",VERTEX,"E18.11.0.3");
            var Q68;
            Q68=sQuery(id+"F3.wireOp",VERTEX,"E18.13.0.3");
            var Q69;
            Q69=sQuery(id+"F3.wireOp",VERTEX,"E18.13.0.19");
            var Q70;
            Q70=sQuery(id+"F3.wireOp",VERTEX,"E18.13.0.35");
            var Q71;
            Q71=sQuery(id+"F3.wireOp",VERTEX,"E18.11.0.19");
            var Q72;
            Q72=sQuery(id+"F3.wireOp",VERTEX,"E18.11.0.35");
            var Q73;
            Q73=sQuery(id+"F3.wireOp",VERTEX,"E18.14.0.26");
            var Q74;
            Q74=sQuery(id+"F3.wireOp",VERTEX,"E18.13.0.2");
            var Q75;
            Q75=sQuery(id+"F3.wireOp",VERTEX,"E18.12.0.26");
            var Q76;
            Q76=sQuery(id+"F3.wireOp",VERTEX,"E18.10.0.26");
            var Q77;
            Q77=sQuery(id+"F3.wireOp",VERTEX,"E18.11.0.2");
            var Q78;
            Q78=sQuery(id+"F3.wireOp",VERTEX,"E18.14.0.25");
            var Q79;
            Q79=sQuery(id+"F3.wireOp",VERTEX,"E18.13.0.1");
            var Q80;
            Q80=sQuery(id+"F3.wireOp",VERTEX,"E18.13.0.17");
            var Q81;
            Q81=sQuery(id+"F3.wireOp",VERTEX,"E18.14.0.9");
            var Q82;
            Q82=sQuery(id+"F3.wireOp",VERTEX,"E18.11.0.17");
            var Q83;
            Q83=sQuery(id+"F3.wireOp",VERTEX,"E18.12.0.9");
            var Q84;
            Q84=sQuery(id+"F3.wireOp",VERTEX,"E18.12.0.25");
            var Q85;
            Q85=sQuery(id+"F3.wireOp",VERTEX,"E18.10.0.9");
            var Q86;
            Q86=sQuery(id+"F3.wireOp",VERTEX,"E18.10.0.25");
            var Q87;
            Q87=sQuery(id+"F3.wireOp",VERTEX,"E18.11.0.1");
            var Q88;
            Q88=sQuery(id+"F3.wireOp",VERTEX,"E18.13.0.0");
            var Q89;
            Q89=sQuery(id+"F3.wireOp",VERTEX,"E18.13.0.16");
            var Q90;
            Q90=sQuery(id+"F3.wireOp",VERTEX,"E18.11.0.16");
            var Q91;
            Q91=sQuery(id+"F3.wireOp",VERTEX,"E18.11.0.0");
            var Q92;
            Q92=sQuery(id+"F3.wireOp",VERTEX,"E18.14.0.23");
            var Q93;
            Q93=sQuery(id+"F3.wireOp",VERTEX,"E18.14.0.39");
            var Q94;
            Q94=sQuery(id+"F3.wireOp",VERTEX,"E18.12.0.39");
            var Q95;
            Q95=sQuery(id+"F3.wireOp",VERTEX,"E18.13.0.31");
            var Q96;
            Q96=sQuery(id+"F3.wireOp",VERTEX,"E18.11.0.31");
            var Q97;
            Q97=sQuery(id+"F3.wireOp",VERTEX,"E18.12.0.23");
            var Q98;
            Q98=sQuery(id+"F3.wireOp",VERTEX,"E18.10.0.23");
            var Q99;
            Q99=sQuery(id+"F3.wireOp",VERTEX,"E18.10.0.39");
            var Q100;
            Q100=makeQuery(id+"F1.opExtrude","SWEPT_BODY",BODY,{"disambiguationData":[OSD([sQuery(id+"F0.wireOp",EDGE,"E0.bottom"),sQuery(id+"F0.wireOp",EDGE,"E0.top"),sQuery(id+"F0.wireOp",EDGE,"E0.left"),sQuery(id+"F0.wireOp",EDGE,"E0.right"),sQuery(id+"F0.wireOp",EDGE,"E1"),sQuery(id+"F0.wireOp",EDGE,"E2"),sQuery(id+"F0.wireOp",EDGE,"E3"),sQuery(id+"F0.wireOp",EDGE,"E4")])]});
            hole(context, id + "F11", {"style" : HoleStyle.SIMPLE, "endStyle" : HoleEndStyle.BLIND, "holeDiameter" : 1 * mm, "majorDiameter" : 5 * mm, "holeDepth" : 3 * mm, "isTappedThrough" : true, "tappedDepth" : 12 * mm, "tapClearance" : 3, "locations" : qUnion([Q0, Q1, Q2, Q3, Q4, Q5, Q6, Q7, Q8, Q9, Q10, Q11, Q12, Q13, Q14, Q15, Q16, Q17, Q18, Q19, Q20, Q21, Q22, Q23, Q24, Q25, Q26, Q27, Q28, Q29, Q30, Q31, Q32, Q33, Q34, Q35, Q36, Q37, Q38, Q39, Q40, Q41, Q42, Q43, Q44, Q45, Q46, Q47, Q48, Q49, Q50, Q51, Q52, Q53, Q54, Q55, Q56, Q57, Q58, Q59, Q60, Q61, Q62, Q63, Q64, Q65, Q66, Q67, Q68, Q69, Q70, Q71, Q72, Q73, Q74, Q75, Q76, Q77, Q78, Q79, Q80, Q81, Q82, Q83, Q84, Q85, Q86, Q87, Q88, Q89, Q90, Q91, Q92, Q93, Q94, Q95, Q96, Q97, Q98, Q99]), "scope" : qUnion([Q100])});
        }
        {
            var Q0;
            Q0=sQuery(id+"F3.wireOp",VERTEX,"E18.17.0.30");
            var Q1;
            Q1=sQuery(id+"F3.wireOp",VERTEX,"E18.18.0.6");
            var Q2;
            Q2=sQuery(id+"F3.wireOp",VERTEX,"E18.18.0.22");
            var Q3;
            Q3=sQuery(id+"F3.wireOp",VERTEX,"E18.15.0.30");
            var Q4;
            Q4=sQuery(id+"F3.wireOp",VERTEX,"E18.16.0.6");
            var Q5;
            Q5=sQuery(id+"F3.wireOp",VERTEX,"E18.16.0.22");
            var Q6;
            Q6=sQuery(id+"F3.wireOp",VERTEX,"E18.18.0.37");
            var Q7;
            Q7=sQuery(id+"F3.wireOp",VERTEX,"E18.19.0.30");
            var Q8;
            Q8=sQuery(id+"F3.wireOp",VERTEX,"E18.16.0.37");
            var Q9;
            Q9=sQuery(id+"F3.wireOp",VERTEX,"E18.18.0.4");
            var Q10;
            Q10=sQuery(id+"F3.wireOp",VERTEX,"E18.18.0.20");
            var Q11;
            Q11=sQuery(id+"F3.wireOp",VERTEX,"E18.16.0.4");
            var Q12;
            Q12=sQuery(id+"F3.wireOp",VERTEX,"E18.16.0.20");
            var Q13;
            Q13=sQuery(id+"F3.wireOp",VERTEX,"E18.18.0.35");
            var Q14;
            Q14=sQuery(id+"F3.wireOp",VERTEX,"E18.18.0.3");
            var Q15;
            Q15=sQuery(id+"F3.wireOp",VERTEX,"E18.18.0.19");
            var Q16;
            Q16=sQuery(id+"F3.wireOp",VERTEX,"E18.16.0.3");
            var Q17;
            Q17=sQuery(id+"F3.wireOp",VERTEX,"E18.16.0.19");
            var Q18;
            Q18=sQuery(id+"F3.wireOp",VERTEX,"E18.16.0.35");
            var Q19;
            Q19=sQuery(id+"F3.wireOp",VERTEX,"E18.17.0.26");
            var Q20;
            Q20=sQuery(id+"F3.wireOp",VERTEX,"E18.18.0.2");
            var Q21;
            Q21=sQuery(id+"F3.wireOp",VERTEX,"E18.15.0.26");
            var Q22;
            Q22=sQuery(id+"F3.wireOp",VERTEX,"E18.16.0.2");
            var Q23;
            Q23=sQuery(id+"F3.wireOp",VERTEX,"E18.19.0.26");
            var Q24;
            Q24=sQuery(id+"F3.wireOp",VERTEX,"E18.19.0.9");
            var Q25;
            Q25=sQuery(id+"F3.wireOp",VERTEX,"E18.17.0.9");
            var Q26;
            Q26=sQuery(id+"F3.wireOp",VERTEX,"E18.17.0.25");
            var Q27;
            Q27=sQuery(id+"F3.wireOp",VERTEX,"E18.18.0.1");
            var Q28;
            Q28=sQuery(id+"F3.wireOp",VERTEX,"E18.18.0.17");
            var Q29;
            Q29=sQuery(id+"F3.wireOp",VERTEX,"E18.15.0.25");
            var Q30;
            Q30=sQuery(id+"F3.wireOp",VERTEX,"E18.16.0.1");
            var Q31;
            Q31=sQuery(id+"F3.wireOp",VERTEX,"E18.16.0.17");
            var Q32;
            Q32=sQuery(id+"F3.wireOp",VERTEX,"E18.15.0.9");
            var Q33;
            Q33=sQuery(id+"F3.wireOp",VERTEX,"E18.19.0.25");
            var Q34;
            Q34=sQuery(id+"F3.wireOp",VERTEX,"E18.18.0.0");
            var Q35;
            Q35=sQuery(id+"F3.wireOp",VERTEX,"E18.18.0.16");
            var Q36;
            Q36=sQuery(id+"F3.wireOp",VERTEX,"E18.16.0.16");
            var Q37;
            Q37=sQuery(id+"F3.wireOp",VERTEX,"E18.16.0.0");
            var Q38;
            Q38=sQuery(id+"F3.wireOp",VERTEX,"E18.16.0.31");
            var Q39;
            Q39=sQuery(id+"F3.wireOp",VERTEX,"E18.17.0.23");
            var Q40;
            Q40=sQuery(id+"F3.wireOp",VERTEX,"E18.15.0.23");
            var Q41;
            Q41=sQuery(id+"F3.wireOp",VERTEX,"E18.15.0.39");
            var Q42;
            Q42=sQuery(id+"F3.wireOp",VERTEX,"E18.17.0.39");
            var Q43;
            Q43=sQuery(id+"F3.wireOp",VERTEX,"E18.18.0.31");
            var Q44;
            Q44=sQuery(id+"F3.wireOp",VERTEX,"E18.19.0.23");
            var Q45;
            Q45=sQuery(id+"F3.wireOp",VERTEX,"E18.19.0.39");
            var Q46;
            Q46=sQuery(id+"F3.wireOp",VERTEX,"E18.15.0.6");
            var Q47;
            Q47=sQuery(id+"F3.wireOp",VERTEX,"E18.15.0.22");
            var Q48;
            Q48=sQuery(id+"F3.wireOp",VERTEX,"E18.18.0.30");
            var Q49;
            Q49=sQuery(id+"F3.wireOp",VERTEX,"E18.19.0.6");
            var Q50;
            Q50=sQuery(id+"F3.wireOp",VERTEX,"E18.16.0.30");
            var Q51;
            Q51=sQuery(id+"F3.wireOp",VERTEX,"E18.17.0.6");
            var Q52;
            Q52=sQuery(id+"F3.wireOp",VERTEX,"E18.17.0.22");
            var Q53;
            Q53=sQuery(id+"F3.wireOp",VERTEX,"E18.19.0.22");
            var Q54;
            Q54=sQuery(id+"F3.wireOp",VERTEX,"E18.17.0.37");
            var Q55;
            Q55=sQuery(id+"F3.wireOp",VERTEX,"E18.15.0.37");
            var Q56;
            Q56=sQuery(id+"F3.wireOp",VERTEX,"E18.19.0.37");
            var Q57;
            Q57=sQuery(id+"F3.wireOp",VERTEX,"E18.19.0.4");
            var Q58;
            Q58=sQuery(id+"F3.wireOp",VERTEX,"E18.17.0.4");
            var Q59;
            Q59=sQuery(id+"F3.wireOp",VERTEX,"E18.17.0.20");
            var Q60;
            Q60=sQuery(id+"F3.wireOp",VERTEX,"E18.15.0.4");
            var Q61;
            Q61=sQuery(id+"F3.wireOp",VERTEX,"E18.15.0.20");
            var Q62;
            Q62=sQuery(id+"F3.wireOp",VERTEX,"E18.19.0.20");
            var Q63;
            Q63=sQuery(id+"F3.wireOp",VERTEX,"E18.17.0.35");
            var Q64;
            Q64=sQuery(id+"F3.wireOp",VERTEX,"E18.19.0.3");
            var Q65;
            Q65=sQuery(id+"F3.wireOp",VERTEX,"E18.17.0.3");
            var Q66;
            Q66=sQuery(id+"F3.wireOp",VERTEX,"E18.17.0.19");
            var Q67;
            Q67=sQuery(id+"F3.wireOp",VERTEX,"E18.15.0.3");
            var Q68;
            Q68=sQuery(id+"F3.wireOp",VERTEX,"E18.15.0.19");
            var Q69;
            Q69=sQuery(id+"F3.wireOp",VERTEX,"E18.15.0.35");
            var Q70;
            Q70=sQuery(id+"F3.wireOp",VERTEX,"E18.19.0.19");
            var Q71;
            Q71=sQuery(id+"F3.wireOp",VERTEX,"E18.19.0.35");
            var Q72;
            Q72=sQuery(id+"F3.wireOp",VERTEX,"E18.18.0.26");
            var Q73;
            Q73=sQuery(id+"F3.wireOp",VERTEX,"E18.19.0.2");
            var Q74;
            Q74=sQuery(id+"F3.wireOp",VERTEX,"E18.16.0.26");
            var Q75;
            Q75=sQuery(id+"F3.wireOp",VERTEX,"E18.17.0.2");
            var Q76;
            Q76=sQuery(id+"F3.wireOp",VERTEX,"E18.15.0.2");
            var Q77;
            Q77=sQuery(id+"F3.wireOp",VERTEX,"E18.18.0.9");
            var Q78;
            Q78=sQuery(id+"F3.wireOp",VERTEX,"E18.18.0.25");
            var Q79;
            Q79=sQuery(id+"F3.wireOp",VERTEX,"E18.19.0.1");
            var Q80;
            Q80=sQuery(id+"F3.wireOp",VERTEX,"E18.16.0.9");
            var Q81;
            Q81=sQuery(id+"F3.wireOp",VERTEX,"E18.16.0.25");
            var Q82;
            Q82=sQuery(id+"F3.wireOp",VERTEX,"E18.17.0.1");
            var Q83;
            Q83=sQuery(id+"F3.wireOp",VERTEX,"E18.17.0.17");
            var Q84;
            Q84=sQuery(id+"F3.wireOp",VERTEX,"E18.15.0.1");
            var Q85;
            Q85=sQuery(id+"F3.wireOp",VERTEX,"E18.15.0.17");
            var Q86;
            Q86=sQuery(id+"F3.wireOp",VERTEX,"E18.19.0.17");
            var Q87;
            Q87=sQuery(id+"F3.wireOp",VERTEX,"E18.17.0.0");
            var Q88;
            Q88=sQuery(id+"F3.wireOp",VERTEX,"E18.17.0.16");
            var Q89;
            Q89=sQuery(id+"F3.wireOp",VERTEX,"E18.15.0.0");
            var Q90;
            Q90=sQuery(id+"F3.wireOp",VERTEX,"E18.15.0.16");
            var Q91;
            Q91=sQuery(id+"F3.wireOp",VERTEX,"E18.19.0.16");
            var Q92;
            Q92=sQuery(id+"F3.wireOp",VERTEX,"E18.19.0.0");
            var Q93;
            Q93=sQuery(id+"F3.wireOp",VERTEX,"E18.15.0.31");
            var Q94;
            Q94=sQuery(id+"F3.wireOp",VERTEX,"E18.17.0.31");
            var Q95;
            Q95=sQuery(id+"F3.wireOp",VERTEX,"E18.18.0.23");
            var Q96;
            Q96=sQuery(id+"F3.wireOp",VERTEX,"E18.18.0.39");
            var Q97;
            Q97=sQuery(id+"F3.wireOp",VERTEX,"E18.16.0.23");
            var Q98;
            Q98=sQuery(id+"F3.wireOp",VERTEX,"E18.16.0.39");
            var Q99;
            Q99=sQuery(id+"F3.wireOp",VERTEX,"E18.19.0.31");
            var Q100;
            Q100=makeQuery(id+"F1.opExtrude","SWEPT_BODY",BODY,{"disambiguationData":[OSD([sQuery(id+"F0.wireOp",EDGE,"E0.bottom"),sQuery(id+"F0.wireOp",EDGE,"E0.top"),sQuery(id+"F0.wireOp",EDGE,"E0.left"),sQuery(id+"F0.wireOp",EDGE,"E0.right"),sQuery(id+"F0.wireOp",EDGE,"E1"),sQuery(id+"F0.wireOp",EDGE,"E2"),sQuery(id+"F0.wireOp",EDGE,"E3"),sQuery(id+"F0.wireOp",EDGE,"E4")])]});
            hole(context, id + "F12", {"style" : HoleStyle.SIMPLE, "endStyle" : HoleEndStyle.BLIND, "holeDiameter" : 1 * mm, "majorDiameter" : 5 * mm, "holeDepth" : 3 * mm, "isTappedThrough" : true, "tappedDepth" : 12 * mm, "tapClearance" : 3, "locations" : qUnion([Q0, Q1, Q2, Q3, Q4, Q5, Q6, Q7, Q8, Q9, Q10, Q11, Q12, Q13, Q14, Q15, Q16, Q17, Q18, Q19, Q20, Q21, Q22, Q23, Q24, Q25, Q26, Q27, Q28, Q29, Q30, Q31, Q32, Q33, Q34, Q35, Q36, Q37, Q38, Q39, Q40, Q41, Q42, Q43, Q44, Q45, Q46, Q47, Q48, Q49, Q50, Q51, Q52, Q53, Q54, Q55, Q56, Q57, Q58, Q59, Q60, Q61, Q62, Q63, Q64, Q65, Q66, Q67, Q68, Q69, Q70, Q71, Q72, Q73, Q74, Q75, Q76, Q77, Q78, Q79, Q80, Q81, Q82, Q83, Q84, Q85, Q86, Q87, Q88, Q89, Q90, Q91, Q92, Q93, Q94, Q95, Q96, Q97, Q98, Q99]), "scope" : qUnion([Q100])});
        }
        {
            var Q0;
            Q0=makeQuery(id+"F0.imprint","IMPRINT",FACE,{"disambiguationData":[TD([[makeQuery(id+"F0.imprint","IMPRINT",EDGE,{"derivedFrom":sQuery(id+"F0.wireOp",EDGE,"E0.bottom")}),-1.0]])]});
            var sketch = newSketch(context, id + "F13", { "sketchPlane" : qUnion([Q0])});
            skLineSegment(sketch, "E19.0.0", {"start": v(50, 20) * mm, "end": v(35, 35) * mm});
            skLineSegment(sketch, "E19.0.1", {"start": v(35, 35) * mm, "end": v(-35, 35) * mm});
            skLineSegment(sketch, "E19.0.2", {"start": v(-35, 35) * mm, "end": v(-50, 20) * mm});
            skLineSegment(sketch, "E19.0.3", {"start": v(-50, 20) * mm, "end": v(-50, -20) * mm});
            skLineSegment(sketch, "E19.0.4", {"start": v(-50, -20) * mm, "end": v(-35, -35) * mm});
            skLineSegment(sketch, "E19.0.5", {"start": v(-35, -35) * mm, "end": v(35, -35) * mm});
            skLineSegment(sketch, "E19.0.6", {"start": v(35, -35) * mm, "end": v(50, -20) * mm});
            skLineSegment(sketch, "E19.0.7", {"start": v(50, -20) * mm, "end": v(50, 20) * mm});
            skCircle(sketch, "E20", {"center": v(-35, 27.5) * mm, "radius": 1.5 * mm});
            skPoint(sketch, "E20.centerSnap0", {"position": v(-42.5, 27.5) * mm});
            skCircle(sketch, "E21", {"center": v(35, 27.5) * mm, "radius": 1.5 * mm});
            skPoint(sketch, "E21.centerSnap0", {"position": v(42.5, 27.5) * mm});
            skCircle(sketch, "E22", {"center": v(-35, -27.5) * mm, "radius": 1.5 * mm});
            skPoint(sketch, "E22.centerSnap0", {"position": v(-42.5, -27.5) * mm});
            skCircle(sketch, "E23", {"center": v(35, -27.5) * mm, "radius": 1.5 * mm});
            skPoint(sketch, "E23.centerSnap0", {"position": v(42.5, -27.5) * mm});
            skSolve(sketch);
        }
        {
            var Q0;
            Q0=makeQuery(id+"F13.imprint","IMPRINT",FACE,{"disambiguationData":[TD([[makeQuery(id+"F13.imprint","IMPRINT",EDGE,{"derivedFrom":sQuery(id+"F13.wireOp",EDGE,"E20")}),1.0]])]});
            var Q1;
            Q1=makeQuery(id+"F13.imprint","IMPRINT",FACE,{"disambiguationData":[TD([[makeQuery(id+"F13.imprint","IMPRINT",EDGE,{"derivedFrom":sQuery(id+"F13.wireOp",EDGE,"E21")}),1.0]])]});
            var Q2;
            Q2=makeQuery(id+"F13.imprint","IMPRINT",FACE,{"disambiguationData":[TD([[makeQuery(id+"F13.imprint","IMPRINT",EDGE,{"derivedFrom":sQuery(id+"F13.wireOp",EDGE,"E22")}),1.0]])]});
            var Q3;
            Q3=makeQuery(id+"F13.imprint","IMPRINT",FACE,{"disambiguationData":[TD([[makeQuery(id+"F13.imprint","IMPRINT",EDGE,{"derivedFrom":sQuery(id+"F13.wireOp",EDGE,"E23")}),1.0]])]});
            var Q4;
            Q4=sQuery(id+"F13.wireOp",EDGE,"E20");
            extrude(context, id + "F14", {"entities" : qUnion([Q0, Q1, Q2, Q3]), "operationType" : NewBodyOperationType.ADD, "surfaceEntities" : qUnion([Q4]), "depth" : 1 * mm, "offsetDistance" : 25 * mm});
        }
        {
            var Q0;
            Q0=makeQuery(id+"F1.opExtrude","SWEPT_FACE",FACE,{"disambiguationData":[OSD([sQuery(id+"F0.wireOp",EDGE,"E0.top")])]});
            var sketch = newSketch(context, id + "F15", { "sketchPlane" : qUnion([Q0])});
            skLineSegment(sketch, "E24.0.0", {"start": v(34, 50) * mm, "end": v(-34, 50) * mm});
            skLineSegment(sketch, "E24.0.1", {"start": v(-34, 50) * mm, "end": v(-34, 0) * mm});
            skLineSegment(sketch, "E24.0.2", {"start": v(-34, 0) * mm, "end": v(34, 0) * mm});
            skLineSegment(sketch, "E24.0.3", {"start": v(34, 0) * mm, "end": v(34, 50) * mm});
            skLineSegment(sketch, "E25", {"start": v(-34, 20) * mm, "end": v(-10, 20) * mm});
            skLineSegment(sketch, "E26", {"start": v(-34, 30) * mm, "end": v(-10, 30) * mm});
            skLineSegment(sketch, "E27", {"start": v(34, 20) * mm, "end": v(10, 20) * mm});
            skLineSegment(sketch, "E28", {"start": v(10, 20) * mm, "end": v(10, 30) * mm});
            skLineSegment(sketch, "E29", {"start": v(10, 30) * mm, "end": v(34, 30) * mm});
            skLineSegment(sketch, "E30", {"start": v(-10, 20) * mm, "end": v(-10, 30) * mm});
            skArc(sketch, "E31", {"start": v(-10, 20) * mm, "mid": v(0, 10) * mm, "end": v(10, 20) * mm});
            skArc(sketch, "E32", {"start": v(-10, 30) * mm, "mid": v(0, 40) * mm, "end": v(10, 30) * mm});
            skSolve(sketch);
        }
        {
            var Q0;
            Q0=makeQuery(id+"F15.imprint","IMPRINT",FACE,{"disambiguationData":[TD([[makeQuery(id+"F15.imprint","IMPRINT",EDGE,{"derivedFrom":sQuery(id+"F15.wireOp",EDGE,"E28")}),1.0]])]});
            var Q1;
            {var subQ0=sQuery(id+"F15.wireOp",EDGE,"E25");Q1=makeQuery(id+"F15.imprint","IMPRINT",FACE,{"disambiguationData":[TD([[makeQuery(id+"F15.imprint","IMPRINT",EDGE,{"derivedFrom":subQ0}),1.0]])]});}
            var Q2;
            {var subQ0=sQuery(id+"F15.wireOp",EDGE,"E27");Q2=makeQuery(id+"F15.imprint","IMPRINT",FACE,{"disambiguationData":[TD([[makeQuery(id+"F15.imprint","IMPRINT",EDGE,{"derivedFrom":subQ0}),-1.0]])]});}
            extrude(context, id + "F16", {"entities" : qUnion([Q0, Q1, Q2]), "depth" : 1 * mm, "offsetDistance" : 25 * mm});
        }
        {
            var Q0;
            Q0=makeQuery(id+"F16.opExtrude","CAP_FACE",FACE,{"disambiguationData":[OSD([sQuery(id+"F15.wireOp",EDGE,"E24.0.1"),sQuery(id+"F15.wireOp",EDGE,"E24.0.3"),sQuery(id+"F15.wireOp",EDGE,"E25"),sQuery(id+"F15.wireOp",EDGE,"E26"),sQuery(id+"F15.wireOp",EDGE,"E27"),sQuery(id+"F15.wireOp",EDGE,"E29"),sQuery(id+"F15.wireOp",EDGE,"E31"),sQuery(id+"F15.wireOp",EDGE,"E32")])],"isStart":false});
            var sketch = newSketch(context, id + "F17", { "sketchPlane" : qUnion([Q0])});
            skLineSegment(sketch, "E33", {"start": v(-34, 25) * mm, "end": v(34, 25) * mm, "construction": true});
            skCircle(sketch, "E34", {"center": v(-27, 25) * mm, "radius": 3 * mm});
            skCircle(sketch, "E35", {"center": v(0, 25) * mm, "radius": 7.5 * mm});
            skCircle(sketch, "E36", {"center": v(27, 25) * mm, "radius": 3 * mm});
            skText(sketch, "E37", { "text": "+", "fontName": "OpenSans-Bold.ttf"});
            skText(sketch, "E38", { "text": "-", "fontName": "OpenSans-Bold.ttf"});
            skArc(sketch, "E39", {"start": v(-2.95, 25) * mm, "mid": v(-0.15, 20.23) * mm, "end": v(2.65, 25) * mm});
            skArc(sketch, "E40", {"start": v(-1.92, 25) * mm, "mid": v(-0.16, 21.17) * mm, "end": v(1.6, 25) * mm});
            skLineSegment(sketch, "E41.bottom", {"start": v(-0.42, 22.34) * mm, "end": v(0.42, 22.34) * mm});
            skLineSegment(sketch, "E41.top", {"start": v(-0.42, 27.66) * mm, "end": v(0.42, 27.66) * mm});
            skLineSegment(sketch, "E41.left", {"start": v(-0.42, 22.34) * mm, "end": v(-0.42, 27.66) * mm});
            skLineSegment(sketch, "E41.right", {"start": v(0.42, 22.34) * mm, "end": v(0.42, 27.66) * mm});
            skLineSegment(sketch, "E42", {"start": v(-2.95, 25) * mm, "end": v(-1.92, 25) * mm});
            skLineSegment(sketch, "E43", {"start": v(1.6, 25) * mm, "end": v(2.65, 25) * mm});
            const initialGuessF17  = {"E37": [-0.0282, 0.02339, 1, 0, 0.00306], "E38": [0.0264, 0.0237, 1, 0, 0.00348]};
            skSetInitialGuess(sketch, initialGuessF17);
            skSolve(sketch);
        }
        {
            var Q0;
            Q0=makeQuery(id+"F17.imprint","IMPRINT",FACE,{"disambiguationData":[TD([[makeQuery(id+"F17.imprint","IMPRINT",EDGE,{"derivedFrom":sQuery(id+"F17.wireOp",EDGE,"E34")}),1.0]])]});
            var Q1;
            Q1=makeQuery(id+"F17.imprint","IMPRINT",FACE,{"disambiguationData":[TD([[makeQuery(id+"F17.imprint","IMPRINT",EDGE,{"derivedFrom":sQuery(id+"F17.wireOp",EDGE,"E35")}),1.0]])]});
            var Q2;
            Q2=makeQuery(id+"F17.imprint","IMPRINT",FACE,{"disambiguationData":[TD([[makeQuery(id+"F17.imprint","IMPRINT",EDGE,{"derivedFrom":sQuery(id+"F17.wireOp",EDGE,"E36")}),1.0]])]});
            extrude(context, id + "F18", {"entities" : qUnion([Q0, Q1, Q2]), "operationType" : NewBodyOperationType.ADD, "depth" : 0.5 * mm, "offsetDistance" : 25 * mm});
        }
        {
            var Q0;
            Q0=makeQuery(id+"F1.opExtrude","SWEPT_FACE",FACE,{"disambiguationData":[OSD([sQuery(id+"F0.wireOp",EDGE,"E0.bottom")])]});
            var sketch = newSketch(context, id + "F19", { "sketchPlane" : qUnion([Q0])});
            skLineSegment(sketch, "E44.bottom", {"start": v(22.9, -16.63) * mm, "end": v(-26.64, -16.63) * mm});
            skLineSegment(sketch, "E44.top", {"start": v(22.9, -32.79) * mm, "end": v(-26.64, -32.79) * mm});
            skLineSegment(sketch, "E44.left", {"start": v(22.9, -16.63) * mm, "end": v(22.9, -32.79) * mm});
            skLineSegment(sketch, "E44.right", {"start": v(-26.64, -16.63) * mm, "end": v(-26.64, -32.79) * mm});
            skLineSegment(sketch, "E45", {"start": v(29, 0) * mm, "end": v(29, -50) * mm});
            skLineSegment(sketch, "E46", {"start": v(29, -50) * mm, "end": v(34, -50) * mm});
            skLineSegment(sketch, "E47", {"start": v(34, -50) * mm, "end": v(34, 0) * mm});
            skLineSegment(sketch, "E48", {"start": v(34, 0) * mm, "end": v(29, 0) * mm});
            skLineSegment(sketch, "E49", {"start": v(0, 0) * mm, "end": v(0, -50) * mm, "construction": true});
            skLineSegment(sketch, "E50.MirrorCS", {"start": v(-29, 0) * mm, "end": v(-29, -50) * mm});
            skLineSegment(sketch, "E51.MirrorCS", {"start": v(-34, 0) * mm, "end": v(-29, 0) * mm});
            skLineSegment(sketch, "E52.MirrorCS", {"start": v(-34, -50) * mm, "end": v(-34, 0) * mm});
            skLineSegment(sketch, "E53.MirrorCS", {"start": v(-29, -50) * mm, "end": v(-34, -50) * mm});
            skSolve(sketch);
        }
        {
            var Q0;
            Q0 = qSketchRegion(id + "F19", true);
            extrude(context, id + "F20", {"entities" : qUnion([Q0]), "operationType" : NewBodyOperationType.ADD, "depth" : 1 * mm, "offsetDistance" : 25 * mm});
        }
        {
            var Q0;
            Q0=makeQuery(id+"F20.opExtrude","CAP_FACE",FACE,{"disambiguationData":[OSD([sQuery(id+"F19.wireOp",EDGE,"E44.bottom"),sQuery(id+"F19.wireOp",EDGE,"E44.top"),sQuery(id+"F19.wireOp",EDGE,"E44.left"),sQuery(id+"F19.wireOp",EDGE,"E44.right")])],"isStart":false});
            var sketch = newSketch(context, id + "F21", { "sketchPlane" : qUnion([Q0])});
            skText(sketch, "E54", { "text": "MPOW", "fontName": "AllertaStencil-Regular.ttf"});
            const initialGuessF21  = {"E54": [-0.02277, -0.02942, 1, 0, 0.00901]};
            skSetInitialGuess(sketch, initialGuessF21);
            skSolve(sketch);
        }
        {
            var Q0;
            Q0 = qSketchRegion(id + "F21", true);
            extrude(context, id + "F22", {"entities" : qUnion([Q0]), "operationType" : NewBodyOperationType.REMOVE, "oppositeDirection" : true, "depth" : 1 * mm, "offsetDistance" : 25 * mm});
        }
        {
            var Q0;
            Q0=makeQuery(id+"F20.opExtrude","CAP_EDGE",EDGE,{"disambiguationData":[OSD([sQuery(id+"F19.wireOp",EDGE,"E52.MirrorCS")])],"isStart":false});
            var Q1;
            Q1=makeQuery(id+"F20.opExtrude","CAP_EDGE",EDGE,{"disambiguationData":[OSD([sQuery(id+"F19.wireOp",EDGE,"E50.MirrorCS")])],"isStart":false});
            var Q2;
            Q2=makeQuery(id+"F20.opExtrude","CAP_EDGE",EDGE,{"disambiguationData":[OSD([sQuery(id+"F19.wireOp",EDGE,"E45")])],"isStart":false});
            var Q3;
            Q3=makeQuery(id+"F20.opExtrude","CAP_EDGE",EDGE,{"disambiguationData":[OSD([sQuery(id+"F19.wireOp",EDGE,"E47")])],"isStart":false});
            fillet(context, id + "F23", {"entities" : qUnion([Q0, Q1, Q2, Q3]), "radius" : 1 * mm, "tangentPropagation" : true, "allowEdgeOverflow" : false});
        }
        {
            var Q0;
            Q0=makeQuery(id+"F1.opExtrude","SWEPT_FACE",FACE,{"disambiguationData":[OSD([sQuery(id+"F0.wireOp",EDGE,"E0.right")])]});
            var sketch = newSketch(context, id + "F24", { "sketchPlane" : qUnion([Q0])});
            skLineSegment(sketch, "E55", {"start": v(-25, 19) * mm, "end": v(-25, -19) * mm, "construction": true});
            skLineSegment(sketch, "E56", {"start": v(-50, 0) * mm, "end": v(0, 0) * mm, "construction": true});
            skLineSegment(sketch, "E57.bottom", {"start": v(-17.5, -13.5) * mm, "end": v(-32.5, -13.5) * mm});
            skLineSegment(sketch, "E57.top", {"start": v(-17.5, 13.5) * mm, "end": v(-32.5, 13.5) * mm});
            skLineSegment(sketch, "E57.left", {"start": v(-17.5, -13.5) * mm, "end": v(-17.5, 13.5) * mm});
            skLineSegment(sketch, "E57.right", {"start": v(-32.5, -13.5) * mm, "end": v(-32.5, 13.5) * mm});
            skPoint(sketch, "E57.middle", {"position": v(-25, 0) * mm});
            skLineSegment(sketch, "E58", {"start": v(-17.5, 5) * mm, "end": v(0, 5) * mm});
            skLineSegment(sketch, "E59", {"start": v(0, 5) * mm, "end": v(0, -5) * mm});
            skLineSegment(sketch, "E60", {"start": v(0, -5) * mm, "end": v(-17.5, -5) * mm});
            skLineSegment(sketch, "E61.MirrorCS", {"start": v(-32.5, 5) * mm, "end": v(-50, 5) * mm});
            skLineSegment(sketch, "E62.MirrorCS", {"start": v(-50, -5) * mm, "end": v(-32.5, -5) * mm});
            skLineSegment(sketch, "E63.MirrorCS", {"start": v(-50, 5) * mm, "end": v(-50, -5) * mm});
            skSolve(sketch);
        }
        {
            var Q0;
            Q0 = qSketchRegion(id + "F24", true);
            extrude(context, id + "F25", {"entities" : qUnion([Q0]), "operationType" : NewBodyOperationType.ADD, "depth" : 1.5 * mm, "offsetDistance" : 25 * mm});
        }
        {
            var Q0;
            Q0=makeQuery(id+"F25.opExtrude","CAP_FACE",FACE,{"disambiguationData":[OSD([sQuery(id+"F24.wireOp",EDGE,"E57.bottom"),sQuery(id+"F24.wireOp",EDGE,"E57.top"),sQuery(id+"F24.wireOp",EDGE,"E57.left"),sQuery(id+"F24.wireOp",EDGE,"E57.right"),sQuery(id+"F24.wireOp",EDGE,"E58"),sQuery(id+"F24.wireOp",EDGE,"E59"),sQuery(id+"F24.wireOp",EDGE,"E60"),sQuery(id+"F24.wireOp",EDGE,"E61.MirrorCS"),sQuery(id+"F24.wireOp",EDGE,"E62.MirrorCS"),sQuery(id+"F24.wireOp",EDGE,"E63.MirrorCS")])],"isStart":false});
            var sketch = newSketch(context, id + "F26", { "sketchPlane" : qUnion([Q0])});
            skText(sketch, "E64", { "text": "OPEN\n\n AUX\n\n USB", "fontName": "Arimo-Bold.ttf"});
            skPoint(sketch, "E65", {"position": v(-32.5, 9.25) * mm});
            const initialGuessF26  = {"E64": [-0.03045, 0.00647, 1, 0, 0.00285]};
            skSetInitialGuess(sketch, initialGuessF26);
            skSolve(sketch);
        }
        {
            var Q0;
            Q0 = qSketchRegion(id + "F26", true);
            extrude(context, id + "F27", {"entities" : qUnion([Q0]), "operationType" : NewBodyOperationType.REMOVE, "oppositeDirection" : true, "depth" : 1 * mm, "offsetDistance" : 25 * mm});
        }
        {
            var Q0;
            Q0=makeQuery(id+"F1.opExtrude","CAP_EDGE",EDGE,{"disambiguationData":[OSD([sQuery(id+"F0.wireOp",EDGE,"E0.top")])],"isStart":true});
            var Q1;
            Q1=makeQuery(id+"F1.opExtrude","CAP_EDGE",EDGE,{"disambiguationData":[OSD([sQuery(id+"F0.wireOp",EDGE,"E1")])],"isStart":true});
            var Q2;
            {var subQ1=sQuery(id+"F0.wireOp",EDGE,"E0.right");Q2=makeQuery(id+"F25.boolean.opBoolean","SPLIT",EDGE,{"disambiguationData":[TD([makeQuery(id+"F25.opExtrude","SWEPT_FACE",FACE,{"disambiguationData":[OSD([sQuery(id+"F24.wireOp",EDGE,"E58")])]})])],"derivedFrom":makeQuery(id+"F1.opExtrude","CAP_EDGE",EDGE,{"disambiguationData":[OSD([subQ1])],"isStart":true})});}
            var Q3;
            {var subQ1=sQuery(id+"F0.wireOp",EDGE,"E0.right");Q3=makeQuery(id+"F25.boolean.opBoolean","SPLIT",EDGE,{"disambiguationData":[TD([makeQuery(id+"F25.opExtrude","SWEPT_FACE",FACE,{"disambiguationData":[OSD([sQuery(id+"F24.wireOp",EDGE,"E60")])]})])],"derivedFrom":makeQuery(id+"F1.opExtrude","CAP_EDGE",EDGE,{"disambiguationData":[OSD([subQ1])],"isStart":true})});}
            var Q4;
            Q4=makeQuery(id+"F1.opExtrude","CAP_EDGE",EDGE,{"disambiguationData":[OSD([sQuery(id+"F0.wireOp",EDGE,"E2")])],"isStart":true});
            var Q5;
            Q5=makeQuery(id+"F1.opExtrude","CAP_EDGE",EDGE,{"disambiguationData":[OSD([sQuery(id+"F0.wireOp",EDGE,"E3")])],"isStart":true});
            var Q6;
            Q6=makeQuery(id+"F1.opExtrude","CAP_EDGE",EDGE,{"disambiguationData":[OSD([sQuery(id+"F0.wireOp",EDGE,"E0.left")])],"isStart":true});
            var Q7;
            Q7=makeQuery(id+"F1.opExtrude","CAP_EDGE",EDGE,{"disambiguationData":[OSD([sQuery(id+"F0.wireOp",EDGE,"E4")])],"isStart":true});
            var Q8;
            Q8=makeQuery(id+"F1.opExtrude","CAP_EDGE",EDGE,{"disambiguationData":[OSD([sQuery(id+"F0.wireOp",EDGE,"E1")])],"isStart":false});
            var Q9;
            Q9=makeQuery(id+"F1.opExtrude","CAP_EDGE",EDGE,{"disambiguationData":[OSD([sQuery(id+"F0.wireOp",EDGE,"E0.top")])],"isStart":false});
            var Q10;
            Q10=makeQuery(id+"F1.opExtrude","CAP_EDGE",EDGE,{"disambiguationData":[OSD([sQuery(id+"F0.wireOp",EDGE,"E4")])],"isStart":false});
            var Q11;
            Q11=makeQuery(id+"F1.opExtrude","CAP_EDGE",EDGE,{"disambiguationData":[OSD([sQuery(id+"F0.wireOp",EDGE,"E0.left")])],"isStart":false});
            var Q12;
            Q12=makeQuery(id+"F1.opExtrude","CAP_EDGE",EDGE,{"disambiguationData":[OSD([sQuery(id+"F0.wireOp",EDGE,"E3")])],"isStart":false});
            var Q13;
            Q13=makeQuery(id+"F1.opExtrude","CAP_EDGE",EDGE,{"disambiguationData":[OSD([sQuery(id+"F0.wireOp",EDGE,"E2")])],"isStart":false});
            fillet(context, id + "F28", {"entities" : qUnion([Q0, Q1, Q2, Q3, Q4, Q5, Q6, Q7, Q8, Q9, Q10, Q11, Q12, Q13]), "radius" : 2 * mm, "tangentPropagation" : true, "allowEdgeOverflow" : false});
        }
        {
            var Q0;
            Q0=makeQuery(id+"F25.opExtrude","CAP_EDGE",EDGE,{"disambiguationData":[OSD([sQuery(id+"F24.wireOp",EDGE,"E57.top")])],"isStart":false});
            var Q1;
            Q1=makeQuery(id+"F25.opExtrude","CAP_EDGE",EDGE,{"disambiguationData":[OSD([sQuery(id+"F24.wireOp",EDGE,"E57.bottom")])],"isStart":false});
            chamfer(context, id + "F29", {"entities" : qUnion([Q0, Q1]), "width" : 1 * mm, "tangentPropagation" : true});
        }
        {
            var Q0;
            Q0=makeQuery(id+"F1.opExtrude","SWEPT_FACE",FACE,{"disambiguationData":[OSD([sQuery(id+"F0.wireOp",EDGE,"E1")])]});
            var sketch = newSketch(context, id + "F30", { "sketchPlane" : qUnion([Q0])});
            skLineSegment(sketch, "E66", {"start": v(-25, -1) * mm, "end": v(-25, -20.21) * mm, "construction": true});
            skLineSegment(sketch, "E67", {"start": v(-48, -10.6) * mm, "end": v(-2, -10.6) * mm, "construction": true});
            skLineSegment(sketch, "E68.bottom", {"start": v(-16.82, -3.88) * mm, "end": v(-33.18, -3.88) * mm});
            skLineSegment(sketch, "E68.top", {"start": v(-16.82, -17.34) * mm, "end": v(-33.18, -17.34) * mm});
            skLineSegment(sketch, "E68.left", {"start": v(-16.82, -3.88) * mm, "end": v(-16.82, -17.34) * mm});
            skLineSegment(sketch, "E68.right", {"start": v(-33.18, -3.88) * mm, "end": v(-33.18, -17.34) * mm});
            skPoint(sketch, "E68.middle", {"position": v(-25, -10.6) * mm});
            skText(sketch, "E69", { "text": "OUT >", "fontName": "OpenSans-Bold.ttf"});
            const initialGuessF30  = {"E69": [-0.03165, -0.01237, 1, 0, 0.00334]};
            skSetInitialGuess(sketch, initialGuessF30);
            skSolve(sketch);
        }
        {
            var Q0;
            Q0=makeQuery(id+"F30.imprint","IMPRINT",FACE,{"disambiguationData":[TD([[makeQuery(id+"F30.imprint","IMPRINT",EDGE,{"derivedFrom":sQuery(id+"F30.wireOp",EDGE,"E69.sketch_text.stroke-8")}),1.0]])]});
            var Q1;
            Q1=makeQuery(id+"F30.imprint","IMPRINT",FACE,{"disambiguationData":[TD([[makeQuery(id+"F30.imprint","IMPRINT",EDGE,{"derivedFrom":sQuery(id+"F30.wireOp",EDGE,"E68.bottom")}),1.0]])]});
            extrude(context, id + "F31", {"entities" : qUnion([Q0, Q1]), "operationType" : NewBodyOperationType.ADD, "depth" : 1 * mm, "offsetDistance" : 25 * mm});
        }
        {
            var Q0;
            Q0=makeQuery(id+"F25.boolean.opBoolean","MERGE",FACE,{"derivedFrom":[makeQuery(id+"F20.boolean.opBoolean","MERGE",FACE,{"derivedFrom":[makeQuery(id+"F1.opExtrude","CAP_FACE",FACE,{"disambiguationData":[OSD([sQuery(id+"F0.wireOp",EDGE,"E0.bottom"),sQuery(id+"F0.wireOp",EDGE,"E0.top"),sQuery(id+"F0.wireOp",EDGE,"E0.left"),sQuery(id+"F0.wireOp",EDGE,"E0.right"),sQuery(id+"F0.wireOp",EDGE,"E1"),sQuery(id+"F0.wireOp",EDGE,"E2"),sQuery(id+"F0.wireOp",EDGE,"E3"),sQuery(id+"F0.wireOp",EDGE,"E4")])],"isStart":false}),makeQuery(id+"F20.opExtrude","SWEPT_FACE",FACE,{"disambiguationData":[OSD([sQuery(id+"F19.wireOp",EDGE,"E46")])]}),makeQuery(id+"F20.opExtrude","SWEPT_FACE",FACE,{"disambiguationData":[OSD([sQuery(id+"F19.wireOp",EDGE,"E53.MirrorCS")])]})]}),makeQuery(id+"F25.opExtrude","SWEPT_FACE",FACE,{"disambiguationData":[OSD([sQuery(id+"F24.wireOp",EDGE,"E63.MirrorCS")])]})]});
            var sketch = newSketch(context, id + "F32", { "sketchPlane" : qUnion([Q0])});
            skCircle(sketch, "E70", {"center": v(-34.17, 26.09) * mm, "radius": 1.5 * mm});
            skPoint(sketch, "E70.centerSnap0", {"position": v(-41.09, 26.09) * mm});
            skLineSegment(sketch, "E71", {"start": v(0, 33) * mm, "end": v(0, -35) * mm, "construction": true});
            skLineSegment(sketch, "E72", {"start": v(-48, 0) * mm, "end": v(51.5, 0) * mm, "construction": true});
            skCircle(sketch, "E73.MirrorC", {"center": v(34.17, 26.09) * mm, "radius": 1.5 * mm});
            skCircle(sketch, "E74.MirrorC", {"center": v(-34.17, -26.09) * mm, "radius": 1.5 * mm});
            skCircle(sketch, "E75.MirrorC", {"center": v(34.17, -26.09) * mm, "radius": 1.5 * mm});
            skSolve(sketch);
        }
        {
            var Q0;
            Q0=makeQuery(id+"F32.imprint","IMPRINT",FACE,{"disambiguationData":[TD([[makeQuery(id+"F32.imprint","IMPRINT",EDGE,{"derivedFrom":sQuery(id+"F32.wireOp",EDGE,"E70")}),1.0]])]});
            var Q1;
            Q1=makeQuery(id+"F32.imprint","IMPRINT",FACE,{"disambiguationData":[TD([[makeQuery(id+"F32.imprint","IMPRINT",EDGE,{"derivedFrom":sQuery(id+"F32.wireOp",EDGE,"E74.MirrorC")}),-1.0]])]});
            var Q2;
            Q2=makeQuery(id+"F32.imprint","IMPRINT",FACE,{"disambiguationData":[TD([[makeQuery(id+"F32.imprint","IMPRINT",EDGE,{"derivedFrom":sQuery(id+"F32.wireOp",EDGE,"E73.MirrorC")}),-1.0]])]});
            var Q3;
            Q3=makeQuery(id+"F32.imprint","IMPRINT",FACE,{"disambiguationData":[TD([[makeQuery(id+"F32.imprint","IMPRINT",EDGE,{"derivedFrom":sQuery(id+"F32.wireOp",EDGE,"E75.MirrorC")}),1.0]])]});
            extrude(context, id + "F33", {"entities" : qUnion([Q0, Q1, Q2, Q3]), "operationType" : NewBodyOperationType.ADD, "depth" : 1 * mm, "offsetDistance" : 25 * mm});
        }
    });
